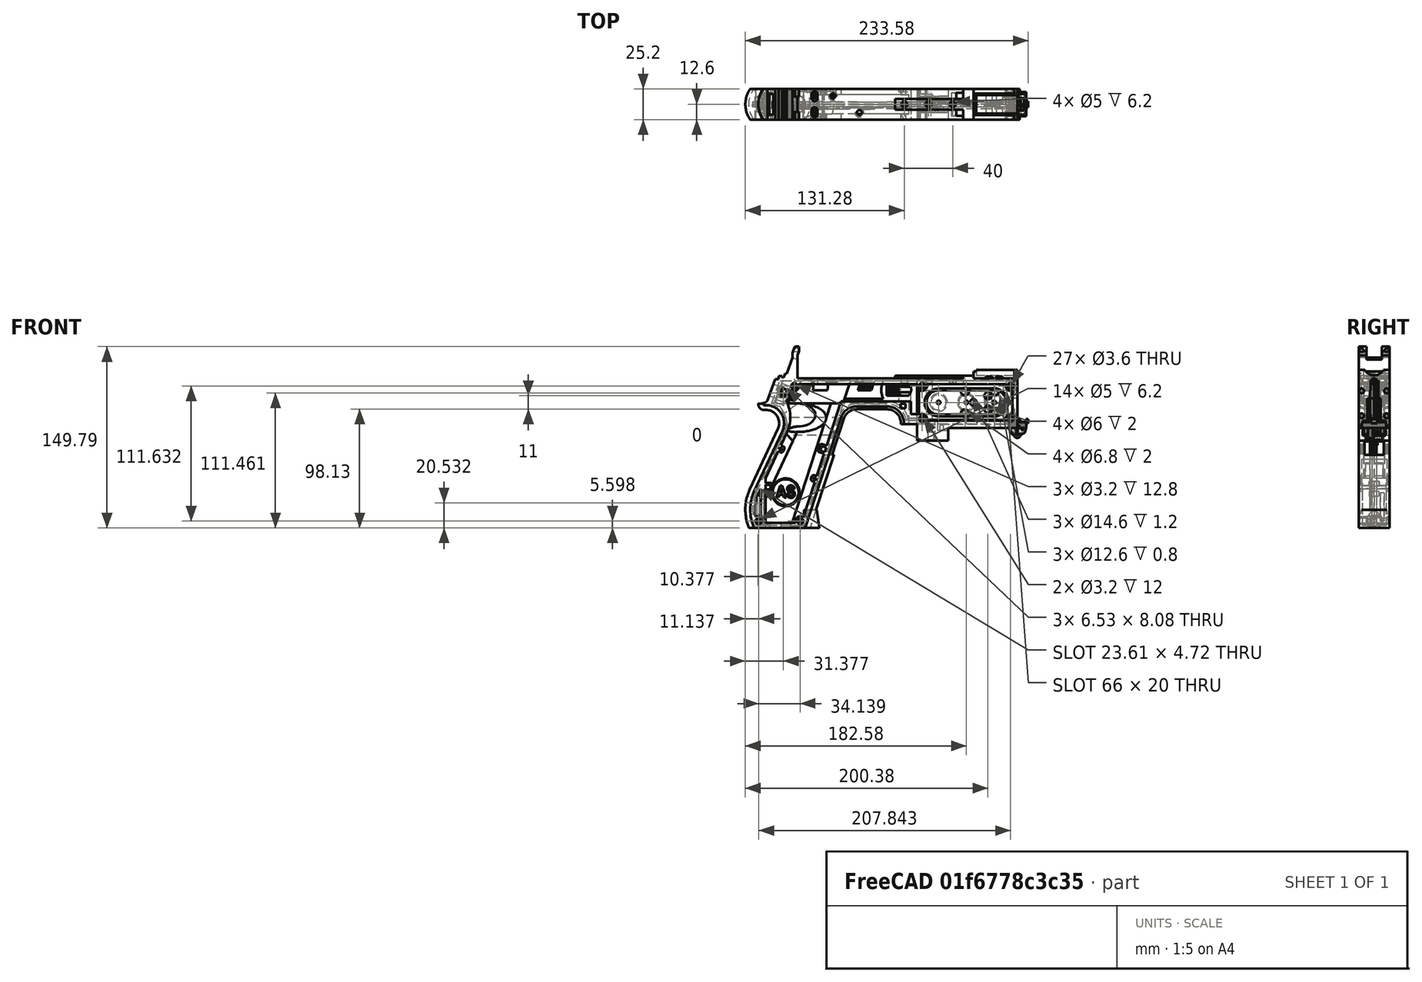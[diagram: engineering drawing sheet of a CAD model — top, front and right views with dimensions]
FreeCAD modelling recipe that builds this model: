
FCSTD DOCUMENT  (FreeCAD 1.0R39319 (Git))
Label: PICON-OF_ver_33
License: All rights reserved
LicenseURL: https://en.wikipedia.org/wiki/All_rights_reserved
objects: Sketcher::SketchObject×120, Part::Extrusion×75, Part::Cut×47, PartDesign::Pad×19, PartDesign::Chamfer×14, PartDesign::Pocket×13, PartDesign::Fillet×9, PartDesign::Body×8, Part::MultiFuse×6, PartDesign::SubtractivePipe×4, PartDesign::SubtractiveLoft×4, Part::Part2DObjectPython×3, PartDesign::Plane×2, PartDesign::SubShapeBinder×2, Part::Sweep×1, PartDesign::ShapeBinder×1, PartDesign::FeatureBase×1, Part::Cone×1, Part::Chamfer×1, Part::Mirroring×1, +1 more types
note: 579 computed .brp shape members not serialized (recipe doc carries the construction recipe); baked Part::Feature solids carry a one-line shape summary decoded from their .brp

FEATURE [Sketcher::SketchObject] Sketch  label="corpo principale"
  ArcFitTolerance = 1e-06
  AttacherType = Attacher::AttachEngine3D
  AttachmentSupport = -> [XZ_Plane]
  FullyConstrained = true
  MakeInternals = false
  MapMode = 5
  Placement = pos=(0,0,0) rot=(1,0,0;1.5708rad)
  sketch-geometry (65):
    g0: LineSegment StartX=0 StartY=0 StartZ=0 EndX=-57.2 EndY=0 EndZ=0
    g1: LineSegment StartX=-57.2 StartY=0 StartZ=0 EndX=-57.2 EndY=-10.4 EndZ=0
    g2: LineSegment StartX=-57.2 StartY=-10.4 StartZ=0 EndX=-82.8 EndY=-10.4 EndZ=0
    g3: LineSegment StartX=-82.8 StartY=-10.4 StartZ=0 EndX=-82.8 EndY=3.2 EndZ=0
    g4: LineSegment StartX=-82.8 StartY=3.2 StartZ=0 EndX=-93.6 EndY=3.2 EndZ=0
    g5: LineSegment StartX=-93.6 StartY=3.2 StartZ=0 EndX=-93.6 EndY=4 EndZ=0
    g6: LineSegment StartX=-107.6 StartY=18 StartZ=0 EndX=-132.428 EndY=18 EndZ=0
    g7: LineSegment StartX=-145.743 StartY=8.32624 StartZ=0 EndX=-175.232 EndY=-82.4316 EndZ=0
    g8: LineSegment StartX=-175.232 StartY=-82.4316 StartZ=0 EndX=-217.232 EndY=-82.4316 EndZ=0
    g9: LineSegment StartX=-217.232 StartY=-52.1862 StartZ=0 EndX=-193.988 EndY=-2.33927 EndZ=0
    g10: LineSegment StartX=-206.196 StartY=23.0857 StartZ=0 EndX=-199.861 EndY=40.4914 EndZ=0
    g11: LineSegment StartX=-199.861 StartY=40.4914 StartZ=0 EndX=-197.061 EndY=40.4914 EndZ=0
    g12: LineSegment StartX=-197.061 StartY=40.4914 StartZ=0 EndX=-197.061 EndY=42.8914 EndZ=0
    g13: LineSegment StartX=-197.061 StartY=42.8914 StartZ=0 EndX=-194.261 EndY=42.8914 EndZ=0
    g14: LineSegment StartX=-194.261 StartY=42.8914 StartZ=0 EndX=-194.535 EndY=42.1397 EndZ=0
    g15: LineSegment StartX=-194.535 StartY=42.1397 StartZ=0 EndX=-193.031 EndY=41.5924 EndZ=0
    g16: LineSegment StartX=-193.031 StartY=41.5924 StartZ=0 EndX=-191.663 EndY=45.3512 EndZ=0
    g17: LineSegment StartX=-191.663 StartY=45.3512 StartZ=0 EndX=-190.536 EndY=44.9408 EndZ=0
    g18: LineSegment StartX=-190.536 StartY=44.9408 StartZ=0 EndX=-185.747 EndY=58.0965 EndZ=0
    g19: LineSegment StartX=-185.747 StartY=58.0965 StartZ=0 EndX=-185.747 EndY=62.0965 EndZ=0
    g20: LineSegment StartX=-185.747 StartY=62.0965 StartZ=0 EndX=-183.832 EndY=67.3588 EndZ=0
    g21: LineSegment StartX=-183.832 StartY=67.3588 StartZ=0 EndX=-180.232 EndY=67.3588 EndZ=0
    g22: LineSegment StartX=-180.232 StartY=67.3588 StartZ=0 EndX=-180.232 EndY=63.7588 EndZ=0
    g23: LineSegment StartX=-180.232 StartY=63.7588 StartZ=0 EndX=-181.6 EndY=60 EndZ=0
    g24: LineSegment StartX=-181.6 StartY=60 StartZ=0 EndX=-181.6 EndY=41.2 EndZ=0
    g25: LineSegment StartX=-181.6 StartY=41.2 StartZ=0 EndX=-100.8 EndY=41.2 EndZ=0
    g26: LineSegment StartX=-36 StartY=43.2 StartZ=0 EndX=-36 EndY=41.2 EndZ=0
    g27: LineSegment StartX=0 StartY=48 StartZ=0 EndX=0 EndY=0 EndZ=0
    g28: LineSegment StartX=-209.901 StartY=19.85 StartZ=0 EndX=-209.901 EndY=20.1 EndZ=0
    g29: LineSegment StartX=-208.001 StartY=22 StartZ=0 EndX=-207.747 EndY=22 EndZ=0
    g30: LineSegment StartX=-207.583 StartY=19 StartZ=0 EndX=-209.051 EndY=19 EndZ=0
    g31: ArcOfCircle CenterX=-208.001 CenterY=20.1 CenterZ=0 NormalX=0 NormalY=0 NormalZ=1 AngleXU=0 Radius=1.9 StartAngle=1.5708 EndAngle=3.14159
    g32: GeomPoint [constr] X=-209.901 Y=22 Z=0
    g33: ArcOfCircle CenterX=-209.051 CenterY=19.85 CenterZ=0 NormalX=0 NormalY=0 NormalZ=1 AngleXU=0 Radius=0.85 StartAngle=3.14159 EndAngle=4.71239
    g34: GeomPoint [constr] X=-209.901 Y=19 Z=0
    g35: ArcOfCircle CenterX=-207.747 CenterY=23.65 CenterZ=0 NormalX=0 NormalY=0 NormalZ=1 AngleXU=0 Radius=1.65 StartAngle=4.71239 EndAngle=5.93412
    g36: GeomPoint [constr] X=-206.591 Y=22 Z=0
    g37: LineSegment StartX=-4 StartY=6 StartZ=0 EndX=-4 EndY=36.4 EndZ=0
    g38: LineSegment StartX=-4 StartY=36.4 StartZ=0 EndX=-185.2 EndY=36.4 EndZ=0
    g39: LineSegment StartX=-185.2 StartY=36.4 StartZ=0 EndX=-190.441 EndY=22 EndZ=0
    g40: LineSegment StartX=-214.575 StartY=-78.4316 StartZ=0 EndX=-178.142 EndY=-78.4316 EndZ=0
    g41: LineSegment StartX=-178.142 StartY=-78.4316 StartZ=0 EndX=-145.51 EndY=22 EndZ=0
    g42: LineSegment StartX=-145.51 StartY=22 StartZ=0 EndX=-87.91 EndY=22 EndZ=0
    g43: LineSegment StartX=-87.91 StartY=22 StartZ=0 EndX=-87.91 EndY=11.6 EndZ=0
    g44: LineSegment StartX=-87.91 StartY=11.6 StartZ=0 EndX=-80.11 EndY=11.6 EndZ=0
    g45: LineSegment StartX=-80.11 StartY=11.6 StartZ=0 EndX=-80.11 EndY=6 EndZ=0
    g46: LineSegment StartX=-80.11 StartY=6 StartZ=0 EndX=-4 EndY=6 EndZ=0
    g47: LineSegment StartX=-190.363 StartY=-4.02975 StartZ=0 EndX=-213.607 EndY=-53.8767 EndZ=0
    g48: ArcOfCircle CenterX=-132.428 CenterY=4 CenterZ=0 NormalX=0 NormalY=0 NormalZ=1 AngleXU=0 Radius=14 StartAngle=1.5708 EndAngle=2.82743
    g49: GeomPoint [constr] X=-142.6 Y=18 Z=0
    g50: ArcOfCircle CenterX=-107.6 CenterY=4 CenterZ=0 NormalX=0 NormalY=0 NormalZ=1 AngleXU=0 Radius=14 StartAngle=0 EndAngle=1.5708
    g51: GeomPoint [constr] X=-93.6 Y=18 Z=0
    g52: ArcOfCircle CenterX=-184.801 CenterY=-67.3089 CenterZ=0 NormalX=0 NormalY=0 NormalZ=1 AngleXU=0 Radius=35.7833 StartAngle=2.70526 EndAngle=3.57792
    g53: ArcOfCircle CenterX=-207.583 CenterY=4 CenterZ=0 NormalX=0 NormalY=0 NormalZ=1 AngleXU=0 Radius=15 StartAngle=5.84685 EndAngle=7.85398
    g54: LineSegment [constr] StartX=-213.607 StartY=-53.8767 StartZ=0 EndX=-217.232 EndY=-52.1862 EndZ=0
    g55: ArcOfCircle CenterX=-184.801 CenterY=-67.3089 CenterZ=0 NormalX=0 NormalY=0 NormalZ=1 AngleXU=0 Radius=31.7833 StartAngle=2.70526 EndAngle=3.49911
    g56: ArcOfCircle CenterX=-218.095 CenterY=8.90192 CenterZ=0 NormalX=0 NormalY=0 NormalZ=1 AngleXU=0 Radius=30.5989 StartAngle=5.84685 EndAngle=6.72553
    g57: LineSegment StartX=-44.6 StartY=43.2 StartZ=0 EndX=-36 EndY=43.2 EndZ=0
    g58: LineSegment StartX=-100.8 StartY=41.2 StartZ=0 EndX=-44.6 EndY=41.2 EndZ=0
    g59: LineSegment StartX=-44.6 StartY=41.2 StartZ=0 EndX=-44.6 EndY=43.2 EndZ=0
    g60: LineSegment StartX=-2.4 StartY=48 StartZ=0 EndX=0 EndY=48 EndZ=0
    g61: LineSegment StartX=-36 StartY=41.2 StartZ=0 EndX=-2.4 EndY=41.2 EndZ=0
    g62: LineSegment StartX=-2.4 StartY=41.2 StartZ=0 EndX=-2.4 EndY=48 EndZ=0
    g63: LineSegment [constr] StartX=-181.6 StartY=36.4 StartZ=0 EndX=-152.209 EndY=36.4 EndZ=0
    g64: LineSegment [constr] StartX=-181.6 StartY=36.4 StartZ=0 EndX=-130.41 EndY=36.4 EndZ=0
  constraints (183):
    c: Coincident(g-1,g0)
    c: PointOnObject(g0,g-1)
    c: Coincident(g0,g1)
    c: Vertical(g1)
    c: Coincident(g1,g2)
    c: Horizontal(g2)
    c: Coincident(g2,g3)
    c: Vertical(g3)
    c: Coincident(g3,g4)
    c: Coincident(g4,g5)
    c: Vertical(g5)
    c: Horizontal(g6)
    c: Coincident(g7,g8)
    c: Horizontal(g8)
    c: Coincident(g10,g11)
    c: Horizontal(g11)
    c: Coincident(g11,g12)
    c: Vertical(g12)
    c: Coincident(g12,g13)
    c: Horizontal(g13)
    c: Coincident(g13,g14)
    c: Coincident(g14,g15)
    c: Coincident(g15,g16)
    c: Coincident(g16,g17)
    c: Coincident(g17,g18)
    c: Coincident(g18,g19)
    c: Vertical(g19)
    c: Coincident(g19,g20)
    c: Coincident(g20,g21)
    c: Horizontal(g21)
    c: Coincident(g21,g22)
    c: Vertical(g22)
    c: Coincident(g22,g23)
    c: Coincident(g23,g24)
    c: Vertical(g24)
    c: Coincident(g24,g25)
    c: Horizontal(g25)
    c: Coincident(g57,g26)
    c: Vertical(g26)
    c: Coincident(g26,g61)
    c: PointOnObject(g60,g-2)
    c: Coincident(g60,g27)
    c: Coincident(g27,g0)
    c: DistanceY(g27,g27) = 48
    c: DistanceY(g1,g1) = 10.4
    c: DistanceX(g0,g0) = 57.2
    c: DistanceX(g2,g2) = 25.6
    c: Horizontal(g4)
    c: DistanceY(g3,g3) = 13.6
    c: DistanceX(g4,g4) = 10.8
    c: DistanceY(g5,g51) = 14.8
    c: DistanceX(g49,g51) = 49
    c: Distance(g7,g49) = 105.6
    c: DistanceX(g61,g60) = 36
    c: DistanceX(g25,g25) = 80.8
    c: DistanceY(g24,g24) = 18.8
    c: DistanceY(g22,g22) = 3.6
    c: Distance(g23) = 4
    c: Angle(g-1,g23) = 1.22173
    c: DistanceX(g21,g21) = 3.6
    c: Distance(g20) = 5.6
    c: Angle(g-1,g20) = 1.22173
    c: DistanceY(g19,g19) = 4
    c: Distance(g18) = 14
    c: Angle(g-1,g18) = 1.22173
    c: Distance(g17) = 1.2
    c: Distance(g16) = 4
    c: Angle(g16) = 1.22173
    c: Perpendicular(g18,g17)
    c: Distance(g15) = 1.6
    c: Perpendicular(g16,g15)
    c: Distance(g14) = 0.8
    c: DistanceX(g13,g13) = 2.8
    c: Perpendicular(g15,g14)
    c: DistanceY(g12,g12) = 2.4
    c: DistanceX(g11,g11) = 2.8
    c: Distance(g9) = 55
    c: Angle(g9,g-1) = 2.00713
    c: Horizontal(g29)
    c: Vertical(g28)
    c: Horizontal(g30)
    c: PointOnObject(g32,g29)
    c: PointOnObject(g32,g28)
    c: Tangent(g29,g31) = 1.5708
    c: Tangent(g28,g31) = 1.5708
    c: PointOnObject(g34,g28)
    c: PointOnObject(g34,g30)
    c: Tangent(g28,g33) = 1.5708
    c: Tangent(g30,g33) = 1.5708
    c: PointOnObject(g36,g29)
    c: PointOnObject(g36,g10)
    c: Tangent(g29,g35) = -1.5708
    c: Tangent(g10,g35) = -1.5708
    c: Angle(g-1,g10) = 1.22173
    c: Radius(g35) = 1.65
    c: Vertical(g37)
    c: Coincident(g37,g38)
    c: Horizontal(g38)
    c: Coincident(g38,g39)
    c: Horizontal(g40)
    c: Coincident(g40,g41)
    c: Coincident(g41,g42)
    c: Horizontal(g42)
    c: Coincident(g42,g43)
    c: Vertical(g43)
    c: Coincident(g43,g44)
    c: Horizontal(g44)
    c: Coincident(g44,g45)
    c: Vertical(g45)
    c: Coincident(g45,g46)
    c: Coincident(g46,g37)
    c: Horizontal(g46)
    c: DistanceY(g0,g37) = 6
    c: DistanceX(g37,g0) = 4
    c: DistanceY(g37,g25) = 4.8
    c: DistanceX(g38,g38) = 181.2
    c: DistanceX(g42,g42) = 57.6
    c: DistanceY(g49,g41) = 4
    c: DistanceX(g41,g49) = 2.91
    c: DistanceY(g43,g43) = 10.4
    c: DistanceX(g44,g44) = 7.8
    c: DistanceY(g7,g40) = 4
    c: Distance(g47) = 55
    c: Angle(g-1,g39) = 1.22173
    c: PointOnObject(g49,g7)
    c: PointOnObject(g49,g6)
    c: Tangent(g7,g48) = -1.5708
    c: Tangent(g6,g48) = -1.5708
    c: PointOnObject(g51,g5)
    c: PointOnObject(g51,g6)
    c: Tangent(g5,g50) = -1.5708
    c: Tangent(g6,g50) = -1.5708
    c: Radius(g50) = 14
    c: Radius(g48) = 14
    c: DistanceX(g8,g8) = 42
    c: Angle(g7,g-1) = 1.88496
    c: Parallel(g41,g7)
    c: Parallel(g47,g9)
    c: Coincident(g52,g8)
    c: Tangent(g52,g9) = 1.5708
    c: DistanceX(g9,g8) = 0
    c: Tangent(g53,g9) = -1.5708
    c: Tangent(g53,g30) = -1.5708
    c: Diameter(g53) = 30
    c: DistanceY(g53,g0) = -4
    c: Coincident(g54,g47)
    c: Distance(g54) = 4
    c: Coincident(g54,g9)
    c: Coincident(g55,g40)
    c: Tangent(g55,g47) = -1.5708
    c: Coincident(g52,g55)
    c: Coincident(g56,g39)
    c: Tangent(g56,g47) = 1.5708
    c: Horizontal(g57)
    c: DistanceX(g57,g57) = 8.6
    c: Coincident(g58,g25)
    c: Horizontal(g58)
    c: Coincident(g59,g58)
    c: Vertical(g59)
    c: DistanceY(g58,g57) = 2
    c: DistanceX(g58,g58) = 56.2
    c: Coincident(g59,g57)
    c: DistanceY(g41,g36) = 0
    c: DistanceY(g36,g39) = 0
    c: DistanceY(g28,g28) = 0.25
    c: DistanceX(g30,g36) = 2.46
    c: DistanceX(g28,g29) = 1.9
    c: Coincident(g62,g60)
    c: Horizontal(g60)
    c: DistanceX(g62,g27) = 2.4
    c: Coincident(g61,g62)
    c: DistanceY(g26,g26) = 2
    c: Vertical(g62)
    c: DistanceY(g61,g60) = 6.8
    c: Horizontal(g61)
    c: Distance(g63) = 29.391
    c: PointOnObject(g63,g38)
    c: PointOnObject(g63,g38)
    c: Distance(g64) = 51.19
    c: PointOnObject(g64,g38)
    c: PointOnObject(g64,g38)
    c: DistanceX(g24,g63) = 0
    c: DistanceX(g24,g64) = 0
FEATURE [Part::Extrusion] Extrude  label="Extrude corpo principale"
  Base = -> Sketch
  Dir = (0,-1,2e-16)
  DirMode = 2
  FaceMakerClass = Part::FaceMakerBullseye
  FaceMakerMode = 3
  LengthFwd = 25.2
  LengthRev = 12.6
  Solid = true
  Symmetric = true
FEATURE [Sketcher::SketchObject] Sketch002  label="scavo grilletto"
  ArcFitTolerance = 1e-06
  AttachmentSupport = -> [XZ_Plane]
  ExternalGeometry = -> [Sketch]
  FullyConstrained = true
  MakeInternals = false
  MapMode = 5
  Placement = pos=(0,0,0) rot=(1,0,0;1.5708rad)
  sketch-geometry (4):
    g0: LineSegment StartX=-89.51 StartY=22 StartZ=0 EndX=-152.71 EndY=22 EndZ=0
    g1: LineSegment StartX=-152.71 StartY=22 StartZ=0 EndX=-167.006 EndY=-22 EndZ=0
    g2: LineSegment StartX=-167.006 StartY=-22 StartZ=0 EndX=-89.51 EndY=-22 EndZ=0
    g3: LineSegment StartX=-89.51 StartY=-22 StartZ=0 EndX=-89.51 EndY=22 EndZ=0
  constraints (12):
    c: Horizontal(g0)
    c: Coincident(g0,g1)
    c: Coincident(g1,g2)
    c: Horizontal(g2)
    c: Coincident(g2,g3)
    c: Coincident(g3,g0)
    c: Vertical(g3)
    c: Angle(g1,g0) = 1.88496
    c: DistanceY(g3,g3) = 44
    c: DistanceX(g0,g0) = 63.2
    c: DistanceX(g0,g-3) = 1.6
    c: DistanceY(g-3,g0) = 0
FEATURE [Sketcher::SketchObject] Sketch004  label="traiettoria arrotondamento impugnatura anteriore"
  ArcFitTolerance = 1e-06
  AttachmentSupport = -> [XZ_Plane]
  ExternalGeometry = -> [Sketch]
  FullyConstrained = true
  MakeInternals = false
  MapMode = 5
  Placement = pos=(0,0,0) rot=(1,0,0;1.5708rad)
  sketch-geometry (13):
    g0: LineSegment StartX=-175.232 StartY=-82.4316 StartZ=0 EndX=-145.743 EndY=8.32624 EndZ=0
    g1: LineSegment StartX=-93.6 StartY=3.2 StartZ=0 EndX=-93.6 EndY=4 EndZ=0
    g2: LineSegment StartX=-132.428 StartY=18 StartZ=0 EndX=-107.6 EndY=18 EndZ=0
    g3: ArcOfCircle CenterX=-132.428 CenterY=4 CenterZ=0 NormalX=0 NormalY=0 NormalZ=1 AngleXU=0 Radius=14 StartAngle=1.5708 EndAngle=2.82743
    g4: ArcOfCircle CenterX=-107.6 CenterY=4 CenterZ=0 NormalX=0 NormalY=0 NormalZ=1 AngleXU=0 Radius=14 StartAngle=0 EndAngle=1.5708
    g5: LineSegment StartX=-175.232 StartY=-82.4316 StartZ=0 EndX=-217.232 EndY=-82.4316 EndZ=0
    g6: LineSegment StartX=-217.232 StartY=-52.1862 StartZ=0 EndX=-193.988 EndY=-2.33927 EndZ=0
    g7: LineSegment StartX=-209.051 StartY=19 StartZ=0 EndX=-207.583 EndY=19 EndZ=0
    g8: LineSegment StartX=-209.901 StartY=20.1 StartZ=0 EndX=-209.901 EndY=19.85 EndZ=0
    g9: ArcOfCircle CenterX=-184.801 CenterY=-67.3089 CenterZ=0 NormalX=0 NormalY=0 NormalZ=1 AngleXU=0 Radius=35.7833 StartAngle=2.70526 EndAngle=3.57792
    g10: ArcOfCircle CenterX=-207.583 CenterY=4 CenterZ=0 NormalX=0 NormalY=0 NormalZ=1 AngleXU=0 Radius=15 StartAngle=5.84685 EndAngle=7.85398
    g11: ArcOfCircle CenterX=-209.051 CenterY=19.85 CenterZ=0 NormalX=0 NormalY=0 NormalZ=1 AngleXU=0 Radius=0.85 StartAngle=3.14159 EndAngle=4.71239
    g12: ArcOfCircle CenterX=-208.001 CenterY=20.1 CenterZ=0 NormalX=0 NormalY=0 NormalZ=1 AngleXU=0 Radius=1.9 StartAngle=1.5708 EndAngle=3.14159
  constraints (26):
    c: Coincident(g0,g-3)
    c: Coincident(g0,g-6)
    c: Coincident(g1,g-8)
    c: Coincident(g1,g-7)
    c: Coincident(g2,g-5)
    c: Coincident(g2,g-4)
    c: Coincident(g3,g2)
    c: Tangent(g3,g0) = 1.5708
    c: Coincident(g4,g1)
    c: Tangent(g4,g2) = 1.5708
    c: Coincident(g5,g0)
    c: Coincident(g5,g-9)
    c: Coincident(g6,g-12)
    c: Coincident(g6,g-11)
    c: Coincident(g7,g-15)
    c: Coincident(g7,g-14)
    c: Coincident(g8,g-16)
    c: Coincident(g8,g-17)
    c: Tangent(g9,g6) = 1.5708
    c: Coincident(g9,g5)
    c: Coincident(g10,g7)
    c: Tangent(g10,g6) = -1.5708
    c: Tangent(g11,g7) = -1.5708
    c: Coincident(g11,g8)
    c: Tangent(g12,g8) = -1.5708
    c: Coincident(g12,g-17)
FEATURE [PartDesign::Plane] DatumPlane  label="Piano per disegno arrotondamento impugnatura"
  AttachmentSupport = -> [Sketch]
  Length = 68.5841
  MapMode = 7
  Placement = pos=(-145.743,1.8e-15,8.32624) rot=(0.154555,0.154555,0.97582;1.59527rad)
  ResizeMode = 0
  Width = 191.269
FEATURE [Sketcher::SketchObject] Sketch005  label="forma arrotondamento impugnatura anteriore"
  ArcFitTolerance = 1e-06
  AttachmentSupport = -> [DatumPlane]
  FullyConstrained = true
  MakeInternals = false
  MapMode = 5
  Placement = pos=(-145.743,1.8e-15,8.32624) rot=(0.154555,0.154555,0.97582;1.59527rad)
  sketch-geometry (5):
    g0: GeomPoint [constr] X=0 Y=-4 Z=0
    g1: GeomPoint [constr] X=-12.6 Y=7.1e-15 Z=0
    g2: GeomPoint [constr] X=12.6 Y=4.97e-14 Z=0
    g3: LineSegment StartX=-12.6 StartY=7.1e-15 StartZ=0 EndX=12.6 EndY=4.97e-14 EndZ=0
    g4: ArcOfCircle CenterX=-3.88e-14 CenterY=17.845 CenterZ=0 NormalX=0 NormalY=0 NormalZ=1 AngleXU=0 Radius=21.845 StartAngle=4.09759 EndAngle=5.32718
  constraints (11):
    c: DistanceY(g0,g-1) = 4
    c: DistanceX(g-1,g0) = 0
    c: DistanceX(g1,g-1) = 12.6
    c: DistanceX(g-1,g2) = 12.6
    c: DistanceY(g-1,g2) = 0
    c: DistanceY(g-1,g1) = 0
    c: Coincident(g3,g1)
    c: Coincident(g3,g2)
    c: Coincident(g4,g1)
    c: Coincident(g4,g2)
    c: PointOnObject(g0,g4)
FEATURE [Part::Sweep] Sweep  label="Sweep impugnatura"
  Frenet = true
  Sections = -> [Sketch005]
  Solid = true
  Spine = -> Sketch [Edge32,Edge33,Edge34,Edge35,Edge36,Edge37,Edge38,Edge39,Edge40,Edge41,Edge42,Edge43,Edge44]
  Transition = 1
FEATURE [Sketcher::SketchObject] Sketch008  label="buchi e pulizie varie"
  ArcFitTolerance = 1e-06
  AttachmentSupport = -> [XZ_Plane]
  ExternalGeometry = -> [Sketch]
  FullyConstrained = true
  MakeInternals = false
  MapMode = 5
  Placement = pos=(0,0,0) rot=(1,0,0;1.5708rad)
  sketch-geometry (26):
    g0: LineSegment StartX=-96.278 StartY=20.155 StartZ=0 EndX=-92.278 EndY=20.155 EndZ=0
    g1: LineSegment StartX=-92.278 StartY=20.155 StartZ=0 EndX=-92.278 EndY=16.155 EndZ=0
    g2: LineSegment StartX=-92.278 StartY=16.155 StartZ=0 EndX=-96.278 EndY=16.155 EndZ=0
    g3: LineSegment StartX=-96.278 StartY=16.155 StartZ=0 EndX=-96.278 EndY=20.155 EndZ=0
    g4: LineSegment StartX=-222.232 StartY=-82.4316 StartZ=0 EndX=-170.232 EndY=-82.4316 EndZ=0
    g5: LineSegment StartX=-170.232 StartY=-82.4316 StartZ=0 EndX=-170.232 EndY=-86.4316 EndZ=0
    g6: LineSegment StartX=-170.232 StartY=-86.4316 StartZ=0 EndX=-222.232 EndY=-86.4316 EndZ=0
    g7: LineSegment StartX=-222.232 StartY=-86.4316 StartZ=0 EndX=-222.232 EndY=-82.4316 EndZ=0
    g8: LineSegment StartX=-213.901 StartY=20.1 StartZ=0 EndX=-213.901 EndY=26 EndZ=0
    g9: LineSegment StartX=-213.901 StartY=26 StartZ=0 EndX=-206.196 EndY=26 EndZ=0
    g10: LineSegment StartX=-17.4 StartY=42.8 StartZ=0 EndX=-12.4 EndY=42.8 EndZ=0
    g11: LineSegment StartX=-12.4 StartY=42.8 StartZ=0 EndX=-12.4 EndY=41.2 EndZ=0
    g12: LineSegment StartX=-12.4 StartY=41.2 StartZ=0 EndX=-17.4 EndY=41.2 EndZ=0
    g13: LineSegment StartX=-17.4 StartY=41.2 StartZ=0 EndX=-17.4 EndY=42.8 EndZ=0
    g14: LineSegment StartX=-25.9 StartY=42.8 StartZ=0 EndX=-20.9 EndY=42.8 EndZ=0
    g15: LineSegment StartX=-20.9 StartY=42.8 StartZ=0 EndX=-20.9 EndY=41.2 EndZ=0
    g16: LineSegment StartX=-20.9 StartY=41.2 StartZ=0 EndX=-25.9 EndY=41.2 EndZ=0
    g17: LineSegment StartX=-25.9 StartY=41.2 StartZ=0 EndX=-25.9 EndY=42.8 EndZ=0
    g18: GeomPoint [constr] X=-206.196 Y=23.0857 Z=0
    g19: GeomPoint [constr] X=-213.901 Y=20.1 Z=0
    g20: BSplineCurve PolesCount=4 KnotsCount=2 Degree=3 IsPeriodic=0
    g21-g24: Circle [constr] x4 (B-spline internal-alignment scaffolding for g20; pole/knot coordinates omitted)
    g25: LineSegment StartX=-206.196 StartY=26 StartZ=0 EndX=-206.196 EndY=23.0857 EndZ=0
  constraints (73):
    c: Horizontal(g0)
    c: Coincident(g1,g0)
    c: Vertical(g1)
    c: Coincident(g2,g1)
    c: Horizontal(g2)
    c: Coincident(g3,g2)
    c: Coincident(g3,g0)
    c: Vertical(g3)
    c: DistanceX(g0,g-4) = 4.368
    c: DistanceY(g0,g-4) = 1.845
    c: DistanceY(g1,g1) = 4
    c: DistanceX(g2,g2) = 4
    c: Horizontal(g4)
    c: Coincident(g5,g4)
    c: Vertical(g5)
    c: Coincident(g6,g5)
    c: Horizontal(g6)
    c: Coincident(g7,g6)
    c: Coincident(g7,g4)
    c: Vertical(g7)
    c: DistanceY(g7,g7) = 4
    c: DistanceX(g4,g-5) = 5
    c: DistanceX(g-5,g4) = 5
    c: DistanceY(g4,g-5) = 0
    c: Coincident(g9,g8)
    c: Parallel(g9,g-6)
    c: DistanceX(g8,g-8) = 4
    c: Horizontal(g10)
    c: Coincident(g11,g10)
    c: Vertical(g11)
    c: Coincident(g12,g11)
    c: Horizontal(g12)
    c: Coincident(g13,g12)
    c: Coincident(g13,g10)
    c: Vertical(g13)
    c: Horizontal(g14)
    c: Coincident(g15,g14)
    c: Vertical(g15)
    c: Coincident(g16,g15)
    c: Horizontal(g16)
    c: Coincident(g17,g16)
    c: Coincident(g17,g14)
    c: Vertical(g17)
    c: DistanceY(g11,g10) = 1.6
    c: DistanceX(g10,g10) = 5
    c: DistanceY(g15,g14) = 1.6
    c: DistanceX(g14,g14) = 5
    c: DistanceX(g15,g12) = 3.5
    c: DistanceX(g11,g-9) = 10
    c: DistanceY(g-9,g11) = 0
    c: DistanceY(g-9,g15) = 0
    c: Perpendicular(g8,g9)
    c: DistanceY(g-7,g9) = 4
    c: DistanceY(g8,g-8) = 0
    c: InternalAlignment(g18,g20)
    c: InternalAlignment(g19,g20)
    c: InternalAlignment(g21,g20)
    c: Weight(g21) = 1
    c: InternalAlignment(g22,g20)
    c: Equal(g22,g21)
    c: InternalAlignment(g23,g20)
    c: Equal(g23,g21)
    c: InternalAlignment(g24,g20)
    c: Equal(g24,g21)
    c: Coincident(g18,g-12)
    c: Coincident(g19,g8)
    c: Coincident(g25,g9)
    c: Coincident(g25,g20)
    c: Vertical(g25)
    c: DistanceY(g20,g23) = 0
    c: DistanceY(g22,g18) = 2.26
    c: DistanceX(g22,g18) = 0.93
    c: DistanceX(g20,g23) = 2.9
FEATURE [Part::Extrusion] Extrude004  label="Extrude Buchi e pulizie varie"
  Base = -> Sketch008
  Dir = (0,-1,2e-16)
  DirMode = 2
  FaceMakerClass = Part::FaceMakerBullseye
  FaceMakerMode = 3
  LengthFwd = 25.2
  LengthRev = 0
  Solid = true
  Symmetric = true
FEATURE [Sketcher::SketchObject] Sketch009  label="rinforzi"
  ArcFitTolerance = 1e-06
  AttachmentSupport = -> [XZ_Plane]
  ExternalGeometry = -> [Sketch]
  FullyConstrained = true
  MakeInternals = false
  MapMode = 5
  Placement = pos=(0,0,0) rot=(1,0,0;1.5708rad)
  sketch-geometry (9):
    g0: LineSegment StartX=-87.91 StartY=22 StartZ=0 EndX=-87.91 EndY=36.4 EndZ=0
    g1: LineSegment StartX=-87.91 StartY=36.4 StartZ=0 EndX=-97.91 EndY=36.4 EndZ=0
    g2: LineSegment StartX=-97.91 StartY=36.4 StartZ=0 EndX=-97.91 EndY=22 EndZ=0
    g3: LineSegment StartX=-97.91 StartY=22 StartZ=0 EndX=-87.91 EndY=22 EndZ=0
    g4: LineSegment StartX=-149.713 StartY=9.06563 StartZ=0 EndX=-154.586 EndY=-5.93437 EndZ=0
    g5: LineSegment StartX=-154.586 StartY=-5.93437 StartZ=0 EndX=-191.863 EndY=-5.93437 EndZ=0
    g6: LineSegment StartX=-191.863 StartY=-5.93437 StartZ=0 EndX=-191.863 EndY=9.06563 EndZ=0
    g7: LineSegment StartX=-191.863 StartY=9.06563 StartZ=0 EndX=-149.713 EndY=9.06563 EndZ=0
    g8: LineSegment [constr] StartX=-145.51 StartY=22 StartZ=0 EndX=-149.713 EndY=9.06563 EndZ=0
  constraints (25):
    c: Vertical(g0)
    c: Coincident(g1,g0)
    c: Horizontal(g1)
    c: Coincident(g2,g1)
    c: Vertical(g2)
    c: Coincident(g3,g2)
    c: Coincident(g3,g0)
    c: Horizontal(g3)
    c: Coincident(g0,g-4)
    c: DistanceX(g3,g3) = 10
    c: DistanceY(g0,g-3) = 0
    c: Coincident(g5,g4)
    c: Horizontal(g5)
    c: Coincident(g6,g5)
    c: Vertical(g6)
    c: Coincident(g7,g6)
    c: Coincident(g7,g4)
    c: Horizontal(g7)
    c: Distance(g8) = 13.6
    c: Parallel(g-6,g8)
    c: Coincident(g-6,g8)
    c: Parallel(g4,g-6)
    c: DistanceY(g4,g4) = 15
    c: Coincident(g4,g8)
    c: DistanceX(g-5,g5) = -1.5
FEATURE [Part::Extrusion] Extrude001  label="Extrude scavo grilletto"
  Base = -> Sketch002
  Dir = (0,-1,2e-16)
  DirMode = 2
  FaceMakerClass = Part::FaceMakerBullseye
  FaceMakerMode = 3
  LengthFwd = 16
  LengthRev = 0
  Solid = true
  Symmetric = true
FEATURE [Part::Extrusion] Extrude005  label="Extrude Rinforzi"
  Base = -> Sketch009
  Dir = (0,-1,2e-16)
  DirMode = 2
  FaceMakerClass = Part::FaceMakerBullseye
  FaceMakerMode = 3
  LengthFwd = 2
  LengthRev = 0
  Placement = pos=(0,12.6,0) rot=(0,0,1;0rad)
  Solid = true
  Symmetric = false
FEATURE [PartDesign::ShapeBinder] CopyCut
  TraceSupport = false
FEATURE [PartDesign::Plane] DatumPlane001
  AttachmentSupport = -> [CopyCut]
  Length = 60
  MapMode = 5
  Placement = pos=(0,12.6,0) rot=(0,0.707107,0.707107;3.14159rad)
  ResizeMode = 0
  Width = 60
FEATURE [Sketcher::SketchObject] Sketch010  label="buco neopixel"
  ArcFitTolerance = 1e-06
  AttachmentSupport = -> [XZ_Plane]
  ExternalGeometry = -> [Sketch]
  FullyConstrained = true
  MakeInternals = false
  MapMode = 5
  Placement = pos=(0,0,0) rot=(1,0,0;1.5708rad)
  sketch-geometry (5):
    g0: LineSegment [constr] StartX=-199.861 StartY=40.4914 StartZ=0 EndX=-201.368 EndY=36.3521 EndZ=0
    g1: LineSegment StartX=-201.368 StartY=36.3521 StartZ=0 EndX=-204.932 EndY=26.5605 EndZ=0
    g2: LineSegment StartX=-201.368 StartY=36.3521 StartZ=0 EndX=-180.2 EndY=28.6477 EndZ=0
    g3: LineSegment StartX=-180.2 StartY=28.6477 StartZ=0 EndX=-183.764 EndY=18.8561 EndZ=0
    g4: LineSegment StartX=-183.764 StartY=18.8561 StartZ=0 EndX=-204.932 EndY=26.5605 EndZ=0
  constraints (14):
    c: Parallel(g0,g-3)
    c: Distance(g0) = 4.405
    c: Coincident(g0,g-3)
    c: Coincident(g2,g1)
    c: Coincident(g3,g2)
    c: Coincident(g4,g3)
    c: Coincident(g4,g1)
    c: Parallel(g1,g-3)
    c: Distance(g1) = 10.42
    c: Coincident(g1,g0)
    c: Parallel(g2,g4)
    c: Perpendicular(g1,g2)
    c: DistanceX(g-4,g2) = 5
    c: Parallel(g3,g1)
FEATURE [Part::Extrusion] Extrude006  label="Extrude buco neopixel"
  Base = -> Sketch010
  Dir = (0,-1,2e-16)
  DirMode = 2
  FaceMakerClass = Part::FaceMakerBullseye
  FaceMakerMode = 3
  LengthFwd = 17.2
  LengthRev = 0
  Solid = true
  Symmetric = true
FEATURE [Sketcher::SketchObject] Sketch011  label="fermo grilletto"
  ArcFitTolerance = 1e-06
  AttachmentSupport = -> [XZ_Plane]
  ExternalGeometry = -> [Sketch]
  FullyConstrained = true
  MakeInternals = false
  MapMode = 5
  Placement = pos=(0,0,0) rot=(1,0,0;1.5708rad)
  sketch-geometry (18):
    g0: LineSegment [constr] StartX=-145.51 StartY=22 StartZ=0 EndX=-157.347 EndY=-14.4293 EndZ=0
    g1: LineSegment [constr] StartX=-157.347 StartY=-14.4293 StartZ=0 EndX=-157.841 EndY=-15.951 EndZ=0
    g2: LineSegment StartX=-161.151 StartY=-13.1932 StartZ=0 EndX=-155.825 EndY=-14.9237 EndZ=0
    g3: LineSegment StartX=-163.167 StartY=-14.2205 StartZ=0 EndX=-164.403 EndY=-18.0247 EndZ=0
    g4: LineSegment StartX=-163.376 StartY=-20.0408 StartZ=0 EndX=-158.05 EndY=-21.7713 EndZ=0
    g5: LineSegment StartX=-158.05 StartY=-21.7713 StartZ=0 EndX=-155.825 EndY=-14.9237 EndZ=0
    g6: LineSegment StartX=-161.645 StartY=-14.7149 StartZ=0 EndX=-157.841 EndY=-15.951 EndZ=0
    g7: LineSegment StartX=-157.841 StartY=-15.951 StartZ=0 EndX=-159.077 EndY=-19.7552 EndZ=0
    g8: LineSegment StartX=-159.077 StartY=-19.7552 StartZ=0 EndX=-162.881 EndY=-18.5191 EndZ=0
    g9: LineSegment StartX=-162.881 StartY=-18.5191 StartZ=0 EndX=-161.645 EndY=-14.7149 EndZ=0
    g10: LineSegment [constr] StartX=-161.645 StartY=-14.7149 StartZ=0 EndX=-161.151 EndY=-13.1932 EndZ=0
    g11: LineSegment [constr] StartX=-159.077 StartY=-19.7552 StartZ=0 EndX=-157.555 EndY=-20.2496 EndZ=0
    g12: LineSegment [constr] StartX=-159.077 StartY=-19.7552 StartZ=0 EndX=-159.572 EndY=-21.2769 EndZ=0
    g13: LineSegment [constr] StartX=-161.645 StartY=-14.7149 StartZ=0 EndX=-163.167 EndY=-14.2205 EndZ=0
    g14: ArcOfCircle CenterX=-161.645 CenterY=-14.7149 CenterZ=0 NormalX=0 NormalY=0 NormalZ=1 AngleXU=0 Radius=1.6 StartAngle=1.25664 EndAngle=2.82743
    g15: GeomPoint [constr] X=-162.673 Y=-12.6988 Z=0
    g16: ArcOfCircle CenterX=-162.881 CenterY=-18.5191 CenterZ=0 NormalX=0 NormalY=0 NormalZ=1 AngleXU=0 Radius=1.6 StartAngle=2.82743 EndAngle=4.39823
    g17: GeomPoint [constr] X=-164.897 Y=-19.5464 Z=0
  constraints (48):
    c: Parallel(g0,g-3)
    c: Distance(g0) = 38.304
    c: Coincident(g0,g-3)
    c: Parallel(g1,g-3)
    c: Distance(g1) = 1.6
    c: Coincident(g1,g0)
    c: Coincident(g5,g4)
    c: Coincident(g5,g2)
    c: Coincident(g7,g6)
    c: Coincident(g8,g7)
    c: Coincident(g9,g8)
    c: Coincident(g9,g6)
    c: Parallel(g7,g-3)
    c: Parallel(g9,g7)
    c: Perpendicular(g6,g7)
    c: Parallel(g6,g8)
    c: Distance(g6) = 4
    c: Distance(g9) = 4
    c: Parallel(g5,g7)
    c: Parallel(g9,g3)
    c: Parallel(g2,g6)
    c: Parallel(g4,g8)
    c: Parallel(g13,g6)
    c: Parallel(g10,g9)
    c: Parallel(g11,g8)
    c: Parallel(g12,g7)
    c: Distance(g10) = 1.6
    c: Distance(g13) = 1.6
    c: Distance(g12) = 1.6
    c: Distance(g11) = 1.6
    c: Coincident(g10,g6)
    c: Coincident(g13,g6)
    c: Coincident(g12,g7)
    c: Coincident(g11,g7)
    c: Distance(g10,g15) = 1.6
    c: Distance(g15,g13) = 1.6
    c: Distance(g4,g12) = 1.6
    c: Distance(g4,g11) = 1.6
    c: PointOnObject(g15,g2)
    c: Tangent(g3,g14) = -1.5708
    c: Tangent(g2,g14) = 1.5708
    c: PointOnObject(g17,g4)
    c: PointOnObject(g17,g3)
    c: Tangent(g4,g16) = -1.5708
    c: Tangent(g3,g16) = -1.5708
    c: Equal(g16,g14)
    c: Coincident(g16,g8)
    c: Coincident(g6,g1)
FEATURE [Part::Extrusion] Extrude007  label="Extrude fermo grilletto"
  Base = -> Sketch011
  Dir = (0,-1,2e-16)
  DirMode = 2
  FaceMakerClass = Part::FaceMakerBullseye
  FaceMakerMode = 3
  LengthFwd = 25.2
  LengthRev = 0
  Solid = true
  Symmetric = true
FEATURE [Sketcher::SketchObject] Sketch012  label="buco oled"
  ArcFitTolerance = 1e-06
  AttachmentSupport = -> [XZ_Plane]
  ExternalGeometry = -> [Sketch]
  FullyConstrained = true
  MakeInternals = false
  MapMode = 5
  Placement = pos=(0,0,0) rot=(1,0,0;1.5708rad)
  sketch-geometry (4):
    g0: LineSegment StartX=-185.747 StartY=58.0965 StartZ=0 EndX=-180.232 EndY=56.0891 EndZ=0
    g1: LineSegment StartX=-185.747 StartY=58.0965 StartZ=0 EndX=-185.747 EndY=67.3588 EndZ=0
    g2: LineSegment StartX=-185.747 StartY=67.3588 StartZ=0 EndX=-180.232 EndY=67.3588 EndZ=0
    g3: LineSegment StartX=-180.232 StartY=67.3588 StartZ=0 EndX=-180.232 EndY=56.0891 EndZ=0
  constraints (10):
    c: Coincident(g1,g0)
    c: Coincident(g2,g1)
    c: Coincident(g3,g2)
    c: Coincident(g3,g0)
    c: Parallel(g1,g-5)
    c: Perpendicular(g-3,g0)
    c: Parallel(g2,g-6)
    c: Parallel(g3,g-4)
    c: Coincident(g0,g-5)
    c: Coincident(g2,g-6)
FEATURE [Part::Extrusion] Extrude008  label="Extrude buco oled"
  Base = -> Sketch012
  Dir = (0,-1,2e-16)
  DirMode = 2
  FaceMakerClass = Part::FaceMakerBullseye
  FaceMakerMode = 3
  LengthFwd = 12.8
  LengthRev = 0
  Solid = true
  Symmetric = true
FEATURE [Sketcher::SketchObject] Sketch013  label="buco pompa"
  ArcFitTolerance = 1e-06
  AttachmentSupport = -> [XZ_Plane]
  ExternalGeometry = -> [Sketch]
  FullyConstrained = true
  MakeInternals = false
  MapMode = 5
  Placement = pos=(0,0,0) rot=(1,0,0;1.5708rad)
  sketch-geometry (8):
    g0: LineSegment StartX=-82.8 StartY=-10.4 StartZ=0 EndX=-82.8 EndY=-9.6 EndZ=0
    g1: LineSegment StartX=-82.8 StartY=-9.6 StartZ=0 EndX=-67.9 EndY=-9.6 EndZ=0
    g2: LineSegment StartX=-67.9 StartY=-9.6 StartZ=0 EndX=-67.9 EndY=6 EndZ=0
    g3: LineSegment StartX=-67.9 StartY=6 StartZ=0 EndX=-65.9 EndY=6 EndZ=0
    g4: LineSegment StartX=-65.9 StartY=6 StartZ=0 EndX=-65.9 EndY=-1.7 EndZ=0
    g5: LineSegment StartX=-65.9 StartY=-1.7 StartZ=0 EndX=-57.2 EndY=-1.7 EndZ=0
    g6: LineSegment StartX=-57.2 StartY=-1.7 StartZ=0 EndX=-57.2 EndY=-10.4 EndZ=0
    g7: LineSegment StartX=-57.2 StartY=-10.4 StartZ=0 EndX=-82.8 EndY=-10.4 EndZ=0
  constraints (22):
    c: Vertical(g0)
    c: Coincident(g1,g0)
    c: Horizontal(g1)
    c: Coincident(g2,g1)
    c: Vertical(g2)
    c: Coincident(g3,g2)
    c: Horizontal(g3)
    c: Coincident(g4,g3)
    c: Vertical(g4)
    c: Coincident(g5,g4)
    c: Horizontal(g5)
    c: Coincident(g6,g5)
    c: Vertical(g6)
    c: Coincident(g7,g6)
    c: Coincident(g7,g0)
    c: DistanceY(g0,g0) = 0.8
    c: DistanceY(g6,g6) = 8.7
    c: DistanceX(g1,g1) = 14.9
    c: DistanceX(g3,g3) = 2
    c: Coincident(g0,g-4)
    c: DistanceY(g2,g-6) = 0
    c: Coincident(g6,g-5)
FEATURE [Part::Extrusion] Extrude009  label="Extrude buco pompa"
  Base = -> Sketch013
  Dir = (0,-1,2e-16)
  DirMode = 2
  FaceMakerClass = Part::FaceMakerBullseye
  FaceMakerMode = 3
  LengthFwd = 13.2
  LengthRev = 0
  Solid = true
  Symmetric = true
FEATURE [Sketcher::SketchObject] Sketch014  label="buco frontale"
  ArcFitTolerance = 1e-06
  AttachmentSupport = -> [XZ_Plane]
  ExternalGeometry = -> [Sketch]
  FullyConstrained = true
  MakeInternals = false
  MapMode = 5
  Placement = pos=(0,0,0) rot=(1,0,0;1.5708rad)
  sketch-geometry (10):
    g0: LineSegment StartX=0 StartY=0 StartZ=0 EndX=0 EndY=24.671 EndZ=0
    g1: LineSegment StartX=0 StartY=24.671 StartZ=0 EndX=-4 EndY=24.671 EndZ=0
    g2: LineSegment StartX=-4 StartY=24.671 StartZ=0 EndX=-4 EndY=16 EndZ=0
    g3: LineSegment StartX=-4 StartY=16 StartZ=0 EndX=-2.4 EndY=16 EndZ=0
    g4: LineSegment StartX=-2.4 StartY=16 StartZ=0 EndX=-2.4 EndY=10 EndZ=0
    g5: LineSegment StartX=-2.4 StartY=10 StartZ=0 EndX=-12 EndY=10 EndZ=0
    g6: LineSegment StartX=-12 StartY=10 StartZ=0 EndX=-12 EndY=6 EndZ=0
    g7: LineSegment StartX=-12 StartY=6 StartZ=0 EndX=-2.4 EndY=6 EndZ=0
    g8: LineSegment StartX=-2.4 StartY=6 StartZ=0 EndX=-2.4 EndY=0 EndZ=0
    g9: LineSegment StartX=-2.4 StartY=0 StartZ=0 EndX=0 EndY=0 EndZ=0
  constraints (29):
    c: Vertical(g0)
    c: Coincident(g1,g0)
    c: Horizontal(g1)
    c: Coincident(g2,g1)
    c: Vertical(g2)
    c: Coincident(g3,g2)
    c: Horizontal(g3)
    c: Coincident(g4,g3)
    c: Vertical(g4)
    c: Coincident(g5,g4)
    c: Horizontal(g5)
    c: Coincident(g6,g5)
    c: Vertical(g6)
    c: Coincident(g7,g6)
    c: Coincident(g8,g7)
    c: Vertical(g8)
    c: Coincident(g9,g8)
    c: Coincident(g9,g0)
    c: Horizontal(g9)
    c: DistanceY(g0,g0) = 24.671
    c: Horizontal(g7)
    c: DistanceY(g6,g6) = 4
    c: DistanceY(g4,g4) = 6
    c: DistanceX(g9,g9) = 2.4
    c: Coincident(g0,g-1)
    c: DistanceY(g-3,g7) = 0
    c: DistanceX(g8,g4) = 0
    c: DistanceX(g-3,g1) = 0
    c: DistanceX(g6,g-3) = 8
FEATURE [Part::Extrusion] Extrude010  label="Extrude buco frontale"
  Base = -> Sketch014
  Dir = (0,-1,2e-16)
  DirMode = 2
  FaceMakerClass = Part::FaceMakerBullseye
  FaceMakerMode = 3
  LengthFwd = 11.2
  LengthRev = 0
  Solid = true
  Symmetric = true
FEATURE [Sketcher::SketchObject] Sketch015  label="guida rail"
  ArcFitTolerance = 1e-06
  AttachmentSupport = -> [XZ_Plane]
  ExternalGeometry = -> [Sketch]
  FullyConstrained = true
  MakeInternals = false
  MapMode = 5
  Placement = pos=(0,0,0) rot=(1,0,0;1.5708rad)
  sketch-geometry (4):
    g0: LineSegment StartX=-100.8 StartY=43.2 StartZ=0 EndX=-44.6 EndY=43.2 EndZ=0
    g1: LineSegment StartX=-44.6 StartY=43.2 StartZ=0 EndX=-44.6 EndY=41.2 EndZ=0
    g2: LineSegment StartX=-44.6 StartY=41.2 StartZ=0 EndX=-100.8 EndY=41.2 EndZ=0
    g3: LineSegment StartX=-100.8 StartY=41.2 StartZ=0 EndX=-100.8 EndY=43.2 EndZ=0
  constraints (9):
    c: Horizontal(g0)
    c: Coincident(g1,g0)
    c: Coincident(g2,g1)
    c: Coincident(g3,g2)
    c: Coincident(g3,g0)
    c: Vertical(g3)
    c: Coincident(g2,g-3)
    c: Coincident(g1,g-3)
    c: Coincident(g0,g-4)
FEATURE [Part::Extrusion] Extrude011  label="Extrude guida rail"
  Base = -> Sketch015
  Dir = (0,-1,2e-16)
  DirMode = 2
  FaceMakerClass = Part::FaceMakerBullseye
  FaceMakerMode = 3
  LengthFwd = 9
  LengthRev = 0
  Solid = true
  Symmetric = true
FEATURE [Sketcher::SketchObject] Sketch016  label="guide per coperture laterali"
  ArcFitTolerance = 1e-06
  AttachmentSupport = -> [XZ_Plane]
  ExternalGeometry = -> [Sketch]
  FullyConstrained = true
  MakeInternals = false
  MapMode = 5
  Placement = pos=(0,0,0) rot=(1,0,0;1.5708rad)
  sketch-geometry (14):
    g0: Circle CenterX=-5.6 CenterY=7.6 CenterZ=0 NormalX=0 NormalY=0 NormalZ=1 AngleXU=0 Radius=1.6
    g1: Circle CenterX=-5.6 CenterY=7.6 CenterZ=0 NormalX=0 NormalY=0 NormalZ=1 AngleXU=0 Radius=4
    g2: Circle CenterX=-5.6 CenterY=34.8 CenterZ=0 NormalX=0 NormalY=0 NormalZ=1 AngleXU=0 Radius=1.6
    g3: Circle CenterX=-5.6 CenterY=34.8 CenterZ=0 NormalX=0 NormalY=0 NormalZ=1 AngleXU=0 Radius=4
    g4: Circle CenterX=-184.08 CenterY=34.8 CenterZ=0 NormalX=0 NormalY=0 NormalZ=1 AngleXU=0 Radius=1.6
    g5: Circle CenterX=-184.08 CenterY=34.8 CenterZ=0 NormalX=0 NormalY=0 NormalZ=1 AngleXU=0 Radius=4
    g6: Circle CenterX=-179.305 CenterY=-76.8316 CenterZ=0 NormalX=0 NormalY=0 NormalZ=1 AngleXU=0 Radius=1.6
    g7: Circle CenterX=-179.305 CenterY=-76.8316 CenterZ=0 NormalX=0 NormalY=0 NormalZ=1 AngleXU=0 Radius=4
    g8: Circle CenterX=-213.443 CenterY=-76.8316 CenterZ=0 NormalX=0 NormalY=0 NormalZ=1 AngleXU=0 Radius=1.6
    g9: Circle CenterX=-213.443 CenterY=-76.8316 CenterZ=0 NormalX=0 NormalY=0 NormalZ=1 AngleXU=0 Radius=4
    g10: Circle CenterX=-78.51 CenterY=7.6 CenterZ=0 NormalX=0 NormalY=0 NormalZ=1 AngleXU=0 Radius=1.6
    g11: Circle CenterX=-78.51 CenterY=7.6 CenterZ=0 NormalX=0 NormalY=0 NormalZ=1 AngleXU=0 Radius=4
    g12: Circle CenterX=-78.51 CenterY=34.8 CenterZ=0 NormalX=0 NormalY=0 NormalZ=1 AngleXU=0 Radius=1.6
    g13: Circle CenterX=-78.51 CenterY=34.8 CenterZ=0 NormalX=0 NormalY=0 NormalZ=1 AngleXU=0 Radius=4
  constraints (35):
    c: Diameter(g0) = 3.2
    c: Diameter(g1) = 8
    c: Coincident(g0,g1)
    c: Diameter(g2) = 3.2
    c: Diameter(g3) = 8
    c: Coincident(g3,g2)
    c: Tangent(g2,g-7)
    c: Diameter(g4) = 3.2
    c: Diameter(g5) = 8
    c: Coincident(g5,g4)
    c: Tangent(g4,g-7)
    c: Tangent(g4,g-8)
    c: Diameter(g6) = 3.2
    c: Diameter(g7) = 8
    c: Coincident(g7,g6)
    c: Tangent(g6,g-9)
    c: Tangent(g6,g-10)
    c: Diameter(g8) = 3.2
    c: Diameter(g9) = 8
    c: Coincident(g9,g8)
    c: Tangent(g8,g-10)
    c: Tangent(g8,g-11)
    c: Diameter(g10) = 3.2
    c: Diameter(g11) = 8
    c: Diameter(g12) = 3.2
    c: Diameter(g13) = 8
    c: Coincident(g12,g13)
    c: Coincident(g10,g11)
    c: Tangent(g12,g-7)
    c: DistanceX(g12,g10) = 0
    c: Tangent(g2,g-6)
    c: Tangent(g0,g-6)
    c: Tangent(g0,g-3)
    c: Tangent(g10,g-3)
    c: Tangent(g10,g-4)
FEATURE [Part::Extrusion] Extrude012  label="extrude guide per coperture laterali"
  Base = -> Sketch016
  Dir = (0,-1,2e-16)
  DirMode = 2
  FaceMakerClass = Part::FaceMakerBullseye
  FaceMakerMode = 3
  LengthFwd = 25.2
  LengthRev = 0
  Solid = true
  Symmetric = true
FEATURE [Sketcher::SketchObject] Sketch017  label="supporto CAM"
  ArcFitTolerance = 1e-06
  AttachmentSupport = -> [XZ_Plane]
  ExternalGeometry = -> [Sketch]
  FullyConstrained = true
  MakeInternals = false
  MapMode = 5
  Placement = pos=(0,0,0) rot=(1,0,0;1.5708rad)
  sketch-geometry (6):
    g0: LineSegment StartX=-2.4 StartY=48 StartZ=0 EndX=-2.4 EndY=41.2 EndZ=0
    g1: LineSegment StartX=-2.4 StartY=48 StartZ=0 EndX=-34 EndY=48 EndZ=0
    g2: LineSegment StartX=-34 StartY=48 StartZ=0 EndX=-34 EndY=46.72 EndZ=0
    g3: LineSegment StartX=-34 StartY=46.72 StartZ=0 EndX=-36 EndY=46.72 EndZ=0
    g4: LineSegment StartX=-36 StartY=46.72 StartZ=0 EndX=-36 EndY=41.2 EndZ=0
    g5: LineSegment StartX=-36 StartY=41.2 StartZ=0 EndX=-2.4 EndY=41.2 EndZ=0
  constraints (15):
    c: Coincident(g1,g0)
    c: Horizontal(g1)
    c: Coincident(g2,g1)
    c: Vertical(g2)
    c: Coincident(g3,g2)
    c: Horizontal(g3)
    c: Coincident(g4,g3)
    c: Coincident(g5,g4)
    c: DistanceX(g1,g0) = 31.6
    c: Coincident(g5,g0)
    c: Vertical(g4)
    c: DistanceY(g2,g1) = 1.28
    c: Coincident(g0,g-3)
    c: Coincident(g0,g-3)
    c: Coincident(g4,g-4)
FEATURE [Part::Extrusion] Extrude013  label="Extrude supporto CAM"
  Base = -> Sketch017
  Dir = (0,-1,2e-16)
  DirMode = 2
  FaceMakerClass = Part::FaceMakerBullseye
  FaceMakerMode = 3
  LengthFwd = 17.8
  LengthRev = 0
  Solid = true
  Symmetric = true
FEATURE [Sketcher::SketchObject] Sketch018  label="Scavo CAM"
  ArcFitTolerance = 1e-06
  AttachmentSupport = -> [YZ_Plane]
  ExternalGeometry = -> [Sketch]
  FullyConstrained = true
  MakeInternals = false
  MapMode = 5
  Placement = pos=(0,0,0) rot=(0.57735,0.57735,0.57735;2.0944rad)
  sketch-geometry (4):
    g0: LineSegment StartX=-7.73 StartY=48 StartZ=0 EndX=7.73 EndY=48 EndZ=0
    g1: LineSegment [constr] StartX=1.07e-14 StartY=48 StartZ=0 EndX=0 EndY=43.5155 EndZ=0
    g2: ArcOfCircle CenterX=9e-15 CenterY=52.42 CenterZ=0 NormalX=0 NormalY=0 NormalZ=1 AngleXU=0 Radius=8.90445 StartAngle=3.66102 EndAngle=5.76376
    g3: Circle [constr] CenterX=9e-15 CenterY=52.42 CenterZ=0 NormalX=0 NormalY=0 NormalZ=1 AngleXU=0 Radius=8.9
  constraints (13):
    c: Horizontal(g0)
    c: DistanceY(g-3,g0) = 0
    c: DistanceX(g0,g0) = 15.46
    c: DistanceX(g0,g-3) = 7.73
    c: DistanceX(g-3) = 0
    c: Coincident(g1,g-3)
    c: PointOnObject(g1,g-2)
    c: Coincident(g2,g0)
    c: Coincident(g2,g0)
    c: PointOnObject(g1,g2)
    c: Diameter(g3) = 17.8
    c: DistanceY(g1,g3) = 4.42
    c: Coincident(g2,g3)
FEATURE [Part::Extrusion] Extrude014  label="Extrude Scavo CAM"
  Base = -> Sketch018
  Dir = (1,0,0)
  DirMode = 2
  FaceMakerClass = Part::FaceMakerBullseye
  FaceMakerMode = 3
  LengthFwd = -34
  LengthRev = 0
  Solid = true
  Symmetric = false
FEATURE [Sketcher::SketchObject] Sketch019  label="scavo rumble"
  ArcFitTolerance = 1e-06
  AttachmentSupport = -> [XZ_Plane]
  ExternalGeometry = -> [Sketch]
  FullyConstrained = true
  MakeInternals = false
  MapMode = 5
  Placement = pos=(0,0,0) rot=(1,0,0;1.5708rad)
  sketch-geometry (6):
    g0: LineSegment StartX=-164.575 StartY=-24.3786 StartZ=0 EndX=-159.439 EndY=-26.0473 EndZ=0
    g1: LineSegment StartX=-159.439 StartY=-26.0473 StartZ=0 EndX=-166.547 EndY=-47.9216 EndZ=0
    g2: LineSegment StartX=-166.547 StartY=-47.9216 StartZ=0 EndX=-171.682 EndY=-46.2529 EndZ=0
    g3: LineSegment StartX=-171.682 StartY=-46.2529 StartZ=0 EndX=-164.575 EndY=-24.3786 EndZ=0
    g4: LineSegment [constr] StartX=-145.51 StartY=22 StartZ=0 EndX=-160.961 EndY=-25.5528 EndZ=0
    g5: LineSegment [constr] StartX=-159.439 StartY=-26.0473 StartZ=0 EndX=-160.961 EndY=-25.5528 EndZ=0
  constraints (17):
    c: Coincident(g1,g0)
    c: Coincident(g2,g1)
    c: Coincident(g3,g2)
    c: Coincident(g3,g0)
    c: Parallel(g3,g-3)
    c: Parallel(g3,g1)
    c: Perpendicular(g3,g0)
    c: Perpendicular(g2,g3)
    c: Distance(g2,g0) = 23
    c: Parallel(g4,g-3)
    c: Distance(g4) = 50
    c: Coincident(g4,g-3)
    c: Parallel(g5,g0)
    c: Distance(g5) = 1.6
    c: Coincident(g5,g0)
    c: Distance(g5,g0) = 3.8
    c: Coincident(g5,g4)
FEATURE [Part::Extrusion] Extrude015  label="scavo rumble001"
  Base = -> Sketch019
  Dir = (0,-1,2e-16)
  DirMode = 2
  FaceMakerClass = Part::FaceMakerBullseye
  FaceMakerMode = 3
  LengthFwd = 21
  LengthRev = 0
  Solid = true
  Symmetric = true
FEATURE [Sketcher::SketchObject] Sketch020  label="fermo rumble"
  ArcFitTolerance = 1e-06
  AttachmentSupport = -> [XZ_Plane]
  ExternalGeometry = -> [Sketch019,Sketch]
  FullyConstrained = true
  MakeInternals = false
  MapMode = 5
  Placement = pos=(0,0,0) rot=(1,0,0;1.5708rad)
  sketch-geometry (16):
    g0: LineSegment [constr] StartX=-166.709 StartY=-43.2425 StartZ=0 EndX=-168.068 EndY=-47.4271 EndZ=0
    g1: LineSegment [constr] StartX=-168.068 StartY=-47.4271 StartZ=0 EndX=-166.547 EndY=-47.9216 EndZ=0
    g2: LineSegment StartX=-168.121 StartY=-40.4703 StartZ=0 EndX=-166.029 EndY=-41.1502 EndZ=0
    g3: LineSegment StartX=-166.029 StartY=-41.1502 StartZ=0 EndX=-166.709 EndY=-43.2425 EndZ=0
    g4: LineSegment StartX=-166.709 StartY=-43.2425 StartZ=0 EndX=-168.801 EndY=-42.5626 EndZ=0
    g5: LineSegment StartX=-168.801 StartY=-42.5626 StartZ=0 EndX=-168.121 EndY=-40.4703 EndZ=0
    g6: LineSegment StartX=-167.627 StartY=-38.9486 StartZ=0 EndX=-164.203 EndY=-40.0611 EndZ=0
    g7: LineSegment StartX=-164.203 StartY=-40.0611 StartZ=0 EndX=-165.81 EndY=-45.0066 EndZ=0
    g8: LineSegment StartX=-165.81 StartY=-45.0066 StartZ=0 EndX=-169.234 EndY=-43.8941 EndZ=0
    g9: LineSegment StartX=-170.261 StartY=-41.878 StartZ=0 EndX=-169.643 EndY=-39.9759 EndZ=0
    g10: LineSegment [constr] StartX=-169.643 StartY=-39.9759 StartZ=0 EndX=-169.148 EndY=-38.4542 EndZ=0
    g11: LineSegment [constr] StartX=-169.148 StartY=-38.4542 StartZ=0 EndX=-167.627 EndY=-38.9486 EndZ=0
    g12: ArcOfCircle CenterX=-168.739 CenterY=-42.3724 CenterZ=0 NormalX=0 NormalY=0 NormalZ=1 AngleXU=0 Radius=1.6 StartAngle=2.82743 EndAngle=4.39823
    g13: GeomPoint [constr] X=-170.755 Y=-43.3997 Z=0
    g14: ArcOfCircle CenterX=-168.121 CenterY=-40.4703 CenterZ=0 NormalX=0 NormalY=0 NormalZ=1 AngleXU=0 Radius=1.6 StartAngle=1.25664 EndAngle=2.82743
    g15: GeomPoint [constr] X=-169.148 Y=-38.4542 Z=0
  constraints (42):
    c: Parallel(g0,g-4)
    c: Distance(g0) = 4.4
    c: Coincident(g1,g0)
    c: Perpendicular(g0,g1)
    c: Distance(g1) = 1.6
    c: Coincident(g1,g-5)
    c: Coincident(g3,g2)
    c: Coincident(g4,g3)
    c: Coincident(g5,g4)
    c: Coincident(g5,g2)
    c: Parallel(g3,g-4)
    c: Parallel(g3,g5)
    c: Perpendicular(g2,g3)
    c: Parallel(g4,g2)
    c: Distance(g2) = 2.2
    c: Distance(g3) = 2.2
    c: Coincident(g7,g6)
    c: Coincident(g8,g7)
    c: Parallel(g7,g-4)
    c: Parallel(g7,g9)
    c: Perpendicular(g6,g7)
    c: Parallel(g6,g8)
    c: Distance(g6,g15) = 5.2
    c: Distance(g7) = 5.2
    c: Coincident(g11,g10)
    c: Parallel(g10,g9)
    c: Parallel(g11,g6)
    c: Distance(g10) = 1.6
    c: Distance(g11) = 1.6
    c: Coincident(g10,g15)
    c: Distance(g11,g2) = 1.6
    c: Distance(g2,g10) = 1.6
    c: PointOnObject(g13,g8)
    c: PointOnObject(g13,g9)
    c: Tangent(g8,g12) = 1.5708
    c: Tangent(g9,g12) = 1.5708
    c: PointOnObject(g15,g9)
    c: Tangent(g6,g14) = 1.5708
    c: Tangent(g9,g14) = 1.5708
    c: Equal(g12,g14)
    c: Coincident(g6,g11)
    c: Coincident(g3,g0)
FEATURE [Part::Extrusion] Extrude016  label="Extrude fermo rumble"
  Base = -> Sketch020
  Dir = (0,-1,2e-16)
  DirMode = 2
  FaceMakerClass = Part::FaceMakerBullseye
  FaceMakerMode = 3
  LengthFwd = 25.2
  LengthRev = 0
  Solid = true
  Symmetric = true
FEATURE [Sketcher::SketchObject] Sketch021  label="perno fermo rumble001"
  ArcFitTolerance = 1e-06
  AttachmentSupport = -> [XZ_Plane001]
  FullyConstrained = true
  MakeInternals = false
  MapMode = 5
  Placement = pos=(0,0,0) rot=(1,0,0;1.5708rad)
  sketch-geometry (16):
    g0: LineSegment StartX=0 StartY=0.45 StartZ=0 EndX=0 EndY=1.55 EndZ=0
    g1: LineSegment StartX=0.45 StartY=2 StartZ=0 EndX=1.55 EndY=2 EndZ=0
    g2: LineSegment StartX=2 StartY=1.55 StartZ=0 EndX=2 EndY=0.45 EndZ=0
    g3: LineSegment StartX=1.55 StartY=0 StartZ=0 EndX=0.45 EndY=0 EndZ=0
    g4: ArcOfCircle [constr] CenterX=0.45 CenterY=1.55 CenterZ=0 NormalX=0 NormalY=0 NormalZ=1 AngleXU=0 Radius=0.45 StartAngle=1.5708 EndAngle=3.14159
    g5: GeomPoint [constr] X=0 Y=2 Z=0
    g6: LineSegment StartX=0.45 StartY=2 StartZ=0 EndX=0 EndY=1.55 EndZ=0
    g7: ArcOfCircle [constr] CenterX=1.55 CenterY=1.55 CenterZ=0 NormalX=0 NormalY=0 NormalZ=1 AngleXU=0 Radius=0.45 StartAngle=0 EndAngle=1.5708
    g8: GeomPoint [constr] X=2 Y=2 Z=0
    g9: LineSegment StartX=2 StartY=1.55 StartZ=0 EndX=1.55 EndY=2 EndZ=0
    g10: ArcOfCircle [constr] CenterX=1.55 CenterY=0.45 CenterZ=0 NormalX=0 NormalY=0 NormalZ=1 AngleXU=0 Radius=0.45 StartAngle=4.71239 EndAngle=6.28319
    g11: GeomPoint [constr] X=2 Y=0 Z=0
    g12: LineSegment StartX=1.55 StartY=0 StartZ=0 EndX=2 EndY=0.45 EndZ=0
    g13: ArcOfCircle [constr] CenterX=0.45 CenterY=0.45 CenterZ=0 NormalX=0 NormalY=0 NormalZ=1 AngleXU=0 Radius=0.45 StartAngle=3.14159 EndAngle=4.71239
    g14: GeomPoint [constr] X=0 Y=0 Z=0
    g15: LineSegment StartX=0 StartY=0.45 StartZ=0 EndX=0.45 EndY=0 EndZ=0
  constraints (35):
    c: Coincident(g14,g-1)
    c: PointOnObject(g5,g-2)
    c: Horizontal(g1)
    c: Vertical(g2)
    c: Horizontal(g3)
    c: DistanceX(g5,g8) = 2
    c: DistanceY(g11,g8) = 2
    c: PointOnObject(g5,g0)
    c: PointOnObject(g5,g1)
    c: Tangent(g0,g4) = 1.5708
    c: Tangent(g1,g4) = 1.5708
    c: Coincident(g6,g0)
    c: Coincident(g6,g1)
    c: PointOnObject(g8,g2)
    c: PointOnObject(g8,g1)
    c: Tangent(g2,g7) = 1.5708
    c: Tangent(g1,g7) = 1.5708
    c: Coincident(g9,g2)
    c: Coincident(g9,g1)
    c: PointOnObject(g11,g2)
    c: PointOnObject(g11,g3)
    c: Tangent(g2,g10) = 1.5708
    c: Tangent(g3,g10) = 1.5708
    c: Coincident(g12,g2)
    c: Coincident(g12,g3)
    c: PointOnObject(g14,g0)
    c: PointOnObject(g14,g3)
    c: Tangent(g0,g13) = 1.5708
    c: Tangent(g3,g13) = 1.5708
    c: Coincident(g15,g0)
    c: Coincident(g15,g3)
    c: Equal(g6,g9)
    c: Equal(g9,g12)
    c: Equal(g12,g15)
    c: DistanceX(g14,g3) = 0.45
FEATURE [Part::Extrusion] Extrude017  label="Extrude perno fermo rumble"
  Base = -> Sketch021
  Dir = (0,-1,2e-16)
  DirMode = 2
  FaceMakerClass = Part::FaceMakerBullseye
  FaceMakerMode = 3
  LengthFwd = 25.2
  LengthRev = 0
  Solid = true
  Symmetric = true
FEATURE [Sketcher::SketchObject] Sketch022  label="fori per M3x5(OD)x6(L)"
  ArcFitTolerance = 1e-06
  AttachmentSupport = -> [XZ_Plane]
  ExternalGeometry = -> [Sketch016]
  FullyConstrained = true
  MakeInternals = false
  MapMode = 5
  Placement = pos=(0,0,0) rot=(1,0,0;1.5708rad)
  sketch-geometry (7):
    g0: Circle CenterX=-5.6 CenterY=34.8 CenterZ=0 NormalX=0 NormalY=0 NormalZ=1 AngleXU=0 Radius=2.5
    g1: Circle CenterX=-5.6 CenterY=7.6 CenterZ=0 NormalX=0 NormalY=0 NormalZ=1 AngleXU=0 Radius=2.5
    g2: Circle CenterX=-78.51 CenterY=34.8 CenterZ=0 NormalX=0 NormalY=0 NormalZ=1 AngleXU=0 Radius=2.5
    g3: Circle CenterX=-78.51 CenterY=7.6 CenterZ=0 NormalX=0 NormalY=0 NormalZ=1 AngleXU=0 Radius=2.5
    g4: Circle CenterX=-184.08 CenterY=34.8 CenterZ=0 NormalX=0 NormalY=0 NormalZ=1 AngleXU=0 Radius=2.5
    g5: Circle CenterX=-179.305 CenterY=-76.8316 CenterZ=0 NormalX=0 NormalY=0 NormalZ=1 AngleXU=0 Radius=2.5
    g6: Circle CenterX=-213.443 CenterY=-76.8316 CenterZ=0 NormalX=0 NormalY=0 NormalZ=1 AngleXU=0 Radius=2.5
  constraints (14):
    c: Diameter(g0) = 5
    c: Diameter(g1) = 5
    c: Diameter(g2) = 5
    c: Diameter(g3) = 5
    c: Diameter(g4) = 5
    c: Diameter(g5) = 5
    c: Diameter(g6) = 5
    c: Coincident(g0,g-8)
    c: Coincident(g1,g-9)
    c: Coincident(g2,g-6)
    c: Coincident(g3,g-7)
    c: Coincident(g4,g-5)
    c: Coincident(g5,g-4)
    c: Coincident(g6,g-3)
FEATURE [Part::Extrusion] Extrude018  label="Extrude fori M3x5x6 - dx"
  Base = -> Sketch022
  Dir = (0,-1,2e-16)
  DirMode = 2
  FaceMakerClass = Part::FaceMakerBullseye
  FaceMakerMode = 3
  LengthFwd = 6.2
  LengthRev = 0
  Placement = pos=(0,-9.5,0) rot=(0,0,1;0rad)
  Solid = true
  Symmetric = true
FEATURE [Part::Extrusion] Extrude019  label="Extrude fori M3x5x6 - sx"
  Base = -> Sketch022
  Dir = (0,-1,2e-16)
  DirMode = 2
  FaceMakerClass = Part::FaceMakerBullseye
  FaceMakerMode = 3
  LengthFwd = 6.2
  LengthRev = 0
  Placement = pos=(0,9.5,0) rot=(0,0,1;0rad)
  Solid = true
  Symmetric = true
FEATURE [Sketcher::SketchObject] Sketch023  label="foro anteriore M3x5x6"
  ArcFitTolerance = 1e-06
  AttachmentSupport = -> [YZ_Plane]
  FullyConstrained = true
  MakeInternals = false
  MapMode = 5
  Placement = pos=(0,0,0) rot=(0.57735,0.57735,0.57735;2.0944rad)
  sketch-geometry (2):
    g0: LineSegment [constr] StartX=0 StartY=0 StartZ=0 EndX=0 EndY=38.6 EndZ=0
    g1: Circle CenterX=0 CenterY=38.6 CenterZ=0 NormalX=0 NormalY=0 NormalZ=1 AngleXU=0 Radius=2.5
  constraints (5):
    c: Coincident(g0,g-1)
    c: PointOnObject(g0,g-2)
    c: DistanceY(g0,g0) = 38.6
    c: Diameter(g1) = 5
    c: Coincident(g1,g0)
FEATURE [Part::Extrusion] Extrude020  label="Extrude foro anteriore M3x5x6"
  Base = -> Sketch023
  Dir = (1,0,0)
  DirMode = 2
  FaceMakerClass = Part::FaceMakerBullseye
  FaceMakerMode = 3
  LengthFwd = -6.2
  LengthRev = 0
  Solid = true
  Symmetric = false
FEATURE [Sketcher::SketchObject] Sketch024  label="fori per viti frontale"
  ArcFitTolerance = 1e-06
  AttachmentSupport = -> [YZ_Plane]
  FullyConstrained = true
  MakeInternals = false
  MapMode = 5
  Placement = pos=(0,0,0) rot=(0.57735,0.57735,0.57735;2.0944rad)
  sketch-geometry (9):
    g0: LineSegment [constr] StartX=-10.3 StartY=30.721 StartZ=0 EndX=10.3 EndY=30.721 EndZ=0
    g1: LineSegment [constr] StartX=10.3 StartY=30.721 StartZ=0 EndX=10.3 EndY=10.121 EndZ=0
    g2: LineSegment [constr] StartX=10.3 StartY=10.121 StartZ=0 EndX=-10.3 EndY=10.121 EndZ=0
    g3: LineSegment [constr] StartX=-10.3 StartY=10.121 StartZ=0 EndX=-10.3 EndY=30.721 EndZ=0
    g4: LineSegment [constr] StartX=0 StartY=0 StartZ=0 EndX=0 EndY=10.121 EndZ=0
    g5: Circle CenterX=-10.3 CenterY=30.721 CenterZ=0 NormalX=0 NormalY=0 NormalZ=1 AngleXU=0 Radius=2
    g6: Circle CenterX=10.3 CenterY=30.721 CenterZ=0 NormalX=0 NormalY=0 NormalZ=1 AngleXU=0 Radius=2
    g7: Circle CenterX=-10.3 CenterY=10.121 CenterZ=0 NormalX=0 NormalY=0 NormalZ=1 AngleXU=0 Radius=2
    g8: Circle CenterX=10.3 CenterY=10.121 CenterZ=0 NormalX=0 NormalY=0 NormalZ=1 AngleXU=0 Radius=2
  constraints (22):
    c: Horizontal(g0)
    c: Coincident(g1,g0)
    c: Vertical(g1)
    c: Coincident(g2,g1)
    c: Horizontal(g2)
    c: Coincident(g3,g2)
    c: Coincident(g3,g0)
    c: Vertical(g3)
    c: DistanceX(g0,g0) = 20.6
    c: DistanceY(g3,g3) = 20.6
    c: Coincident(g4,g-1)
    c: PointOnObject(g4,g-2)
    c: DistanceY(g4,g4) = 10.121
    c: Symmetric(g2,g2,g4)
    c: Diameter(g5) = 4
    c: Diameter(g6) = 4
    c: Diameter(g7) = 4
    c: Diameter(g8) = 4
    c: Coincident(g5,g0)
    c: Coincident(g6,g0)
    c: Coincident(g7,g2)
    c: Coincident(g8,g1)
FEATURE [Part::Extrusion] Extrude021  label="Extrude fori per viti frontale"
  Base = -> Sketch024
  Dir = (1,0,0)
  DirMode = 2
  FaceMakerClass = Part::FaceMakerBullseye
  FaceMakerMode = 3
  LengthFwd = -2.4
  LengthRev = 0
  Solid = true
  Symmetric = false
FEATURE [Sketcher::SketchObject] Sketch025  label="foro per filo CAM"
  ArcFitTolerance = 1e-06
  AttachmentSupport = -> [XZ_Plane]
  ExternalGeometry = -> [Sketch]
  FullyConstrained = true
  MakeInternals = false
  MapMode = 5
  Placement = pos=(0,0,0) rot=(1,0,0;1.5708rad)
  sketch-geometry (4):
    g0: LineSegment StartX=-44.6 StartY=41.2 StartZ=0 EndX=-44.6 EndY=36.4 EndZ=0
    g1: LineSegment StartX=-44.6 StartY=36.4 StartZ=0 EndX=-54.6 EndY=36.4 EndZ=0
    g2: LineSegment StartX=-54.6 StartY=36.4 StartZ=0 EndX=-50.4 EndY=41.2 EndZ=0
    g3: LineSegment StartX=-50.4 StartY=41.2 StartZ=0 EndX=-44.6 EndY=41.2 EndZ=0
  constraints (11):
    c: Vertical(g0)
    c: Coincident(g1,g0)
    c: Horizontal(g1)
    c: Coincident(g2,g1)
    c: Coincident(g3,g2)
    c: Coincident(g3,g0)
    c: Horizontal(g3)
    c: Coincident(g0,g-3)
    c: DistanceY(g0,g-4) = 0
    c: DistanceX(g3,g3) = 5.8
    c: DistanceX(g1,g1) = 10
FEATURE [Part::Extrusion] Extrude022  label="Extrude foro per filo CAM dx"
  Base = -> Sketch025
  Dir = (0,-1,2e-16)
  DirMode = 2
  FaceMakerClass = Part::FaceMakerBullseye
  FaceMakerMode = 3
  LengthFwd = 4.9
  LengthRev = 0
  Placement = pos=(0,6.95,0) rot=(0,0,1;0rad)
  Solid = true
  Symmetric = true
FEATURE [Part::Extrusion] Extrude023  label="Extrude foro per filo CAM sx"
  Base = -> Sketch025
  Dir = (0,-1,2e-16)
  DirMode = 2
  FaceMakerClass = Part::FaceMakerBullseye
  FaceMakerMode = 3
  LengthFwd = 4.9
  LengthRev = 0
  Placement = pos=(0,-6.95,0) rot=(0,0,1;0rad)
  Solid = true
  Symmetric = true
FEATURE [Sketcher::SketchObject] Sketch026  label="foro sotto anteriore M3x5x6"
  ArcFitTolerance = 1e-06
  AttachmentSupport = -> [XY_Plane]
  FullyConstrained = true
  MakeInternals = false
  MapMode = 5
  sketch-geometry (2):
    g0: LineSegment [constr] StartX=0 StartY=0 StartZ=0 EndX=-16.5 EndY=0 EndZ=0
    g1: Circle CenterX=-16.5 CenterY=0 CenterZ=0 NormalX=0 NormalY=0 NormalZ=1 AngleXU=0 Radius=2.5
  constraints (5):
    c: Distance(g0) = 16.5
    c: Coincident(g0,g-1)
    c: PointOnObject(g0,g-1)
    c: Diameter(g1) = 5
    c: Coincident(g0,g1)
FEATURE [Sketcher::SketchObject] Sketch027  label="foro sotto posteriore M3x5x6"
  ArcFitTolerance = 1e-06
  AttachmentSupport = -> [XY_Plane]
  ExternalGeometry = -> [Sketch]
  FullyConstrained = true
  MakeInternals = false
  MapMode = 5
  sketch-geometry (2):
    g0: LineSegment [constr] StartX=-82.8 StartY=2e-16 StartZ=0 EndX=-71.3 EndY=2e-16 EndZ=0
    g1: Circle CenterX=-71.3 CenterY=2e-16 CenterZ=0 NormalX=0 NormalY=0 NormalZ=1 AngleXU=0 Radius=2.5
  constraints (5):
    c: Distance(g0) = 11.5
    c: Coincident(g0,g-3)
    c: PointOnObject(g0,g-3)
    c: Diameter(g1) = 5
    c: Coincident(g1,g0)
FEATURE [Sketcher::SketchObject] Sketch029  label="fori sotto impugnatura"
  ArcFitTolerance = 1e-06
  AttachmentSupport = -> [XY_Plane]
  ExternalGeometry = -> [Sketch]
  FullyConstrained = true
  MakeInternals = false
  MapMode = 5
  sketch-geometry (15):
    g0: LineSegment [constr] StartX=-175.232 StartY=-1.83e-14 StartZ=0 EndX=-191.232 EndY=0 EndZ=0
    g1: Circle CenterX=-191.232 CenterY=0 CenterZ=0 NormalX=0 NormalY=0 NormalZ=1 AngleXU=0 Radius=3.95
    g2: LineSegment [constr] StartX=-175.232 StartY=-1.83e-14 StartZ=0 EndX=-204.275 EndY=0 EndZ=0
    g3: LineSegment StartX=-204.275 StartY=3.525 StartZ=0 EndX=-204.275 EndY=-3.525 EndZ=0
    g4: LineSegment StartX=-205.4 StartY=-4.65 StartZ=0 EndX=-206.65 EndY=-4.65 EndZ=0
    g5: LineSegment StartX=-207.775 StartY=-3.525 StartZ=0 EndX=-207.775 EndY=3.525 EndZ=0
    g6: LineSegment StartX=-206.65 StartY=4.65 StartZ=0 EndX=-205.4 EndY=4.65 EndZ=0
    g7: ArcOfCircle CenterX=-206.65 CenterY=3.525 CenterZ=0 NormalX=0 NormalY=0 NormalZ=1 AngleXU=0 Radius=1.125 StartAngle=1.5708 EndAngle=3.14159
    g8: GeomPoint [constr] X=-207.775 Y=4.65 Z=0
    g9: ArcOfCircle CenterX=-205.4 CenterY=3.525 CenterZ=0 NormalX=0 NormalY=0 NormalZ=1 AngleXU=0 Radius=1.125 StartAngle=0 EndAngle=1.5708
    g10: GeomPoint [constr] X=-204.275 Y=4.65 Z=0
    g11: ArcOfCircle CenterX=-205.4 CenterY=-3.525 CenterZ=0 NormalX=0 NormalY=0 NormalZ=1 AngleXU=0 Radius=1.125 StartAngle=4.71239 EndAngle=6.28319
    g12: GeomPoint [constr] X=-204.275 Y=-4.65 Z=0
    g13: ArcOfCircle CenterX=-206.65 CenterY=-3.525 CenterZ=0 NormalX=0 NormalY=0 NormalZ=1 AngleXU=0 Radius=1.125 StartAngle=3.14159 EndAngle=4.71239
    g14: GeomPoint [constr] X=-207.775 Y=-4.65 Z=0
  constraints (35):
    c: Distance(g0) = 16
    c: Coincident(g0,g-3)
    c: PointOnObject(g0,g-1)
    c: Diameter(g1) = 7.9
    c: Coincident(g1,g0)
    c: Coincident(g2,g0)
    c: PointOnObject(g2,g-1)
    c: Vertical(g3)
    c: Horizontal(g4)
    c: Vertical(g5)
    c: Horizontal(g6)
    c: DistanceY(g12,g10) = 9.3
    c: DistanceX(g8,g10) = 3.5
    c: Symmetric(g10,g12,g2)
    c: PointOnObject(g8,g5)
    c: PointOnObject(g8,g6)
    c: Tangent(g5,g7) = 1.5708
    c: Tangent(g6,g7) = 1.5708
    c: PointOnObject(g10,g3)
    c: PointOnObject(g10,g6)
    c: Tangent(g3,g9) = 1.5708
    c: Tangent(g6,g9) = 1.5708
    c: PointOnObject(g12,g3)
    c: PointOnObject(g12,g4)
    c: Tangent(g3,g11) = 1.5708
    c: Tangent(g4,g11) = 1.5708
    c: PointOnObject(g14,g4)
    c: PointOnObject(g14,g5)
    c: Tangent(g4,g13) = 1.5708
    c: Tangent(g5,g13) = 1.5708
    c: Equal(g7,g9)
    c: Equal(g9,g11)
    c: Equal(g11,g13)
    c: DistanceX(g6,g6) = 1.25
    c: DistanceX(g-5,g5) = 6.8
FEATURE [Sketcher::SketchObject] Sketch030  label="fori superiori per solenoide e oled"
  ArcFitTolerance = 1e-06
  AttachmentSupport = -> [XY_Plane]
  ExternalGeometry = -> [Sketch]
  FullyConstrained = true
  MakeInternals = false
  MapMode = 5
  sketch-geometry (33):
    g0: LineSegment [constr] StartX=-181.6 StartY=1.12e-14 StartZ=0 EndX=-169.91 EndY=0 EndZ=0
    g1: LineSegment [constr] StartX=-169.91 StartY=0 StartZ=0 EndX=-169.91 EndY=-2.6 EndZ=0
    g2: LineSegment [constr] StartX=-169.91 StartY=0 StartZ=0 EndX=-169.91 EndY=2.6 EndZ=0
    g3: LineSegment StartX=-169.91 StartY=4.975 StartZ=0 EndX=-169.91 EndY=8.225 EndZ=0
    g4: LineSegment StartX=-167.535 StartY=10.6 StartZ=0 EndX=-167.285 EndY=10.6 EndZ=0
    g5: LineSegment StartX=-164.91 StartY=8.225 StartZ=0 EndX=-164.91 EndY=4.975 EndZ=0
    g6: LineSegment StartX=-167.285 StartY=2.6 StartZ=0 EndX=-167.535 EndY=2.6 EndZ=0
    g7: LineSegment StartX=-169.91 StartY=-4.975 StartZ=0 EndX=-169.91 EndY=-8.225 EndZ=0
    g8: LineSegment StartX=-167.535 StartY=-10.6 StartZ=0 EndX=-167.285 EndY=-10.6 EndZ=0
    g9: LineSegment StartX=-164.91 StartY=-8.225 StartZ=0 EndX=-164.91 EndY=-4.975 EndZ=0
    g10: LineSegment StartX=-167.285 StartY=-2.6 StartZ=0 EndX=-167.535 EndY=-2.6 EndZ=0
    g11: ArcOfCircle CenterX=-167.535 CenterY=8.225 CenterZ=0 NormalX=0 NormalY=0 NormalZ=1 AngleXU=0 Radius=2.375 StartAngle=1.5708 EndAngle=3.14159
    g12: GeomPoint [constr] X=-169.91 Y=10.6 Z=0
    g13: ArcOfCircle CenterX=-167.285 CenterY=8.225 CenterZ=0 NormalX=0 NormalY=0 NormalZ=1 AngleXU=0 Radius=2.375 StartAngle=0 EndAngle=1.5708
    g14: GeomPoint [constr] X=-164.91 Y=10.6 Z=0
    g15: ArcOfCircle CenterX=-167.285 CenterY=4.975 CenterZ=0 NormalX=0 NormalY=0 NormalZ=1 AngleXU=0 Radius=2.375 StartAngle=4.71239 EndAngle=6.28319
    g16: GeomPoint [constr] X=-164.91 Y=2.6 Z=0
    g17: ArcOfCircle CenterX=-167.535 CenterY=4.975 CenterZ=0 NormalX=0 NormalY=0 NormalZ=1 AngleXU=0 Radius=2.375 StartAngle=3.14159 EndAngle=4.71239
    g18: GeomPoint [constr] X=-169.91 Y=2.6 Z=0
    g19: ArcOfCircle CenterX=-167.535 CenterY=-4.975 CenterZ=0 NormalX=0 NormalY=0 NormalZ=1 AngleXU=0 Radius=2.375 StartAngle=1.5708 EndAngle=3.14159
    g20: GeomPoint [constr] X=-169.91 Y=-2.6 Z=0
    g21: ArcOfCircle CenterX=-167.285 CenterY=-4.975 CenterZ=0 NormalX=0 NormalY=0 NormalZ=1 AngleXU=0 Radius=2.375 StartAngle=0 EndAngle=1.5708
    g22: GeomPoint [constr] X=-164.91 Y=-2.6 Z=0
    g23: ArcOfCircle CenterX=-167.285 CenterY=-8.225 CenterZ=0 NormalX=0 NormalY=0 NormalZ=1 AngleXU=0 Radius=2.375 StartAngle=4.71239 EndAngle=6.28319
    g24: GeomPoint [constr] X=-164.91 Y=-10.6 Z=0
    g25: ArcOfCircle CenterX=-167.535 CenterY=-8.225 CenterZ=0 NormalX=0 NormalY=0 NormalZ=1 AngleXU=0 Radius=2.375 StartAngle=3.14159 EndAngle=4.71239
    g26: GeomPoint [constr] X=-169.91 Y=-10.6 Z=0
    g27: LineSegment [constr] StartX=-181.6 StartY=1.12e-14 StartZ=0 EndX=-152.209 EndY=0 EndZ=0
    g28: LineSegment [constr] StartX=-181.6 StartY=1.12e-14 StartZ=0 EndX=-130.41 EndY=0 EndZ=0
    g29: LineSegment [constr] StartX=-152.209 StartY=0 StartZ=0 EndX=-152.209 EndY=6.95 EndZ=0
    g30: LineSegment [constr] StartX=-130.41 StartY=0 StartZ=0 EndX=-130.41 EndY=-6.95 EndZ=0
    g31: Circle CenterX=-152.209 CenterY=6.95 CenterZ=0 NormalX=0 NormalY=0 NormalZ=1 AngleXU=0 Radius=2.1
    g32: Circle CenterX=-130.41 CenterY=-6.95 CenterZ=0 NormalX=0 NormalY=0 NormalZ=1 AngleXU=0 Radius=2.1
  constraints (79):
    c: Distance(g0) = 11.69
    c: PointOnObject(g0,g-1)
    c: Coincident(g-4,g0)
    c: Distance(g1) = 2.6
    c: Coincident(g1,g0)
    c: Vertical(g1)
    c: Distance(g2) = 2.6
    c: Coincident(g2,g0)
    c: Vertical(g2)
    c: Distance(g18,g12) = 8
    c: Coincident(g18,g2)
    c: Vertical(g3)
    c: Distance(g14,g12) = 5
    c: Horizontal(g4)
    c: Distance(g16,g14) = 8
    c: Vertical(g5)
    c: Distance(g26,g20) = 8
    c: Coincident(g20,g1)
    c: Vertical(g7)
    c: Distance(g26,g24) = 5
    c: Horizontal(g8)
    c: Distance(g24,g22) = 8
    c: Vertical(g9)
    c: PointOnObject(g12,g3)
    c: PointOnObject(g12,g4)
    c: Tangent(g3,g11) = 1.5708
    c: Tangent(g4,g11) = 1.5708
    c: PointOnObject(g14,g5)
    c: PointOnObject(g14,g4)
    c: Tangent(g5,g13) = 1.5708
    c: Tangent(g4,g13) = 1.5708
    c: PointOnObject(g16,g5)
    c: PointOnObject(g16,g6)
    c: Tangent(g5,g15) = 1.5708
    c: Tangent(g6,g15) = 1.5708
    c: PointOnObject(g18,g3)
    c: PointOnObject(g18,g6)
    c: Tangent(g3,g17) = 1.5708
    c: Tangent(g6,g17) = 1.5708
    c: Equal(g11,g13)
    c: Equal(g13,g15)
    c: Equal(g15,g17)
    c: DistanceX(g4,g4) = 0.25
    c: PointOnObject(g20,g7)
    c: PointOnObject(g20,g10)
    c: Tangent(g7,g19) = -1.5708
    c: Tangent(g10,g19) = -1.5708
    c: PointOnObject(g22,g9)
    c: PointOnObject(g22,g10)
    c: Tangent(g9,g21) = -1.5708
    c: Tangent(g10,g21) = -1.5708
    c: PointOnObject(g24,g9)
    c: PointOnObject(g24,g8)
    c: Tangent(g9,g23) = -1.5708
    c: Tangent(g8,g23) = -1.5708
    c: PointOnObject(g26,g8)
    c: PointOnObject(g26,g7)
    c: Tangent(g8,g25) = -1.5708
    c: Tangent(g7,g25) = -1.5708
    c: Equal(g19,g21)
    c: Equal(g21,g23)
    c: Equal(g23,g25)
    c: DistanceX(g10,g10) = 0.25
    c: Distance(g27) = 29.391
    c: Coincident(g27,g0)
    c: PointOnObject(g27,g-1)
    c: Distance(g28) = 51.19
    c: Coincident(g28,g0)
    c: PointOnObject(g28,g-1)
    c: Distance(g29) = 6.95
    c: Coincident(g29,g27)
    c: Vertical(g29)
    c: Distance(g30) = 6.95
    c: Coincident(g30,g28)
    c: Vertical(g30)
    c: Diameter(g31) = 4.2
    c: Diameter(g32) = 4.2
    c: Coincident(g32,g30)
    c: Coincident(g31,g29)
FEATURE [Sketcher::SketchObject] Sketch031  label="fori inferiori switch pompa"
  ArcFitTolerance = 1e-06
  AttachmentSupport = -> [XY_Plane]
  ExternalGeometry = -> [Sketch]
  FullyConstrained = true
  MakeInternals = false
  MapMode = 5
  sketch-geometry (4):
    g0: LineSegment [constr] StartX=-57.2 StartY=1.9e-15 StartZ=0 EndX=-62.45 EndY=1.9e-15 EndZ=0
    g1: LineSegment [constr] StartX=-62.45 StartY=3.25 StartZ=0 EndX=-62.45 EndY=-3.25 EndZ=0
    g2: Circle CenterX=-62.45 CenterY=3.25 CenterZ=0 NormalX=0 NormalY=0 NormalZ=1 AngleXU=0 Radius=1.6
    g3: Circle CenterX=-62.45 CenterY=-3.25 CenterZ=0 NormalX=0 NormalY=0 NormalZ=1 AngleXU=0 Radius=1.6
  constraints (10):
    c: Distance(g0) = 5.25
    c: Coincident(g0,g-3)
    c: PointOnObject(g0,g-3)
    c: Vertical(g1)
    c: DistanceY(g1,g1) = 6.5
    c: Symmetric(g1,g1,g0)
    c: Diameter(g2) = 3.2
    c: Diameter(g3) = 3.2
    c: Coincident(g2,g1)
    c: Coincident(g3,g1)
FEATURE [Sketcher::SketchObject] Sketch032  label="spazio per PILA 18650"
  ArcFitTolerance = 1e-06
  AttachmentSupport = -> [XY_Plane]
  ExternalGeometry = -> [Sketch]
  FullyConstrained = true
  MakeInternals = false
  MapMode = 5
  sketch-geometry (2):
    g0: LineSegment [constr] StartX=-178.142 StartY=-1.74e-14 StartZ=0 EndX=-190.142 EndY=-1.83e-14 EndZ=0
    g1: Circle CenterX=-190.142 CenterY=-1.83e-14 CenterZ=0 NormalX=0 NormalY=0 NormalZ=1 AngleXU=0 Radius=9.25
  constraints (5):
    c: Distance(g0) = 12
    c: Coincident(g0,g-3)
    c: PointOnObject(g0,g-4)
    c: Diameter(g1) = 18.5
    c: Coincident(g1,g0)
FEATURE [Part::Extrusion] Extrude030  label="Extrude spazio per PILA 18650"
  Base = -> Sketch032
  Dir = (0,0,1)
  DirLink = -> Sketch [Edge45]
  DirMode = 2
  FaceMakerClass = Part::FaceMakerBullseye
  FaceMakerMode = 3
  LengthFwd = 68
  LengthRev = 0
  Placement = pos=(6,0,-72.7) rot=(0,0,1;0rad)
  Solid = true
  Symmetric = false
FEATURE [Sketcher::SketchObject] Sketch033  label="fermo per scheda micro"
  ArcFitTolerance = 1e-06
  AttachmentSupport = -> [XZ_Plane]
  ExternalGeometry = -> [Sketch]
  FullyConstrained = true
  MakeInternals = false
  MapMode = 5
  Placement = pos=(0,0,0) rot=(1,0,0;1.5708rad)
  sketch-geometry (12):
    g0: LineSegment StartX=-11.6 StartY=6 StartZ=0 EndX=-4 EndY=6 EndZ=0
    g1: LineSegment StartX=-4 StartY=6 StartZ=0 EndX=-4 EndY=36.4 EndZ=0
    g2: LineSegment StartX=-4 StartY=36.4 StartZ=0 EndX=-11.6 EndY=36.4 EndZ=0
    g3: LineSegment StartX=-11.6 StartY=36.4 StartZ=0 EndX=-11.6 EndY=6 EndZ=0
    g4: LineSegment StartX=-80.11 StartY=11.6 StartZ=0 EndX=-70.51 EndY=11.6 EndZ=0
    g5: LineSegment StartX=-70.51 StartY=11.6 StartZ=0 EndX=-70.51 EndY=6 EndZ=0
    g6: LineSegment StartX=-70.51 StartY=6 StartZ=0 EndX=-80.11 EndY=6 EndZ=0
    g7: LineSegment StartX=-80.11 StartY=6 StartZ=0 EndX=-80.11 EndY=11.6 EndZ=0
    g8: LineSegment StartX=-78.51 StartY=36.4 StartZ=0 EndX=-70.51 EndY=36.4 EndZ=0
    g9: LineSegment StartX=-70.51 StartY=36.4 StartZ=0 EndX=-70.51 EndY=30.8 EndZ=0
    g10: LineSegment StartX=-70.51 StartY=30.8 StartZ=0 EndX=-78.51 EndY=30.8 EndZ=0
    g11: LineSegment StartX=-78.51 StartY=30.8 StartZ=0 EndX=-78.51 EndY=36.4 EndZ=0
  constraints (33):
    c: Horizontal(g0)
    c: Coincident(g1,g0)
    c: Coincident(g2,g1)
    c: Horizontal(g2)
    c: Coincident(g3,g2)
    c: Coincident(g3,g0)
    c: Vertical(g3)
    c: DistanceX(g2,g2) = 7.6
    c: Coincident(g1,g-3)
    c: Coincident(g0,g-3)
    c: Horizontal(g4)
    c: Coincident(g5,g4)
    c: Vertical(g5)
    c: Coincident(g6,g5)
    c: Horizontal(g6)
    c: Coincident(g7,g6)
    c: Coincident(g7,g4)
    c: Vertical(g7)
    c: DistanceY(g5,g5) = 5.6
    c: DistanceX(g4,g4) = 9.6
    c: Coincident(g9,g8)
    c: Vertical(g9)
    c: Coincident(g10,g9)
    c: Horizontal(g10)
    c: Coincident(g11,g10)
    c: Coincident(g11,g8)
    c: Vertical(g11)
    c: DistanceY(g9,g9) = 5.6
    c: DistanceX(g10,g10) = 8
    c: Coincident(g4,g-4)
    c: DistanceX(g4,g10) = 1.6
    c: Horizontal(g8)
    c: DistanceY(g8,g1) = 0
FEATURE [Sketcher::SketchObject] Sketch034  label="buchi guida rail"
  ArcFitTolerance = 1e-06
  AttachmentSupport = -> [XY_Plane]
  ExternalGeometry = -> [Sketch]
  FullyConstrained = true
  MakeInternals = false
  MapMode = 5
  sketch-geometry (6):
    g0: LineSegment [constr] StartX=-100.8 StartY=9.1e-15 StartZ=0 EndX=-93.3 EndY=0 EndZ=0
    g1: LineSegment [constr] StartX=-93.3 StartY=0 StartZ=0 EndX=-73.3 EndY=0 EndZ=0
    g2: LineSegment [constr] StartX=-73.3 StartY=0 StartZ=0 EndX=-53.3 EndY=0 EndZ=0
    g3: Circle CenterX=-93.3 CenterY=0 CenterZ=0 NormalX=0 NormalY=0 NormalZ=1 AngleXU=0 Radius=2.5
    g4: Circle CenterX=-73.3 CenterY=0 CenterZ=0 NormalX=0 NormalY=0 NormalZ=1 AngleXU=0 Radius=2.5
    g5: Circle CenterX=-53.3 CenterY=0 CenterZ=0 NormalX=0 NormalY=0 NormalZ=1 AngleXU=0 Radius=2.5
  constraints (15):
    c: Distance(g0) = 7.5
    c: Coincident(g0,g-3)
    c: PointOnObject(g0,g-1)
    c: Distance(g1) = 20
    c: Coincident(g1,g0)
    c: PointOnObject(g1,g-1)
    c: Distance(g2) = 20
    c: Coincident(g2,g1)
    c: PointOnObject(g2,g-1)
    c: Diameter(g3) = 5
    c: Diameter(g4) = 5
    c: Diameter(g5) = 5
    c: Coincident(g3,g0)
    c: Coincident(g4,g1)
    c: Coincident(g5,g2)
FEATURE [PartDesign::FeatureBase] BaseFeature
  BaseFeature = -> Extrude017
  Suppressed = false
FEATURE [PartDesign::Body] Body001  label="perno fermo rumble"
  AllowCompound = false
  BaseFeature = -> Extrude017
  Group = -> [BaseFeature,Sketch021]
  Origin = -> Origin001
  Tip = -> BaseFeature
FEATURE [Part::Extrusion] Extrude032  label="Extrude buchi guida rail"
  Base = -> Sketch034
  Dir = (0,0,1)
  DirMode = 2
  FaceMakerClass = Part::FaceMakerBullseye
  FaceMakerMode = 3
  LengthFwd = -6.2
  LengthRev = 0
  Placement = pos=(0,0,43.2) rot=(0,0,1;0rad)
  Solid = true
  Symmetric = false
FEATURE [Part::Extrusion] Extrude033  label="Extrude fori superiori per solenoide e oled001"
  Base = -> Sketch030
  Dir = (0,0,1)
  DirMode = 2
  FaceMakerClass = Part::FaceMakerBullseye
  FaceMakerMode = 3
  LengthFwd = -4.8
  LengthRev = 0
  Placement = pos=(0,0,41.2) rot=(0,0,1;0rad)
  Solid = true
  Symmetric = false
FEATURE [Part::Extrusion] Extrude034  label="Extrude fori sotto impugnatura001"
  Base = -> Sketch029
  Dir = (0,0,1)
  DirMode = 2
  FaceMakerClass = Part::FaceMakerBullseye
  FaceMakerMode = 3
  LengthFwd = 5
  LengthRev = 0
  Placement = pos=(0,0,-83) rot=(0,0,1;0rad)
  Solid = true
  Symmetric = false
FEATURE [Part::Extrusion] Extrude035  label="Extrude fori inferiori switch pompa001"
  Base = -> Sketch031
  Dir = (0,0,1)
  DirMode = 2
  FaceMakerClass = Part::FaceMakerBullseye
  FaceMakerMode = 3
  LengthFwd = 4
  LengthRev = 0
  Placement = pos=(0,0,-1.7) rot=(0,0,1;0rad)
  Solid = true
  Symmetric = false
FEATURE [Part::Extrusion] Extrude036  label="Extrude foro sotto posteriore M3x5x007"
  Base = -> Sketch027
  Dir = (0,0,1)
  DirMode = 2
  FaceMakerClass = Part::FaceMakerBullseye
  FaceMakerMode = 3
  LengthFwd = 6.2
  LengthRev = 0
  Placement = pos=(0,0,-9.6) rot=(0,0,1;0rad)
  Solid = true
  Symmetric = false
FEATURE [Part::Extrusion] Extrude037  label="Extrude foro sotto anteriore M3x5x007"
  Base = -> Sketch026
  Dir = (0,0,1)
  DirMode = 2
  FaceMakerClass = Part::FaceMakerBullseye
  FaceMakerMode = 3
  LengthFwd = 6.2
  LengthRev = 0
  Solid = true
  Symmetric = false
FEATURE [Sketcher::SketchObject] Sketch035  label="foro per fissaggio micro"
  ArcFitTolerance = 1e-06
  AttachmentSupport = -> [XZ_Plane]
  ExternalGeometry = -> [Sketch,Sketch033]
  FullyConstrained = true
  MakeInternals = false
  MapMode = 5
  Placement = pos=(0,0,0) rot=(1,0,0;1.5708rad)
  sketch-geometry (3):
    g0: Circle CenterX=-7.8 CenterY=21.2 CenterZ=0 NormalX=0 NormalY=0 NormalZ=1 AngleXU=0 Radius=1.6
    g1: GeomPoint [constr] X=-4 Y=21.2 Z=0
    g2: LineSegment [constr] StartX=-4 StartY=21.2 StartZ=0 EndX=-11.6 EndY=21.2 EndZ=0
  constraints (6):
    c: Diameter(g0) = 3.2
    c: Symmetric(g-3,g-3,g1)
    c: Coincident(g2,g1)
    c: Horizontal(g2)
    c: DistanceX(g-4,g2) = 0
    c: Symmetric(g2,g1,g0)
FEATURE [Part::Extrusion] Extrude038  label="Extrude foro per fissaggio micro"
  Base = -> Sketch035
  Dir = (0,-1,2e-16)
  DirMode = 2
  FaceMakerClass = Part::FaceMakerBullseye
  FaceMakerMode = 3
  LengthFwd = 3
  LengthRev = 0
  Placement = pos=(0,8.6,0) rot=(0,0,1;0rad)
  Solid = true
  Symmetric = false
FEATURE [Sketcher::SketchObject] Sketch036  label="supporto per alimentatore"
  ArcFitTolerance = 1e-06
  AttachmentSupport = -> [XZ_Plane]
  ExternalGeometry = -> [Sketch,Sketch016,Sketch022]
  FullyConstrained = true
  MakeInternals = false
  MapMode = 5
  Placement = pos=(0,0,0) rot=(1,0,0;1.5708rad)
  sketch-geometry (5):
    g0: LineSegment StartX=-211.843 StartY=-50.0944 StartZ=0 EndX=-211.843 EndY=-80.4316 EndZ=0
    g1: LineSegment StartX=-211.843 StartY=-50.0944 StartZ=0 EndX=-207.775 EndY=-41.3701 EndZ=0
    g2: LineSegment [constr] StartX=-209.443 StartY=-50.0944 StartZ=0 EndX=-209.443 EndY=-80.4316 EndZ=0
    g3: LineSegment StartX=-207.775 StartY=-41.3701 StartZ=0 EndX=-207.775 EndY=-80.4316 EndZ=0
    g4: LineSegment StartX=-211.843 StartY=-80.4316 StartZ=0 EndX=-207.775 EndY=-80.4316 EndZ=0
  constraints (15):
    c: Vertical(g0)
    c: Coincident(g1,g0)
    c: Vertical(g2)
    c: Tangent(g2,g-5)
    c: Coincident(g3,g1)
    c: Vertical(g3)
    c: DistanceY(g-3,g3) = -2
    c: Tangent(g1,g-8)
    c: DistanceY(g-3,g0) = -2
    c: Coincident(g4,g0)
    c: Coincident(g4,g3)
    c: Tangent(g0,g-6)
    c: DistanceY(g-3,g2) = -2
    c: DistanceY(g2,g0) = 0
    c: DistanceX(g-3,g3) = 6.8
FEATURE [Part::Extrusion] Extrude039  label="Extrude039 supporto alimentatore"
  Base = -> Sketch036
  Dir = (0,-1,2e-16)
  DirMode = 2
  FaceMakerClass = Part::FaceMakerBullseye
  FaceMakerMode = 3
  LengthFwd = 25.2
  LengthRev = 0
  Solid = true
  Symmetric = true
FEATURE [Sketcher::SketchObject] Sketch037  label="scavo per alimentatore"
  ArcFitTolerance = 1e-06
  AttachmentSupport = -> [XZ_Plane]
  ExternalGeometry = -> [Sketch036]
  FullyConstrained = true
  MakeInternals = false
  MapMode = 5
  Placement = pos=(0,0,0) rot=(1,0,0;1.5708rad)
  sketch-geometry (4):
    g0: LineSegment StartX=-209.575 StartY=-50.4316 StartZ=0 EndX=-209.575 EndY=-80.4316 EndZ=0
    g1: LineSegment StartX=-209.575 StartY=-50.4316 StartZ=0 EndX=-207.775 EndY=-50.4316 EndZ=0
    g2: LineSegment StartX=-207.775 StartY=-50.4316 StartZ=0 EndX=-207.775 EndY=-80.4316 EndZ=0
    g3: LineSegment StartX=-207.775 StartY=-80.4316 StartZ=0 EndX=-209.575 EndY=-80.4316 EndZ=0
  constraints (11):
    c: Vertical(g0)
    c: Coincident(g1,g0)
    c: Horizontal(g1)
    c: Coincident(g2,g1)
    c: Vertical(g2)
    c: Coincident(g3,g2)
    c: Coincident(g3,g0)
    c: Horizontal(g3)
    c: DistanceX(g1,g1) = 1.8
    c: Coincident(g2,g-3)
    c: DistanceY(g2,g2) = 30
FEATURE [Part::Extrusion] Extrude040  label="Extrude040 scavo alimentatore"
  Base = -> Sketch037
  Dir = (0,-1,2e-16)
  DirMode = 2
  FaceMakerClass = Part::FaceMakerBullseye
  FaceMakerMode = 3
  LengthFwd = 19.5
  LengthRev = 0
  Solid = true
  Symmetric = true
FEATURE [Part::Extrusion] Extrude031  label="Extrude fermo per scheda micro"
  Base = -> Sketch033
  Dir = (0,-1,2e-16)
  DirMode = 2
  FaceMakerClass = Part::FaceMakerBullseye
  FaceMakerMode = 3
  LengthFwd = 3
  LengthRev = 0
  Placement = pos=(0,8.6,0) rot=(0,0,1;0rad)
  Solid = true
  Symmetric = false
FEATURE [Sketcher::SketchObject] Sketch038  label="scavo driver solenoide"
  ArcFitTolerance = 1e-06
  AttachmentSupport = -> [XZ_Plane]
  ExternalGeometry = -> [Sketch,Sketch036]
  FullyConstrained = true
  MakeInternals = false
  MapMode = 5
  Placement = pos=(0,0,0) rot=(1,0,0;1.5708rad)
  sketch-geometry (7):
    g0: LineSegment StartX=-193.66 StartY=-11.0994 StartZ=0 EndX=-195.11 EndY=-10.4232 EndZ=0
    g1: LineSegment StartX=-195.11 StartY=-10.4232 StartZ=0 EndX=-209.225 EndY=-40.6939 EndZ=0
    g2: LineSegment StartX=-193.66 StartY=-11.0994 StartZ=0 EndX=-190.216 EndY=-12.7054 EndZ=0
    g3: LineSegment StartX=-190.216 StartY=-12.7054 StartZ=0 EndX=-204.331 EndY=-42.9761 EndZ=0
    g4: LineSegment StartX=-204.331 StartY=-42.9761 StartZ=0 EndX=-207.775 EndY=-41.3701 EndZ=0
    g5: LineSegment [constr] StartX=-209.225 StartY=-40.6939 StartZ=0 EndX=-207.775 EndY=-41.3701 EndZ=0
    g6: LineSegment StartX=-209.225 StartY=-40.6939 StartZ=0 EndX=-207.775 EndY=-41.3701 EndZ=0
  constraints (19):
    c: Coincident(g1,g0)
    c: Coincident(g3,g2)
    c: Coincident(g4,g3)
    c: Distance(g2) = 3.8
    c: Distance(g1) = 33.4
    c: Coincident(g5,g1)
    c: Distance(g5) = 1.6
    c: Coincident(g-4,g5)
    c: Perpendicular(g5,g-3)
    c: Parallel(g1,g-3)
    c: Perpendicular(g1,g0)
    c: Distance(g0) = 1.6
    c: Coincident(g6,g1)
    c: Coincident(g6,g5)
    c: Parallel(g3,g-3)
    c: Perpendicular(g3,g4)
    c: Perpendicular(g2,g3)
    c: Coincident(g2,g0)
    c: Coincident(g4,g5)
FEATURE [Part::Extrusion] Extrude041  label="Extrude scavo driver solenoide"
  Base = -> Sketch038
  Dir = (0,-1,2e-16)
  DirMode = 2
  FaceMakerClass = Part::FaceMakerBullseye
  FaceMakerMode = 3
  LengthFwd = 17
  LengthRev = 0
  Solid = true
  Symmetric = true
FEATURE [Sketcher::SketchObject] Sketch039  label="scavo per cavo usb per micro"
  ArcFitTolerance = 1e-06
  AttachmentSupport = -> [XZ_Plane]
  ExternalGeometry = -> [Sketch,Sketch016]
  FullyConstrained = true
  MakeInternals = false
  MapMode = 5
  Placement = pos=(0,0,0) rot=(1,0,0;1.5708rad)
  sketch-geometry (4):
    g0: LineSegment StartX=-82.51 StartY=36.4 StartZ=0 EndX=-74.51 EndY=36.4 EndZ=0
    g1: LineSegment StartX=-74.51 StartY=36.4 StartZ=0 EndX=-74.51 EndY=30.8 EndZ=0
    g2: LineSegment StartX=-74.51 StartY=30.8 StartZ=0 EndX=-82.51 EndY=30.8 EndZ=0
    g3: LineSegment StartX=-82.51 StartY=30.8 StartZ=0 EndX=-82.51 EndY=36.4 EndZ=0
  constraints (11):
    c: Coincident(g1,g0)
    c: Vertical(g1)
    c: Coincident(g2,g1)
    c: Horizontal(g2)
    c: Coincident(g3,g2)
    c: Coincident(g3,g0)
    c: Vertical(g3)
    c: Tangent(g0,g-3)
    c: Tangent(g2,g-4)
    c: Tangent(g3,g-4)
    c: Tangent(g1,g-4)
FEATURE [Part::Extrusion] Extrude042  label="Extrude scavo per cavo usb per micro"
  Base = -> Sketch039
  Dir = (0,-1,2e-16)
  DirMode = 2
  FaceMakerClass = Part::FaceMakerBullseye
  FaceMakerMode = 3
  LengthFwd = 11.2
  LengthRev = 0
  Solid = true
  Symmetric = true
FEATURE [Sketcher::SketchObject] Sketch040  label="scavo saldature alimentatore connettore 5v"
  ArcFitTolerance = 1e-06
  AttachmentSupport = -> [XZ_Plane]
  ExternalGeometry = -> [Sketch037]
  FullyConstrained = true
  MakeInternals = false
  MapMode = 5
  Placement = pos=(0,0,0) rot=(1,0,0;1.5708rad)
  sketch-geometry (4):
    g0: LineSegment StartX=-211.175 StartY=-52.4316 StartZ=0 EndX=-211.175 EndY=-56.4316 EndZ=0
    g1: LineSegment StartX=-211.175 StartY=-52.4316 StartZ=0 EndX=-209.575 EndY=-52.4316 EndZ=0
    g2: LineSegment StartX=-209.575 StartY=-52.4316 StartZ=0 EndX=-209.575 EndY=-56.4316 EndZ=0
    g3: LineSegment StartX=-209.575 StartY=-56.4316 StartZ=0 EndX=-211.175 EndY=-56.4316 EndZ=0
  constraints (11):
    c: Vertical(g0)
    c: Coincident(g1,g0)
    c: Horizontal(g1)
    c: Coincident(g2,g1)
    c: Coincident(g3,g2)
    c: Coincident(g3,g0)
    c: Horizontal(g3)
    c: DistanceX(g1,g1) = 1.6
    c: DistanceY(g2,g2) = 4
    c: Tangent(g2,g-3)
    c: DistanceY(g1,g-3) = 2
FEATURE [Part::Extrusion] Extrude043  label="Extrude scavo saldature alimentatore connettore 5v"
  Base = -> Sketch040
  Dir = (0,-1,2e-16)
  DirMode = 2
  FaceMakerClass = Part::FaceMakerBullseye
  FaceMakerMode = 3
  LengthFwd = 8
  LengthRev = 0
  Solid = true
  Symmetric = true
FEATURE [Sketcher::SketchObject] Sketch041  label="scavo saldature alimentatore connettore 5v verticali"
  ArcFitTolerance = 1e-06
  AttachmentSupport = -> [XZ_Plane]
  ExternalGeometry = -> [Sketch037]
  FullyConstrained = true
  MakeInternals = false
  MapMode = 5
  Placement = pos=(0,0,0) rot=(1,0,0;1.5708rad)
  sketch-geometry (4):
    g0: LineSegment StartX=-211.175 StartY=-53.6316 StartZ=0 EndX=-209.575 EndY=-53.6316 EndZ=0
    g1: LineSegment StartX=-209.575 StartY=-53.6316 StartZ=0 EndX=-209.575 EndY=-76.6316 EndZ=0
    g2: LineSegment StartX=-209.575 StartY=-76.6316 StartZ=0 EndX=-211.175 EndY=-76.6316 EndZ=0
    g3: LineSegment StartX=-211.175 StartY=-76.6316 StartZ=0 EndX=-211.175 EndY=-53.6316 EndZ=0
  constraints (11):
    c: Horizontal(g0)
    c: Coincident(g1,g0)
    c: Coincident(g2,g1)
    c: Horizontal(g2)
    c: Coincident(g3,g2)
    c: Coincident(g3,g0)
    c: Vertical(g3)
    c: DistanceY(g3,g3) = 23
    c: DistanceX(g0,g0) = 1.6
    c: Tangent(g1,g-3)
    c: DistanceY(g0,g-3) = 3.2
FEATURE [Part::Extrusion] Extrude044  label="Extrude scavo saldature alimentatore connettore 5v verticali"
  Base = -> Sketch041
  Dir = (0,-1,2e-16)
  DirMode = 2
  FaceMakerClass = Part::FaceMakerBullseye
  FaceMakerMode = 3
  LengthFwd = 3.2
  LengthRev = 0
  Placement = pos=(0,8.3,0) rot=(0,0,1;0rad)
  Solid = true
  Symmetric = false
FEATURE [Sketcher::SketchObject] Sketch042  label="fermi per driver solenoide e alimentatore"
  ArcFitTolerance = 1e-06
  AttachmentSupport = -> [XZ_Plane]
  ExternalGeometry = -> [Sketch036,Sketch037,Sketch,Sketch038]
  FullyConstrained = true
  MakeInternals = false
  MapMode = 5
  Placement = pos=(0,0,0) rot=(1,0,0;1.5708rad)
  sketch-geometry (27):
    g0: LineSegment StartX=-195.773 StartY=-15.631 StartZ=0 EndX=-196.702 EndY=-17.6249 EndZ=0
    g1: LineSegment StartX=-196.702 StartY=-17.6249 StartZ=0 EndX=-194.709 EndY=-18.5546 EndZ=0
    g2: LineSegment StartX=-194.709 StartY=-18.5546 StartZ=0 EndX=-193.779 EndY=-16.5607 EndZ=0
    g3: LineSegment StartX=-193.779 StartY=-16.5607 StartZ=0 EndX=-195.773 EndY=-15.631 EndZ=0
    g4: LineSegment StartX=-196.547 StartY=-13.5047 StartZ=0 EndX=-198.829 EndY=-18.3988 EndZ=0
    g5: LineSegment StartX=-198.829 StartY=-18.3988 StartZ=0 EndX=-195.385 EndY=-20.0047 EndZ=0
    g6: LineSegment StartX=-193.258 StartY=-19.2308 StartZ=0 EndX=-192.329 EndY=-17.2369 EndZ=0
    g7: LineSegment StartX=-193.103 StartY=-15.1106 StartZ=0 EndX=-196.547 EndY=-13.5047 EndZ=0
    g8: LineSegment [constr] StartX=-193.935 StartY=-20.6809 StartZ=0 EndX=-193.258 EndY=-19.2308 EndZ=0
    g9: LineSegment [constr] StartX=-193.935 StartY=-20.6809 StartZ=0 EndX=-195.385 EndY=-20.0047 EndZ=0
    g10: ArcOfCircle CenterX=-193.779 CenterY=-16.5607 CenterZ=0 NormalX=0 NormalY=0 NormalZ=1 AngleXU=0 Radius=1.6 StartAngle=5.84685 EndAngle=7.41765
    g11: GeomPoint [constr] X=-191.653 Y=-15.7868 Z=0
    g12: ArcOfCircle CenterX=-194.709 CenterY=-18.5546 CenterZ=0 NormalX=0 NormalY=0 NormalZ=1 AngleXU=0 Radius=1.6 StartAngle=4.27606 EndAngle=5.84685
    g13: GeomPoint [constr] X=-193.935 Y=-20.6809 Z=0
    g14: LineSegment StartX=-207.775 StartY=-46.8316 StartZ=0 EndX=-207.775 EndY=-50.8316 EndZ=0
    g15: LineSegment StartX=-207.775 StartY=-46.8316 StartZ=0 EndX=-203.775 EndY=-46.8316 EndZ=0
    g16: LineSegment StartX=-203.775 StartY=-46.8316 StartZ=0 EndX=-203.775 EndY=-50.8316 EndZ=0
    g17: LineSegment StartX=-207.775 StartY=-50.8316 StartZ=0 EndX=-203.775 EndY=-50.8316 EndZ=0
    g18: LineSegment StartX=-209.375 StartY=-52.4316 StartZ=0 EndX=-203.775 EndY=-52.4316 EndZ=0
    g19: LineSegment StartX=-202.175 StartY=-50.8316 StartZ=0 EndX=-202.175 EndY=-46.8316 EndZ=0
    g20: LineSegment StartX=-203.775 StartY=-45.2316 StartZ=0 EndX=-209.375 EndY=-45.2316 EndZ=0
    g21: LineSegment StartX=-209.375 StartY=-45.2316 StartZ=0 EndX=-209.375 EndY=-52.4316 EndZ=0
    g22: ArcOfCircle CenterX=-203.775 CenterY=-46.8316 CenterZ=0 NormalX=0 NormalY=0 NormalZ=1 AngleXU=0 Radius=1.6 StartAngle=1.8e-15 EndAngle=1.5708
    g23: GeomPoint [constr] X=-202.175 Y=-45.2316 Z=0
    g24: ArcOfCircle CenterX=-203.775 CenterY=-50.8316 CenterZ=0 NormalX=0 NormalY=0 NormalZ=1 AngleXU=0 Radius=1.6 StartAngle=4.71239 EndAngle=6.28319
    g25: GeomPoint [constr] X=-202.175 Y=-52.4316 Z=0
    g26: LineSegment [constr] StartX=-207.775 StartY=-50.4316 StartZ=0 EndX=-207.775 EndY=-50.8316 EndZ=0
  constraints (69):
    c: Coincident(g1,g0)
    c: Coincident(g2,g1)
    c: Coincident(g3,g2)
    c: Coincident(g3,g0)
    c: Parallel(g0,g2)
    c: Perpendicular(g3,g0)
    c: Perpendicular(g1,g0)
    c: Coincident(g5,g4)
    c: Coincident(g7,g4)
    c: Distance(g3) = 2.2
    c: Distance(g2) = 2.2
    c: Parallel(g6,g2)
    c: Parallel(g6,g4)
    c: Perpendicular(g5,g6)
    c: Perpendicular(g7,g6)
    c: Distance(g13,g11) = 5.4
    c: Distance(g5,g13) = 5.4
    c: Coincident(g9,g8)
    c: Distance(g8) = 1.6
    c: Distance(g9) = 1.6
    c: Perpendicular(g9,g8)
    c: Parallel(g8,g6)
    c: Coincident(g8,g13)
    c: Distance(g8,g1) = 1.6
    c: Distance(g9,g1) = 1.6
    c: Tangent(g0,g-5)
    c: Distance(g0,g-6) = 26.2
    c: PointOnObject(g11,g7)
    c: PointOnObject(g11,g6)
    c: Tangent(g7,g10) = -1.5708
    c: Tangent(g6,g10) = -1.5708
    c: PointOnObject(g13,g5)
    c: Tangent(g5,g12) = -1.5708
    c: Tangent(g6,g12) = -1.5708
    c: Equal(g10,g12)
    c: Coincident(g10,g2)
    c: Vertical(g14)
    c: Coincident(g15,g14)
    c: Horizontal(g15)
    c: Coincident(g16,g15)
    c: Vertical(g16)
    c: Coincident(g17,g14)
    c: Coincident(g17,g16)
    c: Horizontal(g17)
    c: Distance(g16) = 4
    c: Distance(g15) = 4
    c: Horizontal(g18)
    c: Vertical(g19)
    c: Horizontal(g20)
    c: Coincident(g21,g20)
    c: Coincident(g21,g18)
    c: Vertical(g21)
    c: Distance(g20,g23) = 7.2
    c: Distance(g25,g23) = 7.2
    c: DistanceY(g18,g14) = 1.6
    c: DistanceX(g18,g14) = 1.6
    c: PointOnObject(g23,g20)
    c: PointOnObject(g23,g19)
    c: Tangent(g20,g22) = -1.5708
    c: Tangent(g19,g22) = -1.5708
    c: PointOnObject(g25,g19)
    c: Tangent(g18,g24) = -1.5708
    c: Tangent(g19,g24) = -1.5708
    c: Equal(g22,g24)
    c: Coincident(g22,g15)
    c: Vertical(g26)
    c: Distance(g26) = 0.4
    c: Coincident(g26,g-4)
    c: Coincident(g14,g26)
FEATURE [Part::Extrusion] Extrude045  label="Extrude fermi per driver solenoide e alimentatore"
  Base = -> Sketch042
  Dir = (0,-1,2e-16)
  DirMode = 2
  FaceMakerClass = Part::FaceMakerBullseye
  FaceMakerMode = 3
  LengthFwd = 25.2
  LengthRev = 0
  Solid = true
  Symmetric = true
FEATURE [Sketcher::SketchObject] Sketch043  label="scavo pulizia fermo alimentatore"
  ArcFitTolerance = 1e-06
  AttachmentSupport = -> [XZ_Plane]
  ExternalGeometry = -> [Sketch042,Sketch036,Sketch037]
  FullyConstrained = true
  MakeInternals = false
  MapMode = 5
  Placement = pos=(0,0,0) rot=(1,0,0;1.5708rad)
  sketch-geometry (6):
    g0: LineSegment StartX=-209.375 StartY=-52.4316 StartZ=0 EndX=-209.375 EndY=-50.4316 EndZ=0
    g1: LineSegment StartX=-209.375 StartY=-50.4316 StartZ=0 EndX=-207.775 EndY=-50.4316 EndZ=0
    g2: LineSegment StartX=-207.775 StartY=-50.4316 StartZ=0 EndX=-207.775 EndY=-45.2316 EndZ=0
    g3: LineSegment StartX=-207.775 StartY=-45.2316 StartZ=0 EndX=-202.175 EndY=-45.2316 EndZ=0
    g4: LineSegment StartX=-202.175 StartY=-45.2316 StartZ=0 EndX=-202.175 EndY=-52.4316 EndZ=0
    g5: LineSegment StartX=-202.175 StartY=-52.4316 StartZ=0 EndX=-209.375 EndY=-52.4316 EndZ=0
  constraints (13):
    c: Vertical(g0)
    c: Coincident(g1,g0)
    c: Coincident(g2,g1)
    c: Coincident(g3,g2)
    c: Coincident(g4,g3)
    c: Coincident(g5,g4)
    c: Coincident(g5,g0)
    c: Horizontal(g5)
    c: Coincident(g0,g-6)
    c: Tangent(g1,g-8)
    c: Tangent(g2,g-4)
    c: Tangent(g3,g-7)
    c: Tangent(g4,g-3)
FEATURE [Part::Extrusion] Extrude046  label="Extrude scavo pulizia fermo alimentatore"
  Base = -> Sketch043
  Dir = (0,-1,2e-16)
  DirMode = 2
  FaceMakerClass = Part::FaceMakerBullseye
  FaceMakerMode = 3
  LengthFwd = 19.5
  LengthRev = 0
  Solid = true
  Symmetric = true
FEATURE [Sketcher::SketchObject] Sketch044  label="buchini per fissaggio oled"
  ArcFitTolerance = 1e-06
  AttachmentSupport = -> [YZ_Plane]
  ExternalGeometry = -> [Sketch]
  FullyConstrained = true
  MakeInternals = false
  MapMode = 5
  Placement = pos=(0,0,0) rot=(0.57735,0.57735,0.57735;2.0944rad)
  sketch-geometry (5):
    g0: LineSegment [constr] StartX=1.5e-14 StartY=67.3588 StartZ=0 EndX=0 EndY=64.3588 EndZ=0
    g1: LineSegment [constr] StartX=0 StartY=64.3588 StartZ=0 EndX=10.4 EndY=64.3588 EndZ=0
    g2: LineSegment [constr] StartX=0 StartY=64.3588 StartZ=0 EndX=-10.4 EndY=64.3588 EndZ=0
    g3: Circle CenterX=10.4 CenterY=64.3588 CenterZ=0 NormalX=0 NormalY=0 NormalZ=1 AngleXU=0 Radius=1.5
    g4: Circle CenterX=-10.4 CenterY=64.3588 CenterZ=0 NormalX=0 NormalY=0 NormalZ=1 AngleXU=0 Radius=1.5
  constraints (13):
    c: Distance(g0) = 3
    c: PointOnObject(g0,g-2)
    c: Coincident(g1,g0)
    c: Horizontal(g1)
    c: Coincident(g2,g0)
    c: Horizontal(g2)
    c: DistanceX(g1,g1) = 10.4
    c: Coincident(g3,g1)
    c: Diameter(g4) = 3
    c: Coincident(g4,g2)
    c: Coincident(g0,g-7)
    c: Equal(g1,g2)
    c: Equal(g4,g3)
FEATURE [Part::Extrusion] Extrude047  label="Extrude buchini per fissaggio oled"
  Base = -> Sketch044
  Dir = (1,0,0)
  DirMode = 2
  FaceMakerClass = Part::FaceMakerBullseye
  FaceMakerMode = 3
  LengthFwd = 10
  LengthRev = 0
  Placement = pos=(-186,0,0) rot=(0,0,1;0rad)
  Solid = true
  Symmetric = false
FEATURE [Sketcher::SketchObject] Sketch046  label="scavo 5x5 neopixel"
  ArcFitTolerance = 1e-06
  AttachmentSupport = -> [YZ_Plane002]
  FullyConstrained = true
  MakeInternals = false
  MapMode = 5
  Placement = pos=(0,0,0) rot=(0.57735,0.57735,0.57735;2.0944rad)
  sketch-geometry (4):
    g0: LineSegment StartX=-2.7 StartY=2.7 StartZ=0 EndX=2.7 EndY=2.7 EndZ=0
    g1: LineSegment StartX=2.7 StartY=2.7 StartZ=0 EndX=2.7 EndY=-2.7 EndZ=0
    g2: LineSegment StartX=2.7 StartY=-2.7 StartZ=0 EndX=-2.7 EndY=-2.7 EndZ=0
    g3: LineSegment StartX=-2.7 StartY=-2.7 StartZ=0 EndX=-2.7 EndY=2.7 EndZ=0
  constraints (11):
    c: Horizontal(g0)
    c: Coincident(g1,g0)
    c: Vertical(g1)
    c: Coincident(g2,g1)
    c: Horizontal(g2)
    c: Coincident(g3,g2)
    c: Coincident(g3,g0)
    c: Vertical(g3)
    c: DistanceX(g0,g0) = 5.4
    c: DistanceY(g1,g1) = 5.4
    c: Symmetric(g0,g1,g-1)
FEATURE [Part::Extrusion] Extrude049  label="Extrude scavo 5x5 neopixel"
  Base = -> Sketch046
  Dir = (1,0,0)
  DirMode = 2
  FaceMakerClass = Part::FaceMakerBullseye
  FaceMakerMode = 3
  LengthFwd = 1
  LengthRev = 0
  Solid = true
  Symmetric = false
FEATURE [Sketcher::SketchObject] Sketch047  label="scavo 10x10 neopixel corpo"
  ArcFitTolerance = 1e-06
  AttachmentSupport = -> [YZ_Plane002]
  FullyConstrained = true
  MakeInternals = false
  MapMode = 5
  Placement = pos=(0,0,0) rot=(0.57735,0.57735,0.57735;2.0944rad)
  sketch-geometry (4):
    g0: LineSegment StartX=-5 StartY=5.1 StartZ=0 EndX=5 EndY=5.1 EndZ=0
    g1: LineSegment StartX=5 StartY=5.1 StartZ=0 EndX=5 EndY=-5.1 EndZ=0
    g2: LineSegment StartX=5 StartY=-5.1 StartZ=0 EndX=-5 EndY=-5.1 EndZ=0
    g3: LineSegment StartX=-5 StartY=-5.1 StartZ=0 EndX=-5 EndY=5.1 EndZ=0
  constraints (11):
    c: Horizontal(g0)
    c: Coincident(g1,g0)
    c: Vertical(g1)
    c: Coincident(g2,g1)
    c: Horizontal(g2)
    c: Coincident(g3,g2)
    c: Coincident(g3,g0)
    c: Vertical(g3)
    c: DistanceX(g0,g0) = 10
    c: DistanceY(g1,g1) = 10.2
    c: Symmetric(g0,g2,g-1)
FEATURE [Part::Extrusion] Extrude050  label="Extrude scavo 10x10 neopixel corpo"
  Base = -> Sketch047
  Dir = (1,0,0)
  DirMode = 2
  FaceMakerClass = Part::FaceMakerBullseye
  FaceMakerMode = 3
  LengthFwd = 8
  LengthRev = 0
  Placement = pos=(1,0,0) rot=(0,0,1;0rad)
  Solid = true
  Symmetric = false
FEATURE [Sketcher::SketchObject] Sketch048  label="buco per perno blocco neopixel"
  ArcFitTolerance = 1e-06
  AttachmentSupport = -> [XZ_Plane002]
  FullyConstrained = true
  MakeInternals = false
  MapMode = 5
  Placement = pos=(0,0,0) rot=(1,0,0;1.5708rad)
  sketch-geometry (4):
    g0: LineSegment StartX=3 StartY=1.2 StartZ=0 EndX=3 EndY=-1.2 EndZ=0
    g1: LineSegment StartX=3 StartY=-1.2 StartZ=0 EndX=5.4 EndY=-1.2 EndZ=0
    g2: LineSegment StartX=5.4 StartY=-1.2 StartZ=0 EndX=5.4 EndY=1.2 EndZ=0
    g3: LineSegment StartX=5.4 StartY=1.2 StartZ=0 EndX=3 EndY=1.2 EndZ=0
  constraints (11):
    c: Coincident(g1,g0)
    c: Horizontal(g1)
    c: Coincident(g2,g1)
    c: Vertical(g2)
    c: Coincident(g3,g2)
    c: Coincident(g3,g0)
    c: Horizontal(g3)
    c: DistanceX(g1,g1) = 2.4
    c: DistanceY(g2,g2) = 2.4
    c: Symmetric(g0,g0,g-1)
    c: DistanceX(g-1,g0) = 3
FEATURE [Sketcher::SketchObject] Sketch045  label="blocco principale per neopixel"
  ArcFitTolerance = 1e-06
  AttachmentSupport = -> [XZ_Plane002]
  ExternalGeometry = -> [Sketch048]
  FullyConstrained = true
  MakeInternals = false
  MapMode = 5
  Placement = pos=(0,0,0) rot=(1,0,0;1.5708rad)
  sketch-geometry (6):
    g0: LineSegment StartX=0 StartY=5.1 StartZ=0 EndX=0 EndY=-5.1 EndZ=0
    g1: LineSegment StartX=0 StartY=-5.1 StartZ=0 EndX=3 EndY=-5.1 EndZ=0
    g2: LineSegment StartX=7 StartY=-1.1 StartZ=0 EndX=7 EndY=5.1 EndZ=0
    g3: LineSegment StartX=7 StartY=5.1 StartZ=0 EndX=0 EndY=5.1 EndZ=0
    g4: ArcOfCircle CenterX=3 CenterY=-1.1 CenterZ=0 NormalX=0 NormalY=0 NormalZ=1 AngleXU=0 Radius=4 StartAngle=4.71239 EndAngle=6.28319
    g5: GeomPoint [constr] X=7 Y=-5.1 Z=0
  constraints (15):
    c: Vertical(g0)
    c: Coincident(g1,g0)
    c: Horizontal(g1)
    c: Vertical(g2)
    c: Coincident(g3,g2)
    c: Coincident(g3,g0)
    c: Horizontal(g3)
    c: DistanceY(g0,g0) = 10.2
    c: Symmetric(g0,g0,g-1)
    c: DistanceX(g3,g3) = 7
    c: PointOnObject(g5,g2)
    c: PointOnObject(g5,g1)
    c: Tangent(g2,g4) = -1.5708
    c: Tangent(g1,g4) = -1.5708
    c: DistanceX(g-3,g1) = 0
FEATURE [Part::Extrusion] Extrude048  label="Extrude blocco principale per neopixel"
  Base = -> Sketch045
  Dir = (0,-1,2e-16)
  DirMode = 2
  FaceMakerClass = Part::FaceMakerBullseye
  FaceMakerMode = 3
  LengthFwd = 17
  LengthRev = 0
  Solid = true
  Symmetric = true
FEATURE [Part::Extrusion] Extrude051  label="Extrude buco per perno blocco neopixel"
  Base = -> Sketch048
  Dir = (0,-1,2e-16)
  DirMode = 2
  FaceMakerClass = Part::FaceMakerBullseye
  FaceMakerMode = 3
  LengthFwd = 17
  LengthRev = 0
  Solid = true
  Symmetric = true
FEATURE [Sketcher::SketchObject] Sketch049  label="rinforzi esterni per corpo neopoixel"
  ArcFitTolerance = 1e-06
  AttachmentSupport = -> [XZ_Plane002]
  ExternalGeometry = -> [Sketch045]
  FullyConstrained = true
  MakeInternals = false
  MapMode = 5
  Placement = pos=(0,0,0) rot=(1,0,0;1.5708rad)
  sketch-geometry (8):
    g0: LineSegment StartX=1 StartY=-4.1 StartZ=0 EndX=2 EndY=-4.1 EndZ=0
    g1: LineSegment StartX=2 StartY=-4.1 StartZ=0 EndX=2 EndY=-5.1 EndZ=0
    g2: LineSegment StartX=2 StartY=-5.1 StartZ=0 EndX=1 EndY=-5.1 EndZ=0
    g3: LineSegment StartX=1 StartY=-5.1 StartZ=0 EndX=1 EndY=-4.1 EndZ=0
    g4: LineSegment StartX=1 StartY=5.1 StartZ=0 EndX=2 EndY=5.1 EndZ=0
    g5: LineSegment StartX=2 StartY=5.1 StartZ=0 EndX=2 EndY=4.1 EndZ=0
    g6: LineSegment StartX=2 StartY=4.1 StartZ=0 EndX=1 EndY=4.1 EndZ=0
    g7: LineSegment StartX=1 StartY=4.1 StartZ=0 EndX=1 EndY=5.1 EndZ=0
  constraints (24):
    c: Horizontal(g0)
    c: Coincident(g1,g0)
    c: Vertical(g1)
    c: Coincident(g2,g1)
    c: Horizontal(g2)
    c: Coincident(g3,g2)
    c: Coincident(g3,g0)
    c: Vertical(g3)
    c: Horizontal(g4)
    c: Coincident(g5,g4)
    c: Vertical(g5)
    c: Coincident(g6,g5)
    c: Horizontal(g6)
    c: Coincident(g7,g6)
    c: Coincident(g7,g4)
    c: Vertical(g7)
    c: DistanceX(g4,g4) = 1
    c: DistanceY(g5,g5) = 1
    c: DistanceX(g0,g0) = 1
    c: DistanceY(g1,g1) = 1
    c: DistanceX(g-3,g4) = 1
    c: DistanceY(g-3,g4) = 0
    c: DistanceX(g-4,g2) = 1
    c: DistanceY(g2,g-4) = 0
FEATURE [Part::Extrusion] Extrude052  label="Extrude rinforzi esterni per corpo neopoixel"
  Base = -> Sketch049
  Dir = (0,-1,2e-16)
  DirMode = 2
  FaceMakerClass = Part::FaceMakerBullseye
  FaceMakerMode = 3
  LengthFwd = 17
  LengthRev = 0
  Solid = true
  Symmetric = true
FEATURE [Part::Cut] Cut030
  Base = -> Extrude048
  Refine = true
  Tool = -> Extrude050
FEATURE [Part::Cut] Cut031
  Base = -> Cut030
  Refine = true
  Tool = -> Extrude049
FEATURE [Part::Cut] Cut032
  Base = -> Cut031
  Refine = true
  Tool = -> Extrude051
FEATURE [Part::MultiFuse] Fusion001  label="fusion neopixel"
  Refine = true
  Shapes = -> [Cut032,Extrude052]
FEATURE [Sketcher::SketchObject] Sketch052  label="scavo saldature driver solenoide"
  ArcFitTolerance = 1e-06
  AttachmentSupport = -> [XZ_Plane]
  ExternalGeometry = -> [Sketch038]
  FullyConstrained = true
  MakeInternals = false
  MapMode = 5
  Placement = pos=(0,0,0) rot=(1,0,0;1.5708rad)
  sketch-geometry (4):
    g0: LineSegment StartX=-196.56 StartY=-9.74706 StartZ=0 EndX=-198.25 EndY=-13.3723 EndZ=0
    g1: LineSegment StartX=-198.25 StartY=-13.3723 StartZ=0 EndX=-196.8 EndY=-14.0485 EndZ=0
    g2: LineSegment StartX=-196.8 StartY=-14.0485 StartZ=0 EndX=-195.11 EndY=-10.4232 EndZ=0
    g3: LineSegment StartX=-195.11 StartY=-10.4232 StartZ=0 EndX=-196.56 EndY=-9.74706 EndZ=0
  constraints (11):
    c: Coincident(g1,g0)
    c: Coincident(g2,g1)
    c: Coincident(g3,g2)
    c: Coincident(g3,g0)
    c: Parallel(g2,g0)
    c: Perpendicular(g2,g3)
    c: Perpendicular(g1,g2,g1) = 1.5708
    c: Parallel(g2,g-3)
    c: Distance(g2) = 4
    c: Distance(g3) = 1.6
    c: Coincident(g2,g-3)
FEATURE [Part::Extrusion] Extrude055  label="Extrude scavo saldature driver solenoide"
  Base = -> Sketch052
  Dir = (0,-1,2e-16)
  DirMode = 2
  FaceMakerClass = Part::FaceMakerBullseye
  FaceMakerMode = 3
  LengthFwd = 6
  LengthRev = 0
  Solid = true
  Symmetric = true
FEATURE [Sketcher::SketchObject] Sketch053  label="scavo saldature rumble"
  ArcFitTolerance = 1e-06
  AttachmentSupport = -> [XZ_Plane]
  ExternalGeometry = -> [Sketch019]
  FullyConstrained = true
  MakeInternals = false
  MapMode = 5
  Placement = pos=(0,0,0) rot=(1,0,0;1.5708rad)
  sketch-geometry (4):
    g0: LineSegment StartX=-165.31 StartY=-44.1173 StartZ=0 EndX=-166.547 EndY=-47.9216 EndZ=0
    g1: LineSegment StartX=-166.547 StartY=-47.9216 StartZ=0 EndX=-165.405 EndY=-48.2924 EndZ=0
    g2: LineSegment StartX=-165.405 StartY=-48.2924 StartZ=0 EndX=-164.169 EndY=-44.4881 EndZ=0
    g3: LineSegment StartX=-164.169 StartY=-44.4881 StartZ=0 EndX=-165.31 EndY=-44.1173 EndZ=0
  constraints (11):
    c: Coincident(g1,g0)
    c: Coincident(g2,g1)
    c: Coincident(g3,g2)
    c: Coincident(g3,g0)
    c: Parallel(g0,g2)
    c: Perpendicular(g3,g0)
    c: Perpendicular(g1,g0)
    c: Parallel(g0,g-3)
    c: Distance(g0) = 4
    c: Distance(g1) = 1.2
    c: Coincident(g0,g-3)
FEATURE [Part::Extrusion] Extrude056  label="Extrude scavo saldature rumble"
  Base = -> Sketch053
  Dir = (0,-1,2e-16)
  DirMode = 2
  FaceMakerClass = Part::FaceMakerBullseye
  FaceMakerMode = 3
  LengthFwd = 8.4
  LengthRev = 0
  Solid = true
  Symmetric = true
FEATURE [Part::Cone] Cone  label="Cono"
  Angle = 180
  AttacherType = Attacher::AttachEngine3D
  Height = 15
  Placement = pos=(-176,0,-82.43) rot=(0,0,1;-1.5708rad)
  Radius1 = 12.6
  Radius2 = 10.5
FEATURE [Sketcher::SketchObject] Sketch054  label="scavo saldature alimentatore connettore USB"
  ArcFitTolerance = 1e-06
  AttachmentSupport = -> [XZ_Plane]
  ExternalGeometry = -> [Sketch037]
  FullyConstrained = true
  MakeInternals = false
  MapMode = 5
  Placement = pos=(0,0,0) rot=(1,0,0;1.5708rad)
  sketch-geometry (4):
    g0: LineSegment StartX=-209.575 StartY=-80.4316 StartZ=0 EndX=-210.375 EndY=-80.4316 EndZ=0
    g1: LineSegment StartX=-210.375 StartY=-80.4316 StartZ=0 EndX=-210.375 EndY=-72.4316 EndZ=0
    g2: LineSegment StartX=-210.375 StartY=-72.4316 StartZ=0 EndX=-209.575 EndY=-72.4316 EndZ=0
    g3: LineSegment StartX=-209.575 StartY=-72.4316 StartZ=0 EndX=-209.575 EndY=-80.4316 EndZ=0
  constraints (11):
    c: Horizontal(g0)
    c: Coincident(g1,g0)
    c: Vertical(g1)
    c: Coincident(g2,g1)
    c: Horizontal(g2)
    c: Coincident(g3,g2)
    c: Coincident(g3,g0)
    c: Vertical(g3)
    c: DistanceX(g0,g0) = 0.8
    c: DistanceY(g3,g3) = 8
    c: Coincident(g0,g-4)
FEATURE [Part::Extrusion] Extrude057  label="Extrude scavo saldature alimentatore connettore USB"
  Base = -> Sketch054
  Dir = (0,-1,2e-16)
  DirMode = 2
  FaceMakerClass = Part::FaceMakerBullseye
  FaceMakerMode = 3
  LengthFwd = 11
  LengthRev = 0
  Solid = true
  Symmetric = true
FEATURE [Sketcher::SketchObject] Sketch055  label="buco interno per micro switch"
  ArcFitTolerance = 1e-06
  AttachmentSupport = -> [XZ_Plane]
  ExternalGeometry = -> [Sketch]
  FullyConstrained = true
  MakeInternals = false
  MapMode = 5
  Placement = pos=(0,0,0) rot=(1,0,0;1.5708rad)
  sketch-geometry (11):
    g0: LineSegment [constr] StartX=-194.483 StartY=34.2854 StartZ=0 EndX=-196.022 EndY=30.0568 EndZ=0
    g1: LineSegment [constr] StartX=-196.022 StartY=30.0568 StartZ=0 EndX=-197.561 EndY=25.8282 EndZ=0
    g2: LineSegment [constr] StartX=-196.022 StartY=30.0568 StartZ=0 EndX=-194.143 EndY=29.3727 EndZ=0
    g3: LineSegment [constr] StartX=-196.022 StartY=30.0568 StartZ=0 EndX=-197.902 EndY=30.7408 EndZ=0
    g4: LineSegment StartX=-196.362 StartY=34.9694 StartZ=0 EndX=-192.604 EndY=33.6014 EndZ=0
    g5: LineSegment StartX=-199.441 StartY=26.5122 StartZ=0 EndX=-195.682 EndY=25.1441 EndZ=0
    g6: LineSegment StartX=-192.604 StartY=33.6014 StartZ=0 EndX=-195.682 EndY=25.1441 EndZ=0
    g7: LineSegment StartX=-196.362 StartY=34.9694 StartZ=0 EndX=-199.441 EndY=26.5122 EndZ=0
    g8: GeomPoint [constr] X=-187.821 Y=29.2 Z=0
    g9: LineSegment [constr] StartX=-188.505 StartY=27.3206 StartZ=0 EndX=-196.022 EndY=30.0568 EndZ=0
    g10: LineSegment [constr] StartX=-187.821 StartY=29.2 StartZ=0 EndX=-188.505 EndY=27.3206 EndZ=0
  constraints (27):
    c: Coincident(g2,g0)
    c: Parallel(g0,g-3)
    c: Tangent(g1,g0) = -1.5708
    c: Perpendicular(g0,g2)
    c: Tangent(g2,g3)
    c: Distance(g0,g1) = 9
    c: Equal(g0,g1)
    c: Distance(g3,g2) = 4
    c: Equal(g2,g3)
    c: Parallel(g3,g4)
    c: Symmetric(g4,g4,g0)
    c: Parallel(g6,g1)
    c: Parallel(g7,g1)
    c: Symmetric(g6,g6,g2)
    c: Symmetric(g5,g5,g1)
    c: Symmetric(g7,g7,g3)
    c: Coincident(g7,g4)
    c: Coincident(g6,g4)
    c: Coincident(g5,g6)
    c: Symmetric(g-3,g-3,g8)
    c: Perpendicular(g-3,g9)
    c: Distance(g9) = 8
    c: Coincident(g3,g9)
    c: Coincident(g10,g8)
    c: Parallel(g10,g-3)
    c: Distance(g10) = 2
    c: Coincident(g10,g9)
FEATURE [Part::Extrusion] Extrude058  label="Extrude buco interno per micro switch sinistro"
  Base = -> Sketch055
  Dir = (0,-1,2e-16)
  DirMode = 2
  FaceMakerClass = Part::FaceMakerBullseye
  FaceMakerMode = 3
  LengthFwd = 9
  LengthRev = 0
  Placement = pos=(0,10.6,0) rot=(0,0,1;0rad)
  Solid = true
  Symmetric = false
FEATURE [Sketcher::SketchObject] Sketch056  label="buco esterno per micro switch"
  ArcFitTolerance = 1e-06
  AttachmentSupport = -> [XZ_Plane]
  ExternalGeometry = -> [Sketch055]
  FullyConstrained = true
  MakeInternals = false
  MapMode = 5
  Placement = pos=(0,0,0) rot=(1,0,0;1.5708rad)
  sketch-geometry (17):
    g0: GeomPoint [constr] X=-194.143 Y=29.3727 Z=0
    g1: GeomPoint [constr] X=-194.483 Y=34.2854 Z=0
    g2: GeomPoint [constr] X=-197.902 Y=30.7408 Z=0
    g3: GeomPoint [constr] X=-197.561 Y=25.8282 Z=0
    g4: GeomPoint [constr] X=-196.022 Y=30.0568 Z=0
    g5: LineSegment [constr] StartX=-194.483 StartY=34.2854 StartZ=0 EndX=-196.022 EndY=30.0568 EndZ=0
    g6: LineSegment [constr] StartX=-196.022 StartY=30.0568 StartZ=0 EndX=-197.561 EndY=25.8282 EndZ=0
    g7: LineSegment [constr] StartX=-197.902 StartY=30.7408 StartZ=0 EndX=-196.022 EndY=30.0568 EndZ=0
    g8: LineSegment [constr] StartX=-196.022 StartY=30.0568 StartZ=0 EndX=-194.143 EndY=29.3727 EndZ=0
    g9: LineSegment [constr] StartX=-195.338 StartY=31.9362 StartZ=0 EndX=-196.022 EndY=30.0568 EndZ=0
    g10: LineSegment [constr] StartX=-196.022 StartY=30.0568 StartZ=0 EndX=-196.706 EndY=28.1774 EndZ=0
    g11: LineSegment [constr] StartX=-196.022 StartY=30.0568 StartZ=0 EndX=-196.821 EndY=30.3475 EndZ=0
    g12: LineSegment [constr] StartX=-196.022 StartY=30.0568 StartZ=0 EndX=-195.223 EndY=29.7661 EndZ=0
    g13: LineSegment StartX=-194.539 StartY=31.6454 StartZ=0 EndX=-195.907 EndY=27.8867 EndZ=0
    g14: LineSegment StartX=-196.137 StartY=32.2269 StartZ=0 EndX=-197.505 EndY=28.4681 EndZ=0
    g15: LineSegment StartX=-196.137 StartY=32.2269 StartZ=0 EndX=-194.539 EndY=31.6454 EndZ=0
    g16: LineSegment StartX=-197.505 StartY=28.4681 StartZ=0 EndX=-195.907 EndY=27.8867 EndZ=0
  constraints (34):
    c: Symmetric(g-5,g-5,g1)
    c: Symmetric(g-5,g-6,g0)
    c: Symmetric(g-6,g-6,g3)
    c: Symmetric(g-5,g-6,g2)
    c: Coincident(g5,g1)
    c: Coincident(g5,g4)
    c: Coincident(g6,g4)
    c: Coincident(g6,g3)
    c: Equal(g5,g6)
    c: Coincident(g7,g2)
    c: Coincident(g7,g4)
    c: Coincident(g8,g4)
    c: Coincident(g8,g0)
    c: Equal(g7,g8)
    c: Coincident(g11,g9)
    c: Coincident(g12,g9)
    c: Tangent(g10,g9) = -1.5708
    c: Perpendicular(g11,g9)
    c: Parallel(g9,g-4)
    c: Equal(g9,g10)
    c: Parallel(g12,g11)
    c: Equal(g11,g12)
    c: Distance(g11,g12) = 1.7
    c: Distance(g9,g10) = 4
    c: Symmetric(g13,g13,g12)
    c: Parallel(g13,g9)
    c: Symmetric(g14,g14,g11)
    c: Symmetric(g15,g15,g9)
    c: Parallel(g15,g11)
    c: Symmetric(g16,g16,g10)
    c: Coincident(g16,g14)
    c: Coincident(g15,g14)
    c: Coincident(g13,g15)
    c: Coincident(g9,g4)
FEATURE [Part::Extrusion] Extrude059  label="Extrude buco esterno per micro switch sinistro"
  Base = -> Sketch056
  Dir = (0,-1,2e-16)
  DirMode = 2
  FaceMakerClass = Part::FaceMakerBullseye
  FaceMakerMode = 3
  LengthFwd = 2
  LengthRev = 0
  Placement = pos=(0,12.6,0) rot=(0,0,1;0rad)
  Solid = true
  Symmetric = false
FEATURE [Sketcher::SketchObject] Sketch057  label="buco interno per SWITCH"
  ArcFitTolerance = 1e-06
  AttachmentSupport = -> [XZ_Plane]
  ExternalGeometry = -> [Sketch]
  FullyConstrained = true
  MakeInternals = false
  MapMode = 5
  Placement = pos=(0,0,0) rot=(1,0,0;1.5708rad)
  sketch-geometry (10):
    g0: GeomPoint [constr] X=-187.821 Y=29.2 Z=0
    g1: LineSegment [constr] StartX=-188.505 StartY=27.3206 StartZ=0 EndX=-193.203 EndY=29.0307 EndZ=0
    g2: LineSegment [constr] StartX=-190.809 StartY=35.6086 StartZ=0 EndX=-195.597 EndY=22.4529 EndZ=0
    g3: GeomPoint [constr] X=-193.203 Y=29.0307 Z=0
    g4: LineSegment [constr] StartX=-196.492 StartY=30.2278 StartZ=0 EndX=-189.914 EndY=27.8336 EndZ=0
    g5: LineSegment StartX=-194.098 StartY=36.8056 StartZ=0 EndX=-187.52 EndY=34.4115 EndZ=0
    g6: LineSegment StartX=-194.098 StartY=36.8056 StartZ=0 EndX=-198.886 EndY=23.6499 EndZ=0
    g7: LineSegment StartX=-187.52 StartY=34.4115 StartZ=0 EndX=-192.308 EndY=21.2558 EndZ=0
    g8: LineSegment StartX=-198.886 StartY=23.6499 StartZ=0 EndX=-192.308 EndY=21.2558 EndZ=0
    g9: LineSegment [constr] StartX=-187.821 StartY=29.2 StartZ=0 EndX=-188.505 EndY=27.3206 EndZ=0
  constraints (23):
    c: Symmetric(g-3,g-3,g0)
    c: Perpendicular(g1,g-3)
    c: Parallel(g2,g-3)
    c: Symmetric(g2,g2,g3)
    c: Perpendicular(g2,g4)
    c: Symmetric(g4,g4,g3)
    c: Distance(g2) = 14
    c: Distance(g4) = 7
    c: Distance(g1) = 5
    c: Parallel(g5,g4)
    c: Parallel(g7,g2)
    c: Symmetric(g5,g5,g2)
    c: Symmetric(g6,g6,g4)
    c: Symmetric(g7,g7,g4)
    c: Symmetric(g8,g8,g2)
    c: Coincident(g6,g5)
    c: Coincident(g7,g5)
    c: Coincident(g8,g7)
    c: Coincident(g3,g1)
    c: Coincident(g9,g0)
    c: Parallel(g9,g-3)
    c: Distance(g9) = 2
    c: Coincident(g1,g9)
FEATURE [Sketcher::SketchObject] Sketch058  label="buco esterno per SWITCH"
  ArcFitTolerance = 1e-06
  AttachmentSupport = -> [XZ_Plane]
  ExternalGeometry = -> [Sketch057]
  FullyConstrained = true
  MakeInternals = false
  MapMode = 5
  Placement = pos=(0,0,0) rot=(1,0,0;1.5708rad)
  sketch-geometry (12):
    g0: GeomPoint [constr] X=-190.809 Y=35.6086 Z=0
    g1: GeomPoint [constr] X=-196.492 Y=30.2278 Z=0
    g2: GeomPoint [constr] X=-189.914 Y=27.8336 Z=0
    g3: GeomPoint [constr] X=-195.597 Y=22.4529 Z=0
    g4: GeomPoint [constr] X=-193.203 Y=29.0307 Z=0
    g5: LineSegment [constr] StartX=-192.006 StartY=32.3196 StartZ=0 EndX=-194.4 EndY=25.7418 EndZ=0
    g6: GeomPoint [constr] X=-193.203 Y=29.0307 Z=0
    g7: LineSegment [constr] StartX=-195.082 StartY=29.7148 StartZ=0 EndX=-191.324 EndY=28.3467 EndZ=0
    g8: LineSegment StartX=-193.885 StartY=33.0037 StartZ=0 EndX=-190.127 EndY=31.6356 EndZ=0
    g9: LineSegment StartX=-190.127 StartY=31.6356 StartZ=0 EndX=-192.521 EndY=25.0578 EndZ=0
    g10: LineSegment StartX=-196.28 StartY=26.4258 StartZ=0 EndX=-192.521 EndY=25.0578 EndZ=0
    g11: LineSegment StartX=-193.885 StartY=33.0037 StartZ=0 EndX=-196.28 EndY=26.4258 EndZ=0
  constraints (21):
    c: Symmetric(g-6,g-6,g3)
    c: Symmetric(g-4,g-6,g2)
    c: Symmetric(g-5,g-4,g0)
    c: Symmetric(g-5,g-6,g1)
    c: Symmetric(g1,g2,g4)
    c: Parallel(g5,g-4)
    c: Symmetric(g5,g5,g6)
    c: Perpendicular(g7,g5)
    c: Symmetric(g7,g7,g6)
    c: Distance(g5) = 7
    c: Distance(g7) = 4
    c: Parallel(g8,g7)
    c: Parallel(g11,g5)
    c: Symmetric(g8,g8,g5)
    c: Symmetric(g9,g9,g7)
    c: Symmetric(g10,g10,g5)
    c: Symmetric(g11,g11,g7)
    c: Coincident(g11,g8)
    c: Coincident(g9,g8)
    c: Coincident(g9,g10)
    c: Coincident(g6,g4)
FEATURE [Part::Extrusion] Extrude060  label="Extrude buco interno per SWITCH destro"
  Base = -> Sketch057
  Dir = (0,-1,2e-16)
  DirMode = 2
  FaceMakerClass = Part::FaceMakerBullseye
  FaceMakerMode = 3
  LengthFwd = 13.2
  LengthRev = 0
  Placement = pos=(0,2.6,0) rot=(0,0,1;0rad)
  Solid = true
  Symmetric = false
FEATURE [Part::Extrusion] Extrude061  label="Extrude buco esterno per SWITCH destro"
  Base = -> Sketch058
  Dir = (0,-1,2e-16)
  DirMode = 2
  FaceMakerClass = Part::FaceMakerBullseye
  FaceMakerMode = 3
  LengthFwd = 2
  LengthRev = 0
  Placement = pos=(0,-10.6,0) rot=(0,0,1;0rad)
  Solid = true
  Symmetric = false
FEATURE [Sketcher::SketchObject] Sketch059  label="buco per spazio introduzione SWITCH"
  ArcFitTolerance = 1e-06
  AttachmentSupport = -> [XZ_Plane]
  ExternalGeometry = -> [Sketch057,Sketch010]
  FullyConstrained = true
  MakeInternals = false
  MapMode = 5
  Placement = pos=(0,0,0) rot=(1,0,0;1.5708rad)
  sketch-geometry (8):
    g0: LineSegment [constr] StartX=-201.368 StartY=36.3521 StartZ=0 EndX=-195.094 EndY=34.0687 EndZ=0
    g1: LineSegment [constr] StartX=-194.098 StartY=36.8056 StartZ=0 EndX=-195.094 EndY=34.0687 EndZ=0
    g2: LineSegment StartX=-198.658 StartY=24.2771 StartZ=0 EndX=-199.654 EndY=21.5401 EndZ=0
    g3: LineSegment StartX=-199.654 StartY=21.5401 StartZ=0 EndX=-181.196 EndY=14.822 EndZ=0
    g4: LineSegment StartX=-181.196 StartY=14.822 StartZ=0 EndX=-180.2 EndY=17.559 EndZ=0
    g5: LineSegment StartX=-180.2 StartY=17.559 StartZ=0 EndX=-198.658 EndY=24.2771 EndZ=0
    g6: LineSegment [constr] StartX=-204.932 StartY=26.5605 StartZ=0 EndX=-198.658 EndY=24.2771 EndZ=0
    g7: LineSegment [constr] StartX=-198.658 StartY=24.2771 StartZ=0 EndX=-199.654 EndY=21.5401 EndZ=0
  constraints (20):
    c: Parallel(g1,g-3)
    c: Parallel(g0,g-4)
    c: Coincident(g0,g-4)
    c: Coincident(g1,g-3)
    c: Coincident(g0,g1)
    c: Coincident(g3,g2)
    c: Coincident(g4,g3)
    c: Coincident(g5,g4)
    c: Coincident(g5,g2)
    c: Parallel(g5,g-5)
    c: Parallel(g3,g-5)
    c: Parallel(g4,g-6)
    c: DistanceX(g-6,g4) = 0
    c: Coincident(g6,g-5)
    c: Equal(g6,g0)
    c: Coincident(g7,g6)
    c: Equal(g7,g1)
    c: Tangent(g7,g-3)
    c: Coincident(g2,g6)
    c: Coincident(g2,g7)
FEATURE [Part::Extrusion] Extrude062  label="Extrude buco per spazio introduzione SWITCH"
  Base = -> Sketch059
  Dir = (0,-1,2e-16)
  DirMode = 2
  FaceMakerClass = Part::FaceMakerBullseye
  FaceMakerMode = 3
  LengthFwd = 13.2
  LengthRev = 0
  Solid = true
  Symmetric = true
FEATURE [Part::Extrusion] Extrude063  label="Extrude buco interno per SWITCH sinistro"
  Base = -> Sketch057
  Dir = (0,-1,2e-16)
  DirMode = 2
  FaceMakerClass = Part::FaceMakerBullseye
  FaceMakerMode = 3
  LengthFwd = 13.2
  LengthRev = 0
  Placement = pos=(0,10.6,0) rot=(0,0,1;0rad)
  Solid = true
  Symmetric = false
FEATURE [Part::Extrusion] Extrude064  label="Extrude buco esterno per SWITCH sinistro"
  Base = -> Sketch058
  Dir = (0,-1,2e-16)
  DirMode = 2
  FaceMakerClass = Part::FaceMakerBullseye
  FaceMakerMode = 3
  LengthFwd = 2
  LengthRev = 0
  Placement = pos=(0,12.6,0) rot=(0,0,1;0rad)
  Solid = true
  Symmetric = false
FEATURE [Sketcher::SketchObject] Sketch060  label="prova spazio switch"
  ArcFitTolerance = 1e-06
  AttachmentSupport = -> [XY_Plane003]
  FullyConstrained = true
  MakeInternals = false
  MapMode = 5
  sketch-geometry (12):
    g0: LineSegment StartX=-7.5 StartY=10 StartZ=0 EndX=-7.5 EndY=-10 EndZ=0
    g1: LineSegment StartX=-7.5 StartY=-10 StartZ=0 EndX=7.5 EndY=-10 EndZ=0
    g2: LineSegment StartX=7.5 StartY=-10 StartZ=0 EndX=7.5 EndY=10 EndZ=0
    g3: LineSegment StartX=7.5 StartY=10 StartZ=0 EndX=-7.5 EndY=10 EndZ=0
    g4: GeomPoint [constr] X=0 Y=0 Z=0
    g5: LineSegment StartX=-2.95 StartY=-5.55 StartZ=0 EndX=2.95 EndY=-5.55 EndZ=0
    g6: LineSegment StartX=2.95 StartY=-5.55 StartZ=0 EndX=2.95 EndY=5.55 EndZ=0
    g7: LineSegment StartX=2.95 StartY=5.55 StartZ=0 EndX=-2.95 EndY=5.55 EndZ=0
    g8: LineSegment StartX=-2.95 StartY=5.55 StartZ=0 EndX=-2.95 EndY=-5.55 EndZ=0
    g9: GeomPoint [constr] X=0 Y=0 Z=0
    g10: Circle CenterX=0 CenterY=7.75 CenterZ=0 NormalX=0 NormalY=0 NormalZ=1 AngleXU=0 Radius=1.6
    g11: Circle CenterX=0 CenterY=-7.75 CenterZ=0 NormalX=0 NormalY=0 NormalZ=1 AngleXU=0 Radius=1.6
  constraints (29):
    c: Coincident(g0,g1)
    c: Coincident(g1,g2)
    c: Coincident(g2,g3)
    c: Coincident(g3,g0)
    c: Vertical(g0)
    c: Vertical(g2)
    c: Horizontal(g1)
    c: Horizontal(g3)
    c: Symmetric(g2,g0,g4)
    c: Coincident(g4,g-1)
    c: Distance(g3) = 15
    c: Distance(g2) = 20
    c: Coincident(g5,g6)
    c: Coincident(g6,g7)
    c: Coincident(g7,g8)
    c: Coincident(g8,g5)
    c: Horizontal(g5)
    c: Horizontal(g7)
    c: Vertical(g6)
    c: Vertical(g8)
    c: Symmetric(g7,g5,g9)
    c: Coincident(g9,g4)
    c: Distance(g7) = 5.9
    c: Distance(g6) = 11.1
    c: Diameter(g10) = 3.2
    c: Equal(g10,g11)
    c: Symmetric(g10,g11,g-1)
    c: PointOnObject(g10,g-2)
    c: Distance(g10,g11) = 15.5
FEATURE [Part::Extrusion] Extrude065  label="Extrude prova spazio switch"
  Base = -> Sketch060
  Dir = (0,0,1)
  DirMode = 2
  FaceMakerClass = Part::FaceMakerBullseye
  FaceMakerMode = 3
  LengthFwd = 5
  LengthRev = 0
  Solid = true
  Symmetric = false
FEATURE [Sketcher::SketchObject] Sketch061  label="struttura esterna blocco switch"
  ArcFitTolerance = 1e-06
  AttachmentSupport = -> [XZ_Plane003]
  FullyConstrained = true
  MakeInternals = false
  MapMode = 5
  Placement = pos=(0,0,0) rot=(1,0,0;1.5708rad)
  sketch-geometry (5):
    g0: LineSegment StartX=-1 StartY=-5.1 StartZ=0 EndX=1 EndY=-5.1 EndZ=0
    g1: LineSegment StartX=1 StartY=-5.1 StartZ=0 EndX=1 EndY=5.1 EndZ=0
    g2: LineSegment StartX=1 StartY=5.1 StartZ=0 EndX=-1 EndY=5.1 EndZ=0
    g3: LineSegment StartX=-1 StartY=5.1 StartZ=0 EndX=-1 EndY=-5.1 EndZ=0
    g4: GeomPoint [constr] X=0 Y=0 Z=0
  constraints (12):
    c: Coincident(g0,g1)
    c: Coincident(g1,g2)
    c: Coincident(g2,g3)
    c: Coincident(g3,g0)
    c: Horizontal(g0)
    c: Horizontal(g2)
    c: Vertical(g1)
    c: Vertical(g3)
    c: Symmetric(g2,g0,g4)
    c: Distance(g1,g3) = 2
    c: Distance(g0,g2) = 10.2
    c: Coincident(g4,g-1)
FEATURE [Part::Extrusion] Extrude066  label="Extrude struttura esterna blocco switch"
  Base = -> Sketch061
  Dir = (0,-1,2e-16)
  DirMode = 2
  FaceMakerClass = Part::FaceMakerBullseye
  FaceMakerMode = 3
  LengthFwd = 16.8
  LengthRev = 0
  Solid = true
  Symmetric = true
FEATURE [Sketcher::SketchObject] Sketch062  label="struttura interna blocco switch"
  ArcFitTolerance = 1e-06
  AttachmentSupport = -> [XZ_Plane003]
  ExternalGeometry = -> [Sketch061]
  FullyConstrained = true
  MakeInternals = false
  MapMode = 5
  Placement = pos=(0,0,0) rot=(1,0,0;1.5708rad)
  sketch-geometry (5):
    g0: LineSegment StartX=-1 StartY=3.1 StartZ=0 EndX=-1 EndY=-3.1 EndZ=0
    g1: LineSegment StartX=-1 StartY=-3.1 StartZ=0 EndX=1 EndY=-3.1 EndZ=0
    g2: LineSegment StartX=1 StartY=-3.1 StartZ=0 EndX=1 EndY=3.1 EndZ=0
    g3: LineSegment StartX=1 StartY=3.1 StartZ=0 EndX=-1 EndY=3.1 EndZ=0
    g4: GeomPoint [constr] X=0 Y=0 Z=0
  constraints (12):
    c: Coincident(g0,g1)
    c: Coincident(g1,g2)
    c: Coincident(g2,g3)
    c: Coincident(g3,g0)
    c: Vertical(g0)
    c: Vertical(g2)
    c: Horizontal(g1)
    c: Horizontal(g3)
    c: Symmetric(g2,g0,g4)
    c: Coincident(g4,g-1)
    c: Distance(g0) = 6.2
    c: Equal(g3,g-3)
FEATURE [Part::Extrusion] Extrude067  label="Extrude struttura interna blocco switch"
  Base = -> Sketch062
  Dir = (0,-1,2e-16)
  DirMode = 2
  FaceMakerClass = Part::FaceMakerBullseye
  FaceMakerMode = 3
  LengthFwd = 12.8
  LengthRev = 0
  Solid = true
  Symmetric = true
FEATURE [Part::Cut] Cut036  label="struttura blocco switch"
  Base = -> Extrude066
  Refine = true
  Tool = -> Extrude067
FEATURE [Sketcher::SketchObject] Sketch063  label="blocchi tra switch"
  ArcFitTolerance = 1e-06
  AttachmentSupport = -> [XZ_Plane003]
  ExternalGeometry = -> [Sketch061,Sketch062]
  FullyConstrained = true
  MakeInternals = false
  MapMode = 5
  Placement = pos=(0,0,0) rot=(1,0,0;1.5708rad)
  sketch-geometry (8):
    g0: LineSegment StartX=-3 StartY=5.1 StartZ=0 EndX=-1 EndY=5.1 EndZ=0
    g1: LineSegment StartX=-1 StartY=5.1 StartZ=0 EndX=-1 EndY=3.1 EndZ=0
    g2: LineSegment StartX=-1 StartY=3.1 StartZ=0 EndX=-3 EndY=3.1 EndZ=0
    g3: LineSegment StartX=-3 StartY=3.1 StartZ=0 EndX=-3 EndY=5.1 EndZ=0
    g4: LineSegment StartX=-3 StartY=-3.1 StartZ=0 EndX=-1 EndY=-3.1 EndZ=0
    g5: LineSegment StartX=-1 StartY=-3.1 StartZ=0 EndX=-1 EndY=-5.1 EndZ=0
    g6: LineSegment StartX=-1 StartY=-5.1 StartZ=0 EndX=-3 EndY=-5.1 EndZ=0
    g7: LineSegment StartX=-3 StartY=-5.1 StartZ=0 EndX=-3 EndY=-3.1 EndZ=0
  constraints (20):
    c: Horizontal(g0)
    c: Coincident(g1,g0)
    c: Coincident(g2,g1)
    c: Horizontal(g2)
    c: Coincident(g3,g2)
    c: Coincident(g3,g0)
    c: Vertical(g3)
    c: Horizontal(g4)
    c: Coincident(g5,g4)
    c: Coincident(g6,g5)
    c: Horizontal(g6)
    c: Coincident(g7,g6)
    c: Coincident(g7,g4)
    c: Vertical(g7)
    c: Coincident(g0,g-4)
    c: Coincident(g1,g-5)
    c: Coincident(g4,g-6)
    c: Coincident(g5,g-7)
    c: Distance(g0) = 2
    c: Distance(g4) = 2
FEATURE [PartDesign::Body] Body003  label="blocco switch e neopixel"
  AllowCompound = false
  Group = -> [Sketch060,Sketch061,Sketch062,Sketch063]
  Origin = -> Origin003
FEATURE [Part::Extrusion] Extrude068  label="Extrude blocchi tra switch"
  Base = -> Sketch063
  Dir = (0,-1,2e-16)
  DirMode = 2
  FaceMakerClass = Part::FaceMakerBullseye
  FaceMakerMode = 3
  LengthFwd = 7.6
  LengthRev = 0
  Solid = true
  Symmetric = true
FEATURE [Part::MultiFuse] Fusion002  label="Fusion blocco switch"
  Refine = true
  Shapes = -> [Cut036,Extrude068]
FEATURE [Sketcher::SketchObject] Sketch066  label="piano per rampino"
  ArcFitTolerance = 1e-06
  AttachmentSupport = -> [XZ_Plane002]
  ExternalGeometry = -> [Sketch045]
  FullyConstrained = true
  MakeInternals = false
  MapMode = 5
  Placement = pos=(0,0,0) rot=(1,0,0;1.5708rad)
  sketch-geometry (4):
    g0: LineSegment StartX=5.4 StartY=5.1 StartZ=0 EndX=5.4 EndY=3.9 EndZ=0
    g1: LineSegment StartX=5.4 StartY=3.9 StartZ=0 EndX=7 EndY=3.9 EndZ=0
    g2: LineSegment StartX=7 StartY=3.9 StartZ=0 EndX=7 EndY=5.1 EndZ=0
    g3: LineSegment StartX=7 StartY=5.1 StartZ=0 EndX=5.4 EndY=5.1 EndZ=0
  constraints (11):
    c: Coincident(g0,g1)
    c: Coincident(g1,g2)
    c: Coincident(g2,g3)
    c: Coincident(g3,g0)
    c: Vertical(g0)
    c: Vertical(g2)
    c: Horizontal(g1)
    c: Horizontal(g3)
    c: Distance(g0,g2) = 1.6
    c: Distance(g1,g3) = 1.2
    c: Coincident(g2,g-3)
FEATURE [Sketcher::SketchObject] Sketch064  label="rampini_per_serraggio_struttura"
  ArcFitTolerance = 1e-06
  AttachmentSupport = -> [XZ_Plane002]
  ExternalGeometry = -> [Sketch066,Sketch045]
  FullyConstrained = true
  MakeInternals = false
  MapMode = 5
  Placement = pos=(0,0,0) rot=(1,0,0;1.5708rad)
  sketch-geometry (7):
    g0: LineSegment StartX=7 StartY=5.1 StartZ=0 EndX=7 EndY=3.9 EndZ=0
    g1: LineSegment StartX=7 StartY=3.9 StartZ=0 EndX=9 EndY=3.9 EndZ=0
    g2: LineSegment StartX=7 StartY=5.1 StartZ=0 EndX=7 EndY=5.1 EndZ=0
    g3: LineSegment StartX=7 StartY=5.1 StartZ=0 EndX=7 EndY=7.5 EndZ=0
    g4: LineSegment StartX=9 StartY=5.1 StartZ=0 EndX=9 EndY=3.9 EndZ=0
    g5: LineSegment StartX=7 StartY=7.5 StartZ=0 EndX=9 EndY=7.5 EndZ=0
    g6: LineSegment StartX=9 StartY=7.5 StartZ=0 EndX=9 EndY=5.1 EndZ=0
  constraints (20):
    c: Vertical(g0)
    c: Coincident(g1,g0)
    c: Horizontal(g1)
    c: Coincident(g2,g0)
    c: Horizontal(g2)
    c: Coincident(g3,g2)
    c: Vertical(g3)
    c: Coincident(g5,g3)
    c: Coincident(g4,g6)
    c: Coincident(g4,g1)
    c: Vertical(g4)
    c: Coincident(g0,g-3)
    c: DistanceY(g-4,g3) = 2.4
    c: DistanceX(g1,g1) = 2
    c: DistanceY(g2,g6) = 0
    c: DistanceX(g2,g2) = 0
    c: DistanceY(g0,g0) = 1.2
    c: Coincident(g5,g6)
    c: Horizontal(g5)
    c: Vertical(g6)
FEATURE [Part::Extrusion] Extrude070  label="Extrude piano per rampino"
  Base = -> Sketch066
  Dir = (0,-1,2e-16)
  DirMode = 2
  FaceMakerClass = Part::FaceMakerBullseye
  FaceMakerMode = 3
  LengthFwd = 17
  LengthRev = 0
  Solid = true
  Symmetric = true
FEATURE [Part::Extrusion] Extrude071  label="Extrude rampini_per_serraggio_struttura"
  Base = -> Sketch064
  Dir = (0,-1,2e-16)
  DirMode = 2
  FaceMakerClass = Part::FaceMakerBullseye
  FaceMakerMode = 3
  LengthFwd = 5
  LengthRev = 0
  Solid = true
  Symmetric = true
FEATURE [Part::MultiFuse] Fusion003  label="Fusion supporto neopixel completo"
  Refine = true
  Shapes = -> [Fusion001,Extrude070,Extrude071]
FEATURE [Sketcher::SketchObject] Sketch067  label="perno per blocco switch"
  ArcFitTolerance = 1e-06
  AttachmentSupport = -> [XZ_Plane]
  ExternalGeometry = -> [Sketch,Sketch010]
  FullyConstrained = true
  MakeInternals = false
  MapMode = 5
  Placement = pos=(0,0,0) rot=(1,0,0;1.5708rad)
  sketch-geometry (14):
    g0: LineSegment StartX=-191.073 StartY=24.9429 StartZ=0 EndX=-185.81 EndY=23.0276 EndZ=0
    g1: LineSegment StartX=-183.76 StartY=23.9839 StartZ=0 EndX=-182.392 EndY=27.7427 EndZ=0
    g2: LineSegment StartX=-183.348 StartY=29.7934 StartZ=0 EndX=-188.61 EndY=31.7087 EndZ=0
    g3: LineSegment StartX=-188.61 StartY=31.7087 StartZ=0 EndX=-191.073 EndY=24.9429 EndZ=0
    g4: GeomPoint [constr] X=-186.459 Y=27.0946 Z=0
    g5: LineSegment StartX=-189.022 StartY=25.8992 StartZ=0 EndX=-185.263 EndY=24.5311 EndZ=0
    g6: LineSegment StartX=-185.263 StartY=24.5311 StartZ=0 EndX=-183.895 EndY=28.2899 EndZ=0
    g7: LineSegment StartX=-183.895 StartY=28.2899 StartZ=0 EndX=-187.654 EndY=29.658 EndZ=0
    g8: LineSegment StartX=-187.654 StartY=29.658 StartZ=0 EndX=-189.022 EndY=25.8992 EndZ=0
    g9: GeomPoint [constr] X=-186.459 Y=27.0946 Z=0
    g10: ArcOfCircle CenterX=-185.263 CenterY=24.5311 CenterZ=0 NormalX=0 NormalY=0 NormalZ=1 AngleXU=0 Radius=1.6 StartAngle=4.36332 EndAngle=5.93412
    g11: GeomPoint [constr] X=-184.307 Y=22.4804 Z=0
    g12: ArcOfCircle CenterX=-183.895 CenterY=28.2899 CenterZ=0 NormalX=0 NormalY=0 NormalZ=1 AngleXU=0 Radius=1.6 StartAngle=5.93412 EndAngle=7.50492
    g13: GeomPoint [constr] X=-181.844 Y=29.2462 Z=0
  constraints (30):
    c: Coincident(g2,g3)
    c: Coincident(g3,g0)
    c: Symmetric(g13,g0,g4)
    c: Distance(g11,g3) = 7.2
    c: Distance(g0,g2) = 7.2
    c: Parallel(g3,g1)
    c: Parallel(g2,g0)
    c: Perpendicular(g2,g3)
    c: Coincident(g5,g6)
    c: Coincident(g6,g7)
    c: Coincident(g7,g8)
    c: Coincident(g8,g5)
    c: Symmetric(g7,g5,g9)
    c: Distance(g6,g8) = 4
    c: Distance(g5,g7) = 4
    c: Coincident(g9,g4)
    c: Parallel(g8,g6)
    c: Parallel(g7,g5)
    c: Perpendicular(g7,g8)
    c: Tangent(g8,g-3)
    c: Tangent(g2,g-4)
    c: PointOnObject(g11,g1)
    c: PointOnObject(g11,g0)
    c: Tangent(g1,g10) = -1.5708
    c: Tangent(g0,g10) = -1.5708
    c: PointOnObject(g13,g1)
    c: Tangent(g1,g12) = -1.5708
    c: Tangent(g2,g12) = -1.5708
    c: Equal(g10,g12)
    c: Coincident(g10,g5)
FEATURE [Part::Extrusion] Extrude072  label="Extrude perno per blocco switch"
  Base = -> Sketch067
  Dir = (0,-1,2e-16)
  DirMode = 2
  FaceMakerClass = Part::FaceMakerBullseye
  FaceMakerMode = 3
  LengthFwd = 25.2
  LengthRev = 0
  Solid = true
  Symmetric = true
FEATURE [Part::MultiFuse] Fusion
  Refine = true
  Shapes = -> [Extrude,Sweep,Extrude007,Extrude011,Extrude005,Extrude012,Extrude013,Extrude016,Extrude031,Extrude039,Extrude045,Extrude072]
FEATURE [Part::Cut] Cut
  Base = -> Fusion
  Refine = true
  Tool = -> Extrude001
FEATURE [Part::Cut] Cut001
  Base = -> Cut
  Refine = true
  Tool = -> Extrude004
FEATURE [Part::Cut] Cut002
  Base = -> Cut001
  Refine = true
  Tool = -> Extrude006
FEATURE [Part::Cut] Cut003
  Base = -> Cut002
  Refine = true
  Tool = -> Extrude008
FEATURE [Part::Cut] Cut004
  Base = -> Cut003
  Refine = true
  Tool = -> Extrude009
FEATURE [Part::Cut] Cut005
  Base = -> Cut004
  Refine = true
  Tool = -> Extrude010
FEATURE [Part::Cut] Cut006
  Base = -> Cut005
  Refine = true
  Tool = -> Extrude014
FEATURE [Part::Cut] Cut007
  Base = -> Cut006
  Refine = true
  Tool = -> Extrude015
FEATURE [Part::Cut] Cut008
  Base = -> Cut007
  Refine = true
  Tool = -> Extrude018
FEATURE [Part::Cut] Cut009
  Base = -> Cut008
  Refine = true
  Tool = -> Extrude019
FEATURE [Part::Cut] Cut010
  Base = -> Cut009
  Refine = true
  Tool = -> Extrude020
FEATURE [Part::Cut] Cut011
  Base = -> Cut010
  Refine = true
  Tool = -> Extrude021
FEATURE [Part::Cut] Cut012
  Base = -> Cut011
  Refine = true
  Tool = -> Extrude022
FEATURE [Part::Cut] Cut013
  Base = -> Cut012
  Refine = true
  Tool = -> Extrude023
FEATURE [Part::Cut] Cut014
  Base = -> Cut013
  Refine = true
  Tool = -> Extrude032
FEATURE [Part::Cut] Cut015
  Base = -> Cut014
  Refine = true
  Tool = -> Extrude033
FEATURE [Part::Cut] Cut016
  Base = -> Cut015
  Refine = true
  Tool = -> Extrude034
FEATURE [Part::Cut] Cut017
  Base = -> Cut016
  Refine = true
  Tool = -> Extrude035
FEATURE [Part::Cut] Cut018
  Base = -> Cut017
  Refine = true
  Tool = -> Extrude036
FEATURE [Part::Cut] Cut019
  Base = -> Cut018
  Refine = true
  Tool = -> Extrude037
FEATURE [Part::Cut] Cut020
  Base = -> Cut019
  Refine = true
  Tool = -> Extrude030
FEATURE [Part::Cut] Cut022
  Base = -> Cut020
  Refine = true
  Tool = -> Extrude038
FEATURE [Part::Cut] Cut023
  Base = -> Cut022
  Refine = true
  Tool = -> Extrude041
FEATURE [Part::Cut] Cut024
  Base = -> Cut023
  Refine = true
  Tool = -> Extrude040
FEATURE [Part::Cut] Cut025
  Base = -> Cut024
  Refine = true
  Tool = -> Extrude042
FEATURE [Part::Cut] Cut026
  Base = -> Cut025
  Refine = true
  Tool = -> Extrude043
FEATURE [Part::Cut] Cut027
  Base = -> Cut026
  Refine = true
  Tool = -> Extrude044
FEATURE [Part::Cut] Cut028
  Base = -> Cut027
  Refine = true
  Tool = -> Extrude046
FEATURE [Part::Cut] Cut029
  Base = -> Cut028
  Refine = true
  Tool = -> Extrude047
FEATURE [Part::Cut] Cut033
  Base = -> Cut029
  Refine = true
  Tool = -> Extrude055
FEATURE [Part::Cut] Cut034
  Base = -> Cut033
  Refine = true
  Tool = -> Extrude056
FEATURE [Part::Cut] Cut035
  Base = -> Cut034
  Refine = true
  Tool = -> Extrude057
FEATURE [Part::Cut] Cut037
  Base = -> Cut035
  Refine = true
  Tool = -> Extrude060
FEATURE [Part::Cut] Cut038
  Base = -> Cut037
  Refine = true
  Tool = -> Extrude061
FEATURE [Part::Cut] Cut039
  Base = -> Cut038
  Refine = true
  Tool = -> Extrude063
FEATURE [Part::Cut] Cut040
  Base = -> Cut039
  Refine = true
  Tool = -> Extrude064
FEATURE [Part::Cut] Cut041
  Base = -> Cut040
  Refine = true
  Tool = -> Extrude062
FEATURE [Sketcher::SketchObject] Sketch068  label="base con smusso sopra neopixel"
  ArcFitTolerance = 1e-06
  AttachmentSupport = -> [YZ_Plane002]
  FullyConstrained = true
  MakeInternals = false
  MapMode = 5
  Placement = pos=(0,0,0) rot=(0.57735,0.57735,0.57735;2.0944rad)
  sketch-geometry (5):
    g0: LineSegment StartX=-9.5 StartY=-6.1 StartZ=0 EndX=9.5 EndY=-6.1 EndZ=0
    g1: LineSegment StartX=9.5 StartY=-6.1 StartZ=0 EndX=9.5 EndY=6.1 EndZ=0
    g2: LineSegment StartX=9.5 StartY=6.1 StartZ=0 EndX=-9.5 EndY=6.1 EndZ=0
    g3: LineSegment StartX=-9.5 StartY=6.1 StartZ=0 EndX=-9.5 EndY=-6.1 EndZ=0
    g4: GeomPoint [constr] X=0 Y=0 Z=0
  constraints (12):
    c: Coincident(g0,g1)
    c: Coincident(g1,g2)
    c: Coincident(g2,g3)
    c: Coincident(g3,g0)
    c: Horizontal(g0)
    c: Horizontal(g2)
    c: Vertical(g1)
    c: Vertical(g3)
    c: Symmetric(g2,g0,g4)
    c: Distance(g1,g3) = 19
    c: Distance(g0,g2) = 12.2
    c: Coincident(g4,g-1)
FEATURE [PartDesign::Body] Body002  label="supporto per neopixel"
  AllowCompound = false
  Group = -> [Sketch045,Sketch046,Sketch047,Sketch048,Sketch049,Sketch064,Sketch066,Sketch068]
  Origin = -> Origin002
FEATURE [Part::Extrusion] Extrude073  label="Extrude base con smusso sopra neopixel"
  Base = -> Sketch068
  Dir = (1,0,0)
  DirMode = 2
  FaceMakerClass = Part::FaceMakerBullseye
  FaceMakerMode = 3
  LengthFwd = -1
  LengthRev = 0
  Solid = true
  Symmetric = false
FEATURE [Part::Chamfer] Chamfer  label="Chamfer frontale supporto neopixel da fondere al supporto"
  Base = -> Extrude073
  EdgeLinks = -> Extrude073 [Edge4,Edge7,Edge10,Edge12]
  Edges = 4 edges r=0.5: [Edge4,Edge7,Edge10,Edge12]
FEATURE [Sketcher::SketchObject] Sketch069  label="cilindro minore"
  ArcFitTolerance = 1e-06
  AttachmentSupport = -> [XZ_Plane004]
  FullyConstrained = true
  MakeInternals = false
  MapMode = 5
  Placement = pos=(0,0,0) rot=(1,0,0;1.5708rad)
  sketch-geometry (1):
    g0: Circle CenterX=0 CenterY=0 CenterZ=0 NormalX=0 NormalY=0 NormalZ=1 AngleXU=0 Radius=5.8
  constraints (2):
    c: Diameter(g0) = 11.6
    c: Coincident(g0,g-1)
FEATURE [Sketcher::SketchObject] Sketch070  label="cilindro maggiore"
  ArcFitTolerance = 1e-06
  AttachmentSupport = -> [XZ_Plane004]
  ExternalGeometry = -> [Sketch069]
  FullyConstrained = true
  MakeInternals = false
  MapMode = 5
  Placement = pos=(0,0,0) rot=(1,0,0;1.5708rad)
  sketch-geometry (1):
    g0: Circle CenterX=0 CenterY=0 CenterZ=0 NormalX=0 NormalY=0 NormalZ=1 AngleXU=0 Radius=6.5
  constraints (2):
    c: Coincident(g0,g-1)
    c: Diameter(g0) = 13
FEATURE [Sketcher::SketchObject] Sketch071  label="buco interno"
  ArcFitTolerance = 1e-06
  AttachmentSupport = -> [XZ_Plane004]
  ExternalGeometry = -> [Sketch069]
  FullyConstrained = true
  MakeInternals = false
  MapMode = 5
  Placement = pos=(0,0,0) rot=(1,0,0;1.5708rad)
  sketch-geometry (1):
    g0: Circle CenterX=0 CenterY=0 CenterZ=0 NormalX=0 NormalY=0 NormalZ=1 AngleXU=0 Radius=5
  constraints (2):
    c: Coincident(g0,g-1)
    c: Diameter(g0) = 10
FEATURE [PartDesign::Pad] Pad
  Direction = (0,-1,2e-16)
  Length = 1.2
  Length2 = 10
  Placement = pos=(0,0,0) rot=(1,0,0;1.5708rad)
  Profile = -> Sketch070
  ReferenceAxis = -> Sketch070 [N_Axis]
  Refine = true
  Suppressed = false
  Type = 0
FEATURE [PartDesign::Pad] Pad001
  BaseFeature = -> Pad
  Direction = (0,-1,2e-16)
  Length = 5.6
  Length2 = 10
  Placement = pos=(0,0,0) rot=(1,0,0;1.5708rad)
  Profile = -> Sketch069
  ReferenceAxis = -> Sketch069 [N_Axis]
  Refine = true
  Suppressed = false
  Type = 0
FEATURE [PartDesign::Pocket] Pocket
  BaseFeature = -> Pad001
  Direction = (0,1,-2e-16)
  Length = 7
  Length2 = 5
  Midplane = true
  Placement = pos=(0,0,0) rot=(1,0,0;1.5708rad)
  Profile = -> Sketch071
  ReferenceAxis = -> Sketch071 [N_Axis]
  Refine = true
  Suppressed = false
  Type = 0
FEATURE [PartDesign::Fillet] Fillet
  Base = -> Pocket [Face7]
  BaseFeature = -> Pocket
  Placement = pos=(0,0,0) rot=(1,0,0;1.5708rad)
  Radius = 1
  Refine = true
  SupportTransform = false
  Suppressed = false
  UseAllEdges = false
FEATURE [PartDesign::Body] Body004  label="pulsanti lato sinistro"
  AllowCompound = false
  Group = -> [Sketch069,Sketch070,Sketch071,Pad,Pad001,Pocket,Fillet]
  Origin = -> Origin004
  Tip = -> Fillet
FEATURE [Sketcher::SketchObject] Sketch072  label="buco per saldature e diodo driver solenoide"
  ArcFitTolerance = 1e-06
  AttachmentSupport = -> [XZ_Plane]
  ExternalGeometry = -> [Sketch038]
  FullyConstrained = true
  MakeInternals = false
  MapMode = 5
  Placement = pos=(0,0,0) rot=(1,0,0;1.5708rad)
  sketch-geometry (4):
    g0: LineSegment StartX=-209.225 StartY=-40.6939 StartZ=0 EndX=-204.154 EndY=-29.8182 EndZ=0
    g1: LineSegment StartX=-204.154 StartY=-29.8182 StartZ=0 EndX=-206.51 EndY=-28.7194 EndZ=0
    g2: LineSegment StartX=-206.51 StartY=-28.7194 StartZ=0 EndX=-211.582 EndY=-39.5951 EndZ=0
    g3: LineSegment StartX=-211.582 StartY=-39.5951 StartZ=0 EndX=-209.225 EndY=-40.6939 EndZ=0
  constraints (11):
    c: Coincident(g1,g0)
    c: Coincident(g2,g1)
    c: Coincident(g3,g2)
    c: Coincident(g3,g0)
    c: Parallel(g-3,g0)
    c: Parallel(g0,g2)
    c: Perpendicular(g0,g3)
    c: Perpendicular(g1,g0)
    c: Distance(g3) = 2.6
    c: Distance(g2) = 12
    c: Coincident(g0,g-3)
FEATURE [Part::Extrusion] Extrude074  label="Extrude buco per saldature e diodo driver solenoide"
  Base = -> Sketch072
  Dir = (0,-1,2e-16)
  DirMode = 2
  FaceMakerClass = Part::FaceMakerBullseye
  FaceMakerMode = 3
  LengthFwd = 14.6
  LengthRev = 0
  Solid = true
  Symmetric = true
FEATURE [Part::Cut] Cut042
  Base = -> Cut041
  Refine = true
  Tool = -> Extrude074
FEATURE [Sketcher::SketchObject] Sketch073  label="fori slargati blocco solenoide"
  ArcFitTolerance = 1e-06
  AttachmentSupport = -> [XY_Plane]
  ExternalGeometry = -> [Sketch030]
  FullyConstrained = true
  MakeInternals = false
  MapMode = 5
  sketch-geometry (2):
    g0: Circle CenterX=-152.209 CenterY=6.95 CenterZ=0 NormalX=0 NormalY=0 NormalZ=1 AngleXU=0 Radius=3.7
    g1: Circle CenterX=-130.41 CenterY=-6.95 CenterZ=0 NormalX=0 NormalY=0 NormalZ=1 AngleXU=0 Radius=3.7
  constraints (4):
    c: Diameter(g0) = 7.4
    c: Coincident(g0,g-3)
    c: Diameter(g1) = 7.4
    c: Coincident(g1,g-4)
FEATURE [Part::Extrusion] Extrude075  label="Extrude fori slargati blocco solenoide"
  Base = -> Sketch073
  Dir = (0,0,1)
  DirMode = 2
  FaceMakerClass = Part::FaceMakerBullseye
  FaceMakerMode = 3
  LengthFwd = 1.5
  LengthRev = 0
  Placement = pos=(0,0,36.4) rot=(0,0,1;0rad)
  Solid = true
  Symmetric = false
FEATURE [Part::Cut] Cut043
  Base = -> Cut042
  Refine = true
  Tool = -> Extrude075
FEATURE [Sketcher::SketchObject] Sketch074  label="lato sx pistola"
  ArcFitTolerance = 1e-06
  AttachmentSupport = -> [XZ_Plane]
  ExternalGeometry = -> [Sketch016,Sketch,Sketch058]
  FullyConstrained = true
  MakeInternals = false
  MapMode = 5
  Placement = pos=(0,0,0) rot=(1,0,0;1.5708rad)
  sketch-geometry (37):
    g0: LineSegment StartX=-82.8 StartY=3.2 StartZ=0 EndX=0 EndY=3.2 EndZ=0
    g1: LineSegment StartX=-82.8 StartY=3.2 StartZ=0 EndX=-82.8 EndY=6.2 EndZ=0
    g2: LineSegment [constr] StartX=-107.6 StartY=18 StartZ=0 EndX=-107.6 EndY=20 EndZ=0
    g3: LineSegment [constr] StartX=-132.428 StartY=18 StartZ=0 EndX=-132.428 EndY=20 EndZ=0
    g4: LineSegment StartX=-132.428 StartY=20 StartZ=0 EndX=-107.6 EndY=20 EndZ=0
    g5: ArcOfCircle CenterX=-107.6 CenterY=4 CenterZ=0 NormalX=0 NormalY=0 NormalZ=1 AngleXU=0 Radius=16 StartAngle=0.137937 EndAngle=1.5708
    g6: LineSegment StartX=-82.8 StartY=6.2 StartZ=0 EndX=-91.752 EndY=6.2 EndZ=0
    g7: LineSegment [constr] StartX=-145.743 StartY=8.32624 StartZ=0 EndX=-147.645 EndY=8.94427 EndZ=0
    g8: ArcOfCircle CenterX=-132.428 CenterY=4 CenterZ=0 NormalX=0 NormalY=0 NormalZ=1 AngleXU=0 Radius=16 StartAngle=1.5708 EndAngle=2.82743
    g9: LineSegment StartX=-215.932 StartY=-80.4316 StartZ=0 EndX=-176.685 EndY=-80.4316 EndZ=0
    g10: LineSegment StartX=-147.645 StartY=8.94427 StartZ=0 EndX=-176.685 EndY=-80.4316 EndZ=0
    g11: LineSegment [constr] StartX=-193.988 StartY=-2.33927 StartZ=0 EndX=-192.176 EndY=-3.18451 EndZ=0
    g12: LineSegment [constr] StartX=-217.232 StartY=-52.1862 StartZ=0 EndX=-215.42 EndY=-53.0314 EndZ=0
    g13: LineSegment StartX=-192.176 StartY=-3.18451 StartZ=0 EndX=-215.42 EndY=-53.0314 EndZ=0
    g14: ArcOfCircle CenterX=-184.801 CenterY=-67.3089 CenterZ=0 NormalX=0 NormalY=0 NormalZ=1 AngleXU=0 Radius=33.7833 StartAngle=2.70526 EndAngle=3.54053
    g15: ArcOfCircle CenterX=-207.583 CenterY=4 CenterZ=0 NormalX=0 NormalY=0 NormalZ=1 AngleXU=0 Radius=17 StartAngle=5.84685 EndAngle=7.56663
    g16: LineSegment StartX=-202.765 StartY=20.303 StartZ=0 EndX=-195.887 EndY=39.2 EndZ=0
    g17: LineSegment [constr] StartX=-193.885 StartY=33.0037 StartZ=0 EndX=-197.644 EndY=34.3718 EndZ=0
    g18: LineSegment StartX=-195.887 StartY=39.2 StartZ=0 EndX=0 EndY=39.2 EndZ=0
    g19: LineSegment StartX=0 StartY=3.2 StartZ=0 EndX=0 EndY=39.2 EndZ=0
    g20: LineSegment StartX=-189.939 StartY=31.5672 StartZ=0 EndX=-192.333 EndY=24.9893 EndZ=0
    g21: LineSegment StartX=-196.467 StartY=26.4942 StartZ=0 EndX=-194.073 EndY=33.0721 EndZ=0
    g22: Circle CenterX=-213.443 CenterY=-76.8316 CenterZ=0 NormalX=0 NormalY=0 NormalZ=1 AngleXU=0 Radius=1.8
    g23: Circle CenterX=-179.305 CenterY=-76.8316 CenterZ=0 NormalX=0 NormalY=0 NormalZ=1 AngleXU=0 Radius=1.8
    g24: Circle CenterX=-184.08 CenterY=34.8 CenterZ=0 NormalX=0 NormalY=0 NormalZ=1 AngleXU=0 Radius=1.8
    g25: Circle CenterX=-78.51 CenterY=34.8 CenterZ=0 NormalX=0 NormalY=0 NormalZ=1 AngleXU=0 Radius=1.8
    g26: Circle CenterX=-78.51 CenterY=7.6 CenterZ=0 NormalX=0 NormalY=0 NormalZ=1 AngleXU=0 Radius=1.8
    g27: Circle CenterX=-5.6 CenterY=34.8 CenterZ=0 NormalX=0 NormalY=0 NormalZ=1 AngleXU=0 Radius=1.8
    g28: Circle CenterX=-5.6 CenterY=7.6 CenterZ=0 NormalX=0 NormalY=0 NormalZ=1 AngleXU=0 Radius=1.8
    g29: LineSegment StartX=-190.127 StartY=31.6356 StartZ=0 EndX=-189.939 EndY=31.5672 EndZ=0
    g30: LineSegment StartX=-194.073 StartY=33.0721 StartZ=0 EndX=-193.885 EndY=33.0037 EndZ=0
    g31: LineSegment StartX=-193.885 StartY=33.0037 StartZ=0 EndX=-190.127 EndY=31.6356 EndZ=0
    g32: LineSegment StartX=-196.467 StartY=26.4942 StartZ=0 EndX=-192.333 EndY=24.9893 EndZ=0
    g33: Circle CenterX=-19 CenterY=21.2 CenterZ=0 NormalX=0 NormalY=0 NormalZ=1 AngleXU=0 Radius=6.3
    g34: Circle CenterX=-42 CenterY=21.2 CenterZ=0 NormalX=0 NormalY=0 NormalZ=1 AngleXU=0 Radius=6.3
    g35: Circle CenterX=-65 CenterY=21.2 CenterZ=0 NormalX=0 NormalY=0 NormalZ=1 AngleXU=0 Radius=6.3
    g36: LineSegment [constr] StartX=-4 StartY=21.2 StartZ=0 EndX=-65 EndY=21.2 EndZ=0
  constraints (96):
    c: Coincident(g0,g-41)
    c: Horizontal(g0)
    c: PointOnObject(g0,g-39)
    c: Coincident(g1,g0)
    c: Vertical(g1)
    c: DistanceY(g1,g1) = 3
    c: Coincident(g2,g-17)
    c: Vertical(g2)
    c: Coincident(g3,g-16)
    c: Vertical(g3)
    c: DistanceY(g2,g2) = 2
    c: DistanceY(g3,g3) = 2
    c: Coincident(g4,g3)
    c: Coincident(g4,g2)
    c: Coincident(g5,g-17)
    c: Coincident(g5,g2)
    c: Coincident(g6,g1)
    c: Horizontal(g6)
    c: Coincident(g6,g5)
    c: Coincident(g7,g-15)
    c: Coincident(g8,g7)
    c: Coincident(g8,g3)
    c: Coincident(g8,g-15)
    c: Horizontal(g9)
    c: DistanceY(g-13,g9) = 2
    c: Coincident(g10,g7)
    c: Parallel(g10,g-14)
    c: Coincident(g9,g10)
    c: Distance(g11) = 2
    c: Coincident(g11,g-11)
    c: Perpendicular(g-11,g11)
    c: Distance(g12) = 2
    c: Coincident(g12,g-12)
    c: Perpendicular(g-11,g12)
    c: Coincident(g13,g11)
    c: Coincident(g13,g12)
    c: Coincident(g14,g-32)
    c: Coincident(g14,g12)
    c: Coincident(g14,g9)
    c: Coincident(g15,g-10)
    c: Coincident(g15,g11)
    c: Parallel(g16,g-22)
    c: Distance(g17) = 4
    c: PointOnObject(g17,g16)
    c: Coincident(g15,g16)
    c: Horizontal(g18)
    c: Coincident(g18,g16)
    c: Coincident(g19,g0)
    c: PointOnObject(g19,g-39)
    c: DistanceY(g19,g-36) = 2
    c: Coincident(g18,g19)
    c: Diameter(g22) = 3.6
    c: Coincident(g22,g-9)
    c: Diameter(g23) = 3.6
    c: Coincident(g23,g-8)
    c: Diameter(g24) = 3.6
    c: Diameter(g25) = 3.6
    c: Diameter(g26) = 3.6
    c: Diameter(g27) = 3.6
    c: Diameter(g28) = 3.6
    c: Coincident(g27,g-4)
    c: Coincident(g28,g-3)
    c: Coincident(g25,g-6)
    c: Coincident(g26,g-5)
    c: Coincident(g24,g-7)
    c: Parallel(g20,g-21)
    c: Equal(g20,g-21)
    c: Parallel(g21,g-19)
    c: Equal(g21,g-19)
    c: Distance(g29) = 0.2
    c: Distance(g30) = 0.2
    c: Parallel(g29,g-20)
    c: Parallel(g31,g-20)
    c: Equal(g31,g-20)
    c: Coincident(g30,g31)
    c: Coincident(g31,g29)
    c: Coincident(g29,g-21)
    c: Parallel(g30,g31)
    c: Coincident(g17,g30)
    c: Coincident(g20,g29)
    c: Coincident(g21,g30)
    c: Perpendicular(g16,g17)
    c: Coincident(g32,g21)
    c: Coincident(g32,g20)
    c: Perpendicular(g10,g7)
    c: Diameter(g33) = 12.6
    c: Diameter(g34) = 12.6
    c: Diameter(g35) = 12.6
    c: Horizontal(g36)
    c: PointOnObject(g33,g36)
    c: PointOnObject(g34,g36)
    c: DistanceX(g34,g33) = 23
    c: DistanceX(g35,g34) = 23
    c: DistanceX(g33,g36) = 15
    c: Symmetric(g-24,g-24,g36)
    c: Coincident(g36,g35)
FEATURE [Part::Extrusion] Extrude076  label="Extrude lato sx pistola"
  Base = -> Sketch074
  Dir = (0,-1,2e-16)
  DirMode = 2
  FaceMakerClass = Part::FaceMakerBullseye
  FaceMakerMode = 3
  LengthFwd = -2
  LengthRev = 0
  Solid = true
  Symmetric = false
FEATURE [Sketcher::SketchObject] Sketch075  label="lato dx pistola"
  ArcFitTolerance = 1e-06
  AttachmentSupport = -> [XZ_Plane]
  ExternalGeometry = -> [Sketch016,Sketch,Sketch058,Sketch074]
  FullyConstrained = true
  MakeInternals = false
  MapMode = 5
  Placement = pos=(0,0,0) rot=(1,0,0;1.5708rad)
  sketch-geometry (61):
    g0: LineSegment StartX=-82.8 StartY=3.2 StartZ=0 EndX=0 EndY=3.2 EndZ=0
    g1: LineSegment StartX=-82.8 StartY=3.2 StartZ=0 EndX=-82.8 EndY=6.2 EndZ=0
    g2: LineSegment [constr] StartX=-107.6 StartY=18 StartZ=0 EndX=-107.6 EndY=20 EndZ=0
    g3: LineSegment [constr] StartX=-132.428 StartY=18 StartZ=0 EndX=-132.428 EndY=20 EndZ=0
    g4: LineSegment StartX=-132.428 StartY=20 StartZ=0 EndX=-107.6 EndY=20 EndZ=0
    g5: ArcOfCircle CenterX=-107.6 CenterY=4 CenterZ=0 NormalX=0 NormalY=0 NormalZ=1 AngleXU=0 Radius=16 StartAngle=0.137937 EndAngle=1.5708
    g6: LineSegment StartX=-82.8 StartY=6.2 StartZ=0 EndX=-91.752 EndY=6.2 EndZ=0
    g7: LineSegment [constr] StartX=-145.743 StartY=8.32624 StartZ=0 EndX=-147.645 EndY=8.94427 EndZ=0
    g8: ArcOfCircle CenterX=-132.428 CenterY=4 CenterZ=0 NormalX=0 NormalY=0 NormalZ=1 AngleXU=0 Radius=16 StartAngle=1.5708 EndAngle=2.82743
    g9: LineSegment StartX=-215.932 StartY=-80.4316 StartZ=0 EndX=-176.685 EndY=-80.4316 EndZ=0
    g10: LineSegment StartX=-147.645 StartY=8.94427 StartZ=0 EndX=-176.685 EndY=-80.4316 EndZ=0
    g11: LineSegment [constr] StartX=-193.988 StartY=-2.33927 StartZ=0 EndX=-192.176 EndY=-3.18451 EndZ=0
    g12: LineSegment [constr] StartX=-217.232 StartY=-52.1862 StartZ=0 EndX=-215.42 EndY=-53.0314 EndZ=0
    g13: LineSegment StartX=-192.176 StartY=-3.18451 StartZ=0 EndX=-215.42 EndY=-53.0314 EndZ=0
    g14: ArcOfCircle CenterX=-184.801 CenterY=-67.3089 CenterZ=0 NormalX=0 NormalY=0 NormalZ=1 AngleXU=0 Radius=33.7833 StartAngle=2.70526 EndAngle=3.54053
    g15: ArcOfCircle CenterX=-207.583 CenterY=4 CenterZ=0 NormalX=0 NormalY=0 NormalZ=1 AngleXU=0 Radius=17 StartAngle=5.84685 EndAngle=7.56663
    g16: LineSegment StartX=-202.765 StartY=20.303 StartZ=0 EndX=-195.887 EndY=39.2 EndZ=0
    g17: LineSegment [constr] StartX=-193.885 StartY=33.0037 StartZ=0 EndX=-197.644 EndY=34.3718 EndZ=0
    g18: LineSegment StartX=-195.887 StartY=39.2 StartZ=0 EndX=0 EndY=39.2 EndZ=0
    g19: LineSegment StartX=0 StartY=3.2 StartZ=0 EndX=0 EndY=39.2 EndZ=0
    g20: LineSegment StartX=-189.939 StartY=31.5672 StartZ=0 EndX=-192.333 EndY=24.9893 EndZ=0
    g21: LineSegment StartX=-196.467 StartY=26.4942 StartZ=0 EndX=-194.073 EndY=33.0721 EndZ=0
    g22: Circle CenterX=-213.443 CenterY=-76.8316 CenterZ=0 NormalX=0 NormalY=0 NormalZ=1 AngleXU=0 Radius=1.8
    g23: Circle CenterX=-179.305 CenterY=-76.8316 CenterZ=0 NormalX=0 NormalY=0 NormalZ=1 AngleXU=0 Radius=1.8
    g24: Circle CenterX=-184.08 CenterY=34.8 CenterZ=0 NormalX=0 NormalY=0 NormalZ=1 AngleXU=0 Radius=1.8
    g25: Circle CenterX=-78.51 CenterY=34.8 CenterZ=0 NormalX=0 NormalY=0 NormalZ=1 AngleXU=0 Radius=1.8
    g26: Circle CenterX=-78.51 CenterY=7.6 CenterZ=0 NormalX=0 NormalY=0 NormalZ=1 AngleXU=0 Radius=1.8
    g27: Circle CenterX=-5.6 CenterY=34.8 CenterZ=0 NormalX=0 NormalY=0 NormalZ=1 AngleXU=0 Radius=1.8
    g28: Circle CenterX=-5.6 CenterY=7.6 CenterZ=0 NormalX=0 NormalY=0 NormalZ=1 AngleXU=0 Radius=1.8
    g29: LineSegment StartX=-190.127 StartY=31.6356 StartZ=0 EndX=-189.939 EndY=31.5672 EndZ=0
    g30: LineSegment StartX=-194.073 StartY=33.0721 StartZ=0 EndX=-193.885 EndY=33.0037 EndZ=0
    g31: LineSegment StartX=-193.885 StartY=33.0037 StartZ=0 EndX=-190.127 EndY=31.6356 EndZ=0
    g32: LineSegment StartX=-196.467 StartY=26.4942 StartZ=0 EndX=-192.333 EndY=24.9893 EndZ=0
    g33: LineSegment [constr] StartX=-4 StartY=21.2 StartZ=0 EndX=-87.91 EndY=21.2 EndZ=0
    g34: GeomPoint [constr] X=-4 Y=21.2 Z=0
    g35: LineSegment [constr] StartX=-15.2 StartY=33.7 StartZ=0 EndX=-15.2 EndY=8.7 EndZ=0
    g36: LineSegment [constr] StartX=-15.2 StartY=33.7 StartZ=0 EndX=-56.2 EndY=33.7 EndZ=0
    g37: LineSegment [constr] StartX=-15.2 StartY=8.7 StartZ=0 EndX=-56.2 EndY=8.7 EndZ=0
    g38: LineSegment [constr] StartX=-56.2 StartY=33.7 StartZ=0 EndX=-56.2 EndY=8.7 EndZ=0
    g39: Circle CenterX=-18.6 CenterY=30.3 CenterZ=0 NormalX=0 NormalY=0 NormalZ=1 AngleXU=0 Radius=3.4
    g40: Circle CenterX=-18.6 CenterY=12.1 CenterZ=0 NormalX=0 NormalY=0 NormalZ=1 AngleXU=0 Radius=3.4
    g41: Circle CenterX=-43.2 CenterY=30.3 CenterZ=0 NormalX=0 NormalY=0 NormalZ=1 AngleXU=0 Radius=3.4
    g42: Circle CenterX=-43.2 CenterY=12.1 CenterZ=0 NormalX=0 NormalY=0 NormalZ=1 AngleXU=0 Radius=3.4
    g43: LineSegment [constr] StartX=-4 StartY=21.2 StartZ=0 EndX=-15.2 EndY=21.2 EndZ=0
    g44: LineSegment [constr] StartX=-15.2 StartY=21.2 StartZ=0 EndX=-36.2 EndY=21.2 EndZ=0
    g45: LineSegment [constr] StartX=-41.5 StartY=16.2 StartZ=0 EndX=-30.9 EndY=16.2 EndZ=0
    g46: LineSegment [constr] StartX=-30.9 StartY=16.2 StartZ=0 EndX=-30.9 EndY=26.2 EndZ=0
    g47: LineSegment [constr] StartX=-30.9 StartY=26.2 StartZ=0 EndX=-41.5 EndY=26.2 EndZ=0
    g48: LineSegment [constr] StartX=-41.5 StartY=26.2 StartZ=0 EndX=-41.5 EndY=16.2 EndZ=0
    g49: GeomPoint [constr] X=-36.2 Y=21.2 Z=0
    g50: Circle CenterX=-36.2 CenterY=21.2 CenterZ=0 NormalX=0 NormalY=0 NormalZ=1 AngleXU=0 Radius=2.8
    g51: LineSegment [constr] StartX=-24.2 StartY=26.7 StartZ=0 EndX=-24.2 EndY=15.7 EndZ=0
    g52: Circle CenterX=-24.2 CenterY=26.7 CenterZ=0 NormalX=0 NormalY=0 NormalZ=1 AngleXU=0 Radius=3
    g53: Circle CenterX=-24.2 CenterY=15.7 CenterZ=0 NormalX=0 NormalY=0 NormalZ=1 AngleXU=0 Radius=3
    g54: GeomPoint X=-18.6 Y=30.3 Z=0
    g55: GeomPoint X=-18.6 Y=12.1 Z=0
    g56: GeomPoint X=-43.2 Y=12.1 Z=0
    g57: GeomPoint X=-43.2 Y=30.3 Z=0
    g58: Circle CenterX=-65 CenterY=21.2 CenterZ=0 NormalX=0 NormalY=0 NormalZ=1 AngleXU=0 Radius=1.5
    g59: Circle CenterX=-42 CenterY=21.2 CenterZ=0 NormalX=0 NormalY=0 NormalZ=1 AngleXU=0 Radius=1.5
    g60: Circle CenterX=-19 CenterY=21.2 CenterZ=0 NormalX=0 NormalY=0 NormalZ=1 AngleXU=0 Radius=1.5
  constraints (149):
    c: Coincident(g0,g-41)
    c: Horizontal(g0)
    c: PointOnObject(g0,g-39)
    c: Coincident(g1,g0)
    c: Vertical(g1)
    c: DistanceY(g1,g1) = 3
    c: Coincident(g2,g-17)
    c: Vertical(g2)
    c: Coincident(g3,g-16)
    c: Vertical(g3)
    c: DistanceY(g2,g2) = 2
    c: DistanceY(g3,g3) = 2
    c: Coincident(g4,g3)
    c: Coincident(g4,g2)
    c: Coincident(g5,g-17)
    c: Coincident(g5,g2)
    c: Coincident(g6,g1)
    c: Horizontal(g6)
    c: Coincident(g6,g5)
    c: Coincident(g7,g-15)
    c: Coincident(g8,g7)
    c: Coincident(g8,g3)
    c: Coincident(g8,g-15)
    c: Horizontal(g9)
    c: DistanceY(g-13,g9) = 2
    c: Coincident(g10,g7)
    c: Parallel(g10,g-14)
    c: Coincident(g9,g10)
    c: Distance(g11) = 2
    c: Coincident(g11,g-11)
    c: Perpendicular(g-11,g11)
    c: Distance(g12) = 2
    c: Coincident(g12,g-12)
    c: Perpendicular(g-11,g12)
    c: Coincident(g13,g11)
    c: Coincident(g13,g12)
    c: Coincident(g14,g-32)
    c: Coincident(g14,g12)
    c: Coincident(g14,g9)
    c: Coincident(g15,g-10)
    c: Coincident(g15,g11)
    c: Parallel(g16,g-22)
    c: Distance(g17) = 4
    c: PointOnObject(g17,g16)
    c: Coincident(g15,g16)
    c: Horizontal(g18)
    c: Coincident(g18,g16)
    c: Coincident(g19,g0)
    c: PointOnObject(g19,g-39)
    c: DistanceY(g19,g-36) = 2
    c: Coincident(g18,g19)
    c: Diameter(g22) = 3.6
    c: Coincident(g22,g-9)
    c: Diameter(g23) = 3.6
    c: Coincident(g23,g-8)
    c: Diameter(g24) = 3.6
    c: Diameter(g25) = 3.6
    c: Diameter(g26) = 3.6
    c: Diameter(g27) = 3.6
    c: Diameter(g28) = 3.6
    c: Coincident(g27,g-4)
    c: Coincident(g28,g-3)
    c: Coincident(g25,g-6)
    c: Coincident(g26,g-5)
    c: Coincident(g24,g-7)
    c: Parallel(g20,g-21)
    c: Equal(g20,g-21)
    c: Parallel(g21,g-19)
    c: Equal(g21,g-19)
    c: Distance(g29) = 0.2
    c: Distance(g30) = 0.2
    c: Parallel(g29,g-20)
    c: Parallel(g31,g-20)
    c: Equal(g31,g-20)
    c: Coincident(g30,g31)
    c: Coincident(g31,g29)
    c: Coincident(g29,g-21)
    c: Parallel(g30,g31)
    c: Coincident(g17,g30)
    c: Coincident(g20,g29)
    c: Coincident(g21,g30)
    c: Perpendicular(g16,g17)
    c: Coincident(g32,g21)
    c: Coincident(g32,g20)
    c: Perpendicular(g10,g7)
    c: Horizontal(g33)
    c: Symmetric(g-24,g-24,g33)
    c: PointOnObject(g33,g-28)
    c: Symmetric(g-24,g-24,g34)
    c: DistanceY(g35,g35) = 25
    c: Symmetric(g35,g35,g33)
    c: Distance(g36) = 41
    c: Coincident(g36,g35)
    c: Horizontal(g36)
    c: Coincident(g37,g35)
    c: Horizontal(g37)
    c: Coincident(g38,g36)
    c: Vertical(g38)
    c: Coincident(g37,g38)
    c: Diameter(g39) = 6.8
    c: Diameter(g40) = 6.8
    c: Tangent(g39,g36)
    c: Tangent(g40,g37)
    c: Tangent(g39,g35)
    c: Tangent(g40,g35)
    c: Diameter(g41) = 6.8
    c: Diameter(g42) = 6.8
    c: Tangent(g41,g36)
    c: Tangent(g42,g37)
    c: DistanceX(g41,g39) = 24.6
    c: DistanceX(g42,g40) = 24.6
    c: Distance(g43) = 11.2
    c: Coincident(g43,g33)
    c: PointOnObject(g43,g33)
    c: PointOnObject(g43,g35)
    c: Distance(g44) = 21
    c: Coincident(g44,g43)
    c: PointOnObject(g44,g33)
    c: Coincident(g45,g46)
    c: Coincident(g46,g47)
    c: Coincident(g47,g48)
    c: Coincident(g48,g45)
    c: Horizontal(g45)
    c: Horizontal(g47)
    c: Vertical(g46)
    c: Vertical(g48)
    c: Symmetric(g47,g45,g49)
    c: Distance(g46,g48) = 10.6
    c: Distance(g45,g47) = 10
    c: Coincident(g49,g44)
    c: Diameter(g50) = 5.6
    c: Coincident(g50,g44)
    c: Distance(g51) = 11
    c: Symmetric(g51,g51,g33)
    c: DistanceX(g51,g43) = 9
    c: Diameter(g52) = 6
    c: Coincident(g52,g51)
    c: Diameter(g53) = 6
    c: Coincident(g53,g51)
    c: Coincident(g40,g55)
    c: Coincident(g39,g54)
    c: Coincident(g41,g57)
    c: Coincident(g42,g56)
    c: Diameter(g58) = 3
    c: Diameter(g59) = 3
    c: Diameter(g60) = 3
    c: Coincident(g58,g-44)
    c: Coincident(g59,g-46)
    c: Coincident(g60,g-45)
FEATURE [Sketcher::SketchObject] Sketch076  label="lato sx pistola - scavi pulsanti"
  ArcFitTolerance = 1e-06
  AttachmentSupport = -> [XZ_Plane]
  ExternalGeometry = -> [Sketch074]
  FullyConstrained = true
  MakeInternals = false
  MapMode = 5
  Placement = pos=(0,0,0) rot=(1,0,0;1.5708rad)
  sketch-geometry (3):
    g0: Circle CenterX=-65 CenterY=21.2 CenterZ=0 NormalX=0 NormalY=0 NormalZ=1 AngleXU=0 Radius=7.3
    g1: Circle CenterX=-42 CenterY=21.2 CenterZ=0 NormalX=0 NormalY=0 NormalZ=1 AngleXU=0 Radius=7.3
    g2: Circle CenterX=-19 CenterY=21.2 CenterZ=0 NormalX=0 NormalY=0 NormalZ=1 AngleXU=0 Radius=7.3
  constraints (6):
    c: Diameter(g0) = 14.6
    c: Diameter(g1) = 14.6
    c: Diameter(g2) = 14.6
    c: Coincident(g0,g-3)
    c: Coincident(g1,g-4)
    c: Coincident(g2,g-5)
FEATURE [Part::Extrusion] Extrude077  label="Extrude lato sx pistola - scavi pulsanti"
  Base = -> Sketch076
  Dir = (0,-1,2e-16)
  DirMode = 2
  FaceMakerClass = Part::FaceMakerBullseye
  FaceMakerMode = 3
  LengthFwd = -1.2
  LengthRev = 0
  Solid = true
  Symmetric = false
FEATURE [Part::Cut] Cut044
  Base = -> Extrude076
  Refine = true
  Tool = -> Extrude077
FEATURE [Part::Extrusion] Extrude078  label="Extrude lato dx pistola"
  Base = -> Sketch075
  Dir = (0,-1,2e-16)
  DirMode = 2
  FaceMakerClass = Part::FaceMakerBullseye
  FaceMakerMode = 3
  LengthFwd = 2
  LengthRev = 0
  Solid = true
  Symmetric = false
FEATURE [Sketcher::SketchObject] Sketch077  label="lato dx pistola - scavi pulsanti"
  ArcFitTolerance = 1e-06
  AttachmentSupport = -> [XZ_Plane]
  ExternalGeometry = -> [Sketch075]
  FullyConstrained = true
  MakeInternals = false
  MapMode = 5
  Placement = pos=(0,0,0) rot=(1,0,0;1.5708rad)
  sketch-geometry (4):
    g0: LineSegment StartX=-27.2 StartY=26.7 StartZ=0 EndX=-27.2 EndY=15.7 EndZ=0
    g1: LineSegment StartX=-21.2 StartY=26.7 StartZ=0 EndX=-21.2 EndY=15.7 EndZ=0
    g2: ArcOfCircle CenterX=-24.2 CenterY=26.7 CenterZ=0 NormalX=0 NormalY=0 NormalZ=1 AngleXU=0 Radius=3 StartAngle=5.96642e-06 EndAngle=3.14159
    g3: ArcOfCircle CenterX=-24.2 CenterY=15.7 CenterZ=0 NormalX=0 NormalY=0 NormalZ=1 AngleXU=0 Radius=3 StartAngle=3.14159 EndAngle=6.28319
  constraints (10):
    c: Vertical(g0)
    c: Coincident(g2,g-3)
    c: Vertical(g1)
    c: Coincident(g3,g-4)
    c: Tangent(g1,g-3)
    c: Tangent(g0,g-3)
    c: Tangent(g3,g0) = -1.5708
    c: Coincident(g3,g1)
    c: Tangent(g0,g2) = -1.5708
    c: Coincident(g1,g2)
FEATURE [Part::Extrusion] Extrude079  label="Extrude lato dx pistola - scavi pulsanti"
  Base = -> Sketch077
  Dir = (0,-1,2e-16)
  DirMode = 2
  FaceMakerClass = Part::FaceMakerBullseye
  FaceMakerMode = 3
  LengthFwd = 1.2
  LengthRev = 0
  Solid = true
  Symmetric = false
FEATURE [Part::Cut] Cut045
  Base = -> Extrude078
  Refine = true
  Tool = -> Extrude079
FEATURE [Sketcher::SketchObject] Sketch078
  ArcFitTolerance = 1e-06
  AttachmentSupport = -> [XZ_Plane005]
  FullyConstrained = true
  MakeInternals = false
  MapMode = 5
  Placement = pos=(0,0,0) rot=(1,0,0;1.5708rad)
  sketch-geometry (5):
    g0: LineSegment [constr] StartX=0 StartY=5.5 StartZ=0 EndX=0 EndY=-5.5 EndZ=0
    g1: ArcOfCircle CenterX=0 CenterY=5.5 CenterZ=0 NormalX=0 NormalY=0 NormalZ=1 AngleXU=0 Radius=2.7 StartAngle=0 EndAngle=3.14159
    g2: ArcOfCircle CenterX=0 CenterY=-5.5 CenterZ=0 NormalX=0 NormalY=0 NormalZ=1 AngleXU=0 Radius=2.7 StartAngle=3.1416 EndAngle=6.28318
    g3: LineSegment StartX=-2.7 StartY=5.5 StartZ=0 EndX=-2.7 EndY=-5.50001 EndZ=0
    g4: LineSegment StartX=2.7 StartY=5.5 StartZ=0 EndX=2.7 EndY=-5.50001 EndZ=0
  constraints (13):
    c: Distance(g0) = 11
    c: Vertical(g0)
    c: Symmetric(g0,g0,g-1)
    c: Radius(g1) = 2.7
    c: Coincident(g1,g0)
    c: Radius(g2) = 2.7
    c: Coincident(g2,g0)
    c: Vertical(g3)
    c: Vertical(g4)
    c: Coincident(g2,g4)
    c: Coincident(g2,g3)
    c: Tangent(g3,g1) = -1.5708
    c: Tangent(g4,g1) = 1.5708
FEATURE [PartDesign::Pad] Pad002
  Direction = (0,-1,2e-16)
  Length = 0.8
  Length2 = 10
  Placement = pos=(0,0,0) rot=(1,0,0;1.5708rad)
  Profile = -> Sketch078
  ReferenceAxis = -> Sketch078 [N_Axis]
  Refine = true
  Suppressed = false
  Type = 0
FEATURE [Sketcher::SketchObject] Sketch079
  ArcFitTolerance = 1e-06
  AttachmentSupport = -> [XZ_Plane005]
  ExternalGeometry = -> [Sketch078]
  FullyConstrained = true
  MakeInternals = false
  MapMode = 5
  Placement = pos=(0,0,0) rot=(1,0,0;1.5708rad)
  sketch-geometry (2):
    g0: Circle CenterX=-1e-16 CenterY=5.5 CenterZ=0 NormalX=0 NormalY=0 NormalZ=1 AngleXU=0 Radius=2.7
    g1: Circle CenterX=0 CenterY=-5.5 CenterZ=0 NormalX=0 NormalY=0 NormalZ=1 AngleXU=0 Radius=2.7
  constraints (4):
    c: Coincident(g0,g-3)
    c: PointOnObject(g-3,g0)
    c: Coincident(g1,g-4)
    c: Equal(g1,g-4)
FEATURE [PartDesign::Pad] Pad003
  BaseFeature = -> Pad002
  Direction = (0,-1,2e-16)
  Length = 5
  Length2 = 10
  Placement = pos=(0,0,0) rot=(1,0,0;1.5708rad)
  Profile = -> Sketch079
  ReferenceAxis = -> Sketch079 [N_Axis]
  Refine = true
  Suppressed = false
  Type = 0
FEATURE [PartDesign::Fillet] Fillet001
  Base = -> Pad003 [Edge16,Edge14]
  BaseFeature = -> Pad003
  Placement = pos=(0,0,0) rot=(1,0,0;1.5708rad)
  Radius = 0.4
  Refine = true
  SupportTransform = false
  Suppressed = false
  UseAllEdges = false
FEATURE [PartDesign::Body] Body005  label="pulsanti lato destro"
  AllowCompound = false
  Group = -> [Sketch078,Pad002,Sketch079,Pad003,Fillet001]
  Origin = -> Origin005
  Tip = -> Fillet001
FEATURE [Sketcher::SketchObject] Sketch080  label="lato dx pistola - fori per inserto M3 x 3 x 4.5"
  ArcFitTolerance = 1e-06
  AttachmentSupport = -> [XZ_Plane]
  ExternalGeometry = -> [Sketch075]
  FullyConstrained = true
  MakeInternals = false
  MapMode = 5
  Placement = pos=(0,0,0) rot=(1,0,0;1.5708rad)
  sketch-geometry (4):
    g0: Circle CenterX=-18.6 CenterY=12.1 CenterZ=0 NormalX=0 NormalY=0 NormalZ=1 AngleXU=0 Radius=2.25
    g1: Circle CenterX=-18.6 CenterY=30.3 CenterZ=0 NormalX=0 NormalY=0 NormalZ=1 AngleXU=0 Radius=2.25
    g2: Circle CenterX=-43.2 CenterY=30.3 CenterZ=0 NormalX=0 NormalY=0 NormalZ=1 AngleXU=0 Radius=2.25
    g3: Circle CenterX=-43.2 CenterY=12.1 CenterZ=0 NormalX=0 NormalY=0 NormalZ=1 AngleXU=0 Radius=2.25
  constraints (8):
    c: Diameter(g0) = 4.5
    c: Coincident(g0,g-5)
    c: Diameter(g1) = 4.5
    c: Coincident(g1,g-4)
    c: Diameter(g2) = 4.5
    c: Coincident(g2,g-3)
    c: Diameter(g3) = 4.5
    c: Coincident(g3,g-6)
FEATURE [Sketcher::SketchObject] Sketch081  label="lato dx pistola - pieno per inserto M3 x 3 x 4,5"
  ArcFitTolerance = 1e-06
  AttachmentSupport = -> [XZ_Plane]
  ExternalGeometry = -> [Sketch075]
  FullyConstrained = true
  MakeInternals = false
  MapMode = 5
  Placement = pos=(0,0,0) rot=(1,0,0;1.5708rad)
  sketch-geometry (4):
    g0: Circle CenterX=-43.2 CenterY=30.3 CenterZ=0 NormalX=0 NormalY=0 NormalZ=1 AngleXU=0 Radius=3.4
    g1: Circle CenterX=-18.6 CenterY=30.3 CenterZ=0 NormalX=0 NormalY=0 NormalZ=1 AngleXU=0 Radius=3.4
    g2: Circle CenterX=-43.2 CenterY=12.1 CenterZ=0 NormalX=0 NormalY=0 NormalZ=1 AngleXU=0 Radius=3.4
    g3: Circle CenterX=-18.6 CenterY=12.1 CenterZ=0 NormalX=0 NormalY=0 NormalZ=1 AngleXU=0 Radius=3.4
  constraints (8):
    c: Diameter(g0) = 6.8
    c: Coincident(g0,g-6)
    c: Diameter(g1) = 6.8
    c: Coincident(g1,g-3)
    c: Diameter(g2) = 6.8
    c: Coincident(g2,g-5)
    c: Diameter(g3) = 6.8
    c: Coincident(g3,g-4)
FEATURE [Part::Extrusion] Extrude080  label="Extrude lato dx pistola - pieno per inserto M3 x 3 x 4,5"
  Base = -> Sketch081
  Dir = (0,-1,2e-16)
  DirMode = 2
  FaceMakerClass = Part::FaceMakerBullseye
  FaceMakerMode = 3
  LengthFwd = -2.4
  LengthRev = 0
  Solid = true
  Symmetric = false
FEATURE [Part::MultiFuse] Fusion004
  Refine = true
  Shapes = -> [Cut045,Extrude080]
FEATURE [Part::Extrusion] Extrude081  label="Extrude lato dx pistola - fori per inserto M3 x 3 x 4.5"
  Base = -> Sketch080
  Dir = (0,-1,2e-16)
  DirMode = 2
  FaceMakerClass = Part::FaceMakerBullseye
  FaceMakerMode = 3
  LengthFwd = 0.6
  LengthRev = 2.4
  Solid = true
  Symmetric = false
FEATURE [Part::Cut] Cut046
  Base = -> Fusion004
  Refine = true
  Tool = -> Extrude081
FEATURE [Sketcher::SketchObject] Sketch082  label="lato sx pistola - disegno anteriore"
  ArcFitTolerance = 1e-06
  AttachmentSupport = -> [XZ_Plane]
  ExternalGeometry = -> [Sketch074]
  FullyConstrained = true
  MakeInternals = false
  MapMode = 5
  Placement = pos=(0,0,0) rot=(1,0,0;1.5708rad)
  sketch-geometry (12):
    g0: ArcOfCircle CenterX=-65 CenterY=21.2 CenterZ=0 NormalX=0 NormalY=0 NormalZ=1 AngleXU=0 Radius=10 StartAngle=1.5708 EndAngle=4.71239
    g1: ArcOfCircle CenterX=-19 CenterY=21.2 CenterZ=0 NormalX=0 NormalY=0 NormalZ=1 AngleXU=0 Radius=10 StartAngle=4.71239 EndAngle=7.85398
    g2: LineSegment StartX=-65 StartY=31.2 StartZ=0 EndX=-19 EndY=31.2 EndZ=0
    g3: LineSegment StartX=-65 StartY=11.2 StartZ=0 EndX=-19 EndY=11.2 EndZ=0
    g4: LineSegment StartX=-82.8 StartY=3.2 StartZ=0 EndX=0 EndY=3.2 EndZ=0
    g5: LineSegment StartX=0 StartY=3.2 StartZ=0 EndX=0 EndY=39.2 EndZ=0
    g6: LineSegment StartX=0 StartY=39.2 StartZ=0 EndX=-82.8 EndY=39.2 EndZ=0
    g7: LineSegment StartX=-82.8 StartY=39.2 StartZ=0 EndX=-82.8 EndY=3.2 EndZ=0
    g8: Circle CenterX=-78.51 CenterY=34.8 CenterZ=0 NormalX=0 NormalY=0 NormalZ=1 AngleXU=0 Radius=1.8
    g9: Circle CenterX=-5.6 CenterY=34.8 CenterZ=0 NormalX=0 NormalY=0 NormalZ=1 AngleXU=0 Radius=1.8
    g10: Circle CenterX=-5.6 CenterY=7.6 CenterZ=0 NormalX=0 NormalY=0 NormalZ=1 AngleXU=0 Radius=1.8
    g11: Circle CenterX=-78.51 CenterY=7.6 CenterZ=0 NormalX=0 NormalY=0 NormalZ=1 AngleXU=0 Radius=1.8
  constraints (26):
    c: Tangent(g0,g2) = 1.5708
    c: Tangent(g0,g3) = -1.5708
    c: Tangent(g1,g2) = 1.5708
    c: Tangent(g1,g3) = -1.5708
    c: Equal(g0,g1)
    c: Coincident(g4,g5)
    c: Coincident(g5,g6)
    c: Coincident(g6,g7)
    c: Coincident(g7,g4)
    c: Horizontal(g4)
    c: Horizontal(g6)
    c: Vertical(g5)
    c: Vertical(g7)
    c: Coincident(g4,g-7)
    c: Coincident(g5,g-9)
    c: Diameter(g1) = 20
    c: Coincident(g1,g-5)
    c: Coincident(g0,g-4)
    c: Equal(g9,g-11)
    c: Equal(g10,g-12)
    c: Equal(g11,g-13)
    c: Equal(g8,g-10)
    c: Coincident(g8,g-10)
    c: Coincident(g11,g-13)
    c: Coincident(g10,g-12)
    c: Coincident(g9,g-11)
FEATURE [Sketcher::SketchObject] Sketch083  label="lato dx pistola - disegno anteriore"
  ArcFitTolerance = 1e-06
  AttachmentSupport = -> [XZ_Plane]
  ExternalGeometry = -> [Sketch082]
  FullyConstrained = true
  MakeInternals = false
  MapMode = 5
  Placement = pos=(0,0,0) rot=(1,0,0;1.5708rad)
  sketch-geometry (12):
    g0: LineSegment StartX=-82.8 StartY=3.2 StartZ=0 EndX=0 EndY=3.2 EndZ=0
    g1: LineSegment StartX=0 StartY=3.2 StartZ=0 EndX=0 EndY=39.2 EndZ=0
    g2: LineSegment StartX=0 StartY=39.2 StartZ=0 EndX=-82.8 EndY=39.2 EndZ=0
    g3: LineSegment StartX=-82.8 StartY=39.2 StartZ=0 EndX=-82.8 EndY=3.2 EndZ=0
    g4: ArcOfCircle CenterX=-65 CenterY=21.2 CenterZ=0 NormalX=0 NormalY=0 NormalZ=1 AngleXU=0 Radius=10 StartAngle=1.5708 EndAngle=4.71239
    g5: ArcOfCircle CenterX=-19 CenterY=21.2 CenterZ=0 NormalX=0 NormalY=0 NormalZ=1 AngleXU=0 Radius=10 StartAngle=4.71239 EndAngle=7.85398
    g6: LineSegment StartX=-65 StartY=31.2 StartZ=0 EndX=-19 EndY=31.2 EndZ=0
    g7: LineSegment StartX=-65 StartY=11.2 StartZ=0 EndX=-19 EndY=11.2 EndZ=0
    g8: Circle CenterX=-78.51 CenterY=34.8 CenterZ=0 NormalX=0 NormalY=0 NormalZ=1 AngleXU=0 Radius=1.8
    g9: Circle CenterX=-5.6 CenterY=34.8 CenterZ=0 NormalX=0 NormalY=0 NormalZ=1 AngleXU=0 Radius=1.8
    g10: Circle CenterX=-5.6 CenterY=7.6 CenterZ=0 NormalX=0 NormalY=0 NormalZ=1 AngleXU=0 Radius=1.8
    g11: Circle CenterX=-78.51 CenterY=7.6 CenterZ=0 NormalX=0 NormalY=0 NormalZ=1 AngleXU=0 Radius=1.8
  constraints (26):
    c: Coincident(g0,g1)
    c: Coincident(g1,g2)
    c: Coincident(g2,g3)
    c: Coincident(g3,g0)
    c: Horizontal(g0)
    c: Horizontal(g2)
    c: Vertical(g1)
    c: Vertical(g3)
    c: Coincident(g0,g-5)
    c: Coincident(g1,g-6)
    c: Tangent(g4,g6) = 1.5708
    c: Tangent(g4,g7) = -1.5708
    c: Tangent(g5,g6) = 1.5708
    c: Tangent(g5,g7) = -1.5708
    c: Equal(g4,g5)
    c: Equal(g5,g-9)
    c: Coincident(g5,g-9)
    c: Coincident(g4,g-8)
    c: Equal(g8,g-11)
    c: Equal(g11,g-12)
    c: Equal(g10,g-13)
    c: Equal(g9,g-14)
    c: Coincident(g9,g-14)
    c: Coincident(g10,g-13)
    c: Coincident(g11,g-12)
    c: Coincident(g8,g-11)
FEATURE [Sketcher::SketchObject] Sketch084  label="lato sx pistola - spazi anteriori per viti"
  ArcFitTolerance = 1e-06
  AttachmentSupport = -> [XZ_Plane]
  ExternalGeometry = -> [Sketch082]
  FullyConstrained = true
  MakeInternals = false
  MapMode = 5
  Placement = pos=(0,0,0) rot=(1,0,0;1.5708rad)
  sketch-geometry (24):
    g0: ArcOfCircle CenterX=-78.51 CenterY=34.8 CenterZ=0 NormalX=0 NormalY=0 NormalZ=1 AngleXU=0 Radius=3.5 StartAngle=4.71239 EndAngle=6.28319
    g1: ArcOfCircle CenterX=-5.6 CenterY=34.8 CenterZ=0 NormalX=0 NormalY=0 NormalZ=1 AngleXU=0 Radius=3.5 StartAngle=3.14159 EndAngle=4.71239
    g2: ArcOfCircle CenterX=-78.51 CenterY=7.6 CenterZ=0 NormalX=0 NormalY=0 NormalZ=1 AngleXU=0 Radius=3.5 StartAngle=3.99598e-11 EndAngle=1.5708
    g3: ArcOfCircle CenterX=-5.6 CenterY=7.6 CenterZ=0 NormalX=0 NormalY=0 NormalZ=1 AngleXU=0 Radius=3.5 StartAngle=1.5708 EndAngle=3.14159
    g4: LineSegment StartX=0 StartY=11.1 StartZ=0 EndX=-5.6 EndY=11.1 EndZ=0
    g5: LineSegment StartX=-9.1 StartY=7.6 StartZ=0 EndX=-9.1 EndY=3.2 EndZ=0
    g6: LineSegment StartX=-75.01 StartY=39.2 StartZ=0 EndX=-75.01 EndY=34.8 EndZ=0
    g7: LineSegment StartX=-82.8 StartY=31.3 StartZ=0 EndX=-78.51 EndY=31.3 EndZ=0
    g8: LineSegment StartX=-82.8 StartY=11.1 StartZ=0 EndX=-78.51 EndY=11.1 EndZ=0
    g9: LineSegment StartX=-75.01 StartY=7.6 StartZ=0 EndX=-75.01 EndY=3.2 EndZ=0
    g10: LineSegment StartX=-9.1 StartY=39.2 StartZ=0 EndX=-9.1 EndY=34.8 EndZ=0
    g11: LineSegment StartX=-5.6 StartY=31.3 StartZ=0 EndX=0 EndY=31.3 EndZ=0
    g12: LineSegment StartX=-9.1 StartY=39.2 StartZ=0 EndX=0 EndY=39.2 EndZ=0
    g13: LineSegment StartX=0 StartY=39.2 StartZ=0 EndX=0 EndY=31.3 EndZ=0
    g14: LineSegment StartX=0 StartY=11.1 StartZ=0 EndX=0 EndY=3.2 EndZ=0
    g15: LineSegment StartX=0 StartY=3.2 StartZ=0 EndX=-9.1 EndY=3.2 EndZ=0
    g16: LineSegment StartX=-75.01 StartY=3.2 StartZ=0 EndX=-82.8 EndY=3.2 EndZ=0
    g17: LineSegment StartX=-82.8 StartY=3.2 StartZ=0 EndX=-82.8 EndY=11.1 EndZ=0
    g18: LineSegment StartX=-82.8 StartY=31.3 StartZ=0 EndX=-82.8 EndY=39.2 EndZ=0
    g19: LineSegment StartX=-82.8 StartY=39.2 StartZ=0 EndX=-75.01 EndY=39.2 EndZ=0
    g20: Circle CenterX=-78.51 CenterY=34.8 CenterZ=0 NormalX=0 NormalY=0 NormalZ=1 AngleXU=0 Radius=1.8
    g21: Circle CenterX=-5.6 CenterY=34.8 CenterZ=0 NormalX=0 NormalY=0 NormalZ=1 AngleXU=0 Radius=1.8
    g22: Circle CenterX=-5.6 CenterY=7.6 CenterZ=0 NormalX=0 NormalY=0 NormalZ=1 AngleXU=0 Radius=1.8
    g23: Circle CenterX=-78.51 CenterY=7.6 CenterZ=0 NormalX=0 NormalY=0 NormalZ=1 AngleXU=0 Radius=1.8
  constraints (56):
    c: Radius(g0) = 3.5
    c: Coincident(g0,g-5)
    c: Radius(g1) = 3.5
    c: Coincident(g1,g-10)
    c: Radius(g2) = 3.5
    c: Coincident(g2,g-4)
    c: Radius(g3) = 3.5
    c: Coincident(g3,g-9)
    c: Horizontal(g4)
    c: Vertical(g5)
    c: Vertical(g6)
    c: Horizontal(g7)
    c: Horizontal(g8)
    c: Vertical(g9)
    c: Vertical(g10)
    c: Horizontal(g11)
    c: Tangent(g11,g1) = -1.5708
    c: Tangent(g1,g10) = -1.5708
    c: Tangent(g3,g5) = -1.5708
    c: Tangent(g3,g4) = -1.5708
    c: Tangent(g9,g2) = 1.5708
    c: Tangent(g8,g2) = 1.5708
    c: Tangent(g7,g0) = -1.5708
    c: Tangent(g0,g6) = 1.5708
    c: PointOnObject(g10,g-7)
    c: PointOnObject(g11,g-11)
    c: PointOnObject(g4,g-11)
    c: PointOnObject(g5,g-8)
    c: PointOnObject(g9,g-8)
    c: PointOnObject(g8,g-6)
    c: PointOnObject(g7,g-6)
    c: PointOnObject(g6,g-7)
    c: Coincident(g12,g10)
    c: Coincident(g12,g-11)
    c: Coincident(g13,g12)
    c: Coincident(g13,g11)
    c: Coincident(g14,g4)
    c: Coincident(g14,g-11)
    c: Coincident(g15,g14)
    c: Coincident(g15,g5)
    c: Coincident(g16,g9)
    c: Coincident(g16,g-8)
    c: Coincident(g17,g16)
    c: Coincident(g17,g8)
    c: Coincident(g18,g7)
    c: Coincident(g18,g-7)
    c: Coincident(g19,g18)
    c: Coincident(g19,g6)
    c: Equal(g21,g-10)
    c: Equal(g-9,g22)
    c: Equal(g23,g-4)
    c: Equal(g20,g-5)
    c: Coincident(g20,g0)
    c: Coincident(g21,g1)
    c: Coincident(g22,g3)
    c: Coincident(g23,g2)
FEATURE [Sketcher::SketchObject] Sketch085  label="lato dx pistola - spazi anteriori per viti"
  ArcFitTolerance = 1e-06
  AttachmentSupport = -> [XZ_Plane]
  ExternalGeometry = -> [Sketch083]
  FullyConstrained = true
  MakeInternals = false
  MapMode = 5
  Placement = pos=(0,0,0) rot=(1,0,0;1.5708rad)
  sketch-geometry (24):
    g0: ArcOfCircle CenterX=-78.51 CenterY=34.8 CenterZ=0 NormalX=0 NormalY=0 NormalZ=1 AngleXU=0 Radius=3.5 StartAngle=4.71239 EndAngle=6.28319
    g1: ArcOfCircle CenterX=-5.6 CenterY=34.8 CenterZ=0 NormalX=0 NormalY=0 NormalZ=1 AngleXU=0 Radius=3.5 StartAngle=3.14159 EndAngle=4.71239
    g2: ArcOfCircle CenterX=-78.51 CenterY=7.6 CenterZ=0 NormalX=0 NormalY=0 NormalZ=1 AngleXU=0 Radius=3.5 StartAngle=3.99599e-11 EndAngle=1.5708
    g3: ArcOfCircle CenterX=-5.6 CenterY=7.6 CenterZ=0 NormalX=0 NormalY=0 NormalZ=1 AngleXU=0 Radius=3.5 StartAngle=1.5708 EndAngle=3.14159
    g4: LineSegment StartX=-9.1 StartY=39.2 StartZ=0 EndX=-9.1 EndY=34.8 EndZ=0
    g5: LineSegment StartX=-5.6 StartY=31.3 StartZ=0 EndX=0 EndY=31.3 EndZ=0
    g6: LineSegment StartX=-5.6 StartY=11.1 StartZ=0 EndX=0 EndY=11.1 EndZ=0
    g7: LineSegment StartX=-9.1 StartY=7.6 StartZ=0 EndX=-9.1 EndY=3.2 EndZ=0
    g8: LineSegment StartX=-82.8 StartY=11.1 StartZ=0 EndX=-78.51 EndY=11.1 EndZ=0
    g9: LineSegment StartX=-75.01 StartY=7.6 StartZ=0 EndX=-75.01 EndY=3.2 EndZ=0
    g10: LineSegment StartX=-82.8 StartY=31.3 StartZ=0 EndX=-78.51 EndY=31.3 EndZ=0
    g11: LineSegment StartX=-75.01 StartY=34.8 StartZ=0 EndX=-75.01 EndY=39.2 EndZ=0
    g12: LineSegment StartX=-75.01 StartY=3.2 StartZ=0 EndX=-82.8 EndY=3.2 EndZ=0
    g13: LineSegment StartX=-82.8 StartY=3.2 StartZ=0 EndX=-82.8 EndY=11.1 EndZ=0
    g14: LineSegment StartX=-82.8 StartY=31.3 StartZ=0 EndX=-82.8 EndY=39.2 EndZ=0
    g15: LineSegment StartX=-82.8 StartY=39.2 StartZ=0 EndX=-75.01 EndY=39.2 EndZ=0
    g16: LineSegment StartX=-9.1 StartY=39.2 StartZ=0 EndX=0 EndY=39.2 EndZ=0
    g17: LineSegment StartX=0 StartY=39.2 StartZ=0 EndX=0 EndY=31.3 EndZ=0
    g18: LineSegment StartX=-9.1 StartY=3.2 StartZ=0 EndX=0 EndY=3.2 EndZ=0
    g19: LineSegment StartX=0 StartY=3.2 StartZ=0 EndX=0 EndY=11.1 EndZ=0
    g20: Circle CenterX=-78.51 CenterY=34.8 CenterZ=0 NormalX=0 NormalY=0 NormalZ=1 AngleXU=0 Radius=1.8
    g21: Circle CenterX=-5.6 CenterY=34.8 CenterZ=0 NormalX=0 NormalY=0 NormalZ=1 AngleXU=0 Radius=1.8
    g22: Circle CenterX=-5.6 CenterY=7.6 CenterZ=0 NormalX=0 NormalY=0 NormalZ=1 AngleXU=0 Radius=1.8
    g23: Circle CenterX=-78.51 CenterY=7.6 CenterZ=0 NormalX=0 NormalY=0 NormalZ=1 AngleXU=0 Radius=1.8
  constraints (56):
    c: Radius(g0) = 3.5
    c: Coincident(g0,g-3)
    c: Radius(g1) = 3.5
    c: Coincident(g1,g-5)
    c: Radius(g2) = 3.5
    c: Coincident(g2,g-4)
    c: Radius(g3) = 3.5
    c: Coincident(g3,g-6)
    c: Vertical(g4)
    c: Horizontal(g5)
    c: Horizontal(g6)
    c: Vertical(g7)
    c: Horizontal(g8)
    c: Vertical(g9)
    c: Horizontal(g10)
    c: Vertical(g11)
    c: Tangent(g4,g1) = -1.5708
    c: Tangent(g5,g1) = -1.5708
    c: Tangent(g6,g3) = 1.5708
    c: Tangent(g7,g3) = -1.5708
    c: Tangent(g9,g2) = 1.5708
    c: Tangent(g8,g2) = 1.5708
    c: Tangent(g10,g0) = -1.5708
    c: Tangent(g11,g0) = -1.5708
    c: PointOnObject(g11,g-9)
    c: PointOnObject(g4,g-9)
    c: PointOnObject(g5,g-10)
    c: PointOnObject(g6,g-10)
    c: PointOnObject(g7,g-7)
    c: PointOnObject(g9,g-7)
    c: PointOnObject(g8,g-8)
    c: PointOnObject(g10,g-8)
    c: Coincident(g12,g9)
    c: Coincident(g12,g-8)
    c: Coincident(g13,g12)
    c: Coincident(g13,g8)
    c: Coincident(g14,g10)
    c: Coincident(g14,g-9)
    c: Coincident(g15,g14)
    c: Coincident(g15,g11)
    c: Coincident(g16,g4)
    c: Coincident(g16,g-10)
    c: Coincident(g17,g16)
    c: Coincident(g17,g5)
    c: Coincident(g18,g7)
    c: Coincident(g18,g-10)
    c: Coincident(g19,g18)
    c: Coincident(g19,g6)
    c: Equal(g20,g-3)
    c: Equal(g21,g-5)
    c: Equal(g22,g-6)
    c: Equal(g23,g-4)
    c: Coincident(g20,g0)
    c: Coincident(g21,g1)
    c: Coincident(g22,g3)
    c: Coincident(g23,g2)
FEATURE [Part::Extrusion] Extrude082  label="Extrude lato sx pistola - disegno anteriore"
  Base = -> Sketch082
  Dir = (0,-1,2e-16)
  DirMode = 2
  FaceMakerClass = Part::FaceMakerBullseye
  FaceMakerMode = 3
  LengthFwd = -1.6
  LengthRev = 0
  Placement = pos=(0,2,0) rot=(0,0,1;0rad)
  Solid = true
  Symmetric = false
FEATURE [Part::Extrusion] Extrude083  label="Extrude lato dx pistola - disegno anteriore"
  Base = -> Sketch083
  Dir = (0,-1,2e-16)
  DirMode = 2
  FaceMakerClass = Part::FaceMakerBullseye
  FaceMakerMode = 3
  LengthFwd = 1.6
  LengthRev = 0
  Placement = pos=(0,-2,0) rot=(0,0,1;0rad)
  Solid = true
  Symmetric = false
FEATURE [Part::Extrusion] Extrude084  label="Extrude lato sx pistola - spazi anteriori per viti"
  Base = -> Sketch084
  Dir = (0,-1,2e-16)
  DirMode = 2
  FaceMakerClass = Part::FaceMakerBullseye
  FaceMakerMode = 3
  LengthFwd = -1.6
  LengthRev = 0
  Placement = pos=(0,2,0) rot=(0,0,1;0rad)
  Solid = true
  Symmetric = false
FEATURE [Part::Extrusion] Extrude085  label="Extrude lato dx pistola - spazi anteriori per viti"
  Base = -> Sketch085
  Dir = (0,-1,2e-16)
  DirMode = 2
  FaceMakerClass = Part::FaceMakerBullseye
  FaceMakerMode = 3
  LengthFwd = 0.8
  LengthRev = 0
  Placement = pos=(0,-2.8,0) rot=(0,0,1;0rad)
  Solid = true
  Symmetric = false
FEATURE [Part::Cut] Cut048  label="Extrude lato dx pistola - disegno anterioro con fori viti"
  Base = -> Extrude083
  Refine = true
  Tool = -> Extrude085
FEATURE [Part::MultiFuse] Fusion006
  Refine = true
  Shapes = -> [Cut046,Cut048]
FEATURE [Sketcher::SketchObject] Sketch087  label="lato sx pistola - rialzo posteriore"
  ArcFitTolerance = 1e-06
  AttachmentSupport = -> [XZ_Plane]
  ExternalGeometry = -> [Sketch074]
  FullyConstrained = true
  MakeInternals = false
  MapMode = 5
  Placement = pos=(0,0,0) rot=(1,0,0;1.5708rad)
  sketch-geometry (10):
    g0: LineSegment StartX=-181.33 StartY=20.0744 StartZ=0 EndX=-144.029 EndY=20.0744 EndZ=0
    g1: LineSegment StartX=-137.815 StartY=39.2 StartZ=0 EndX=-144.029 EndY=20.0744 EndZ=0
    g2: LineSegment StartX=-178.754 StartY=39.2 StartZ=0 EndX=-137.815 EndY=39.2 EndZ=0
    g3: ArcOfCircle CenterX=-184.08 CenterY=34.8 CenterZ=0 NormalX=0 NormalY=0 NormalZ=1 AngleXU=0 Radius=3.5 StartAngle=4.71239 EndAngle=5.93412
    g4: LineSegment StartX=-178.754 StartY=39.2 StartZ=0 EndX=-180.791 EndY=33.6029 EndZ=0
    g5: GeomPoint [constr] X=-181.33 Y=20.0744 Z=0
    g6: LineSegment [constr] StartX=-181.33 StartY=20.0744 StartZ=0 EndX=-192.176 EndY=-3.18451 EndZ=0
    g7: LineSegment StartX=-184.08 StartY=31.3 StartZ=0 EndX=-186.139 EndY=31.3 EndZ=0
    g8: LineSegment StartX=-186.139 StartY=31.3 StartZ=0 EndX=-190.224 EndY=20.0744 EndZ=0
    g9: LineSegment StartX=-181.33 StartY=20.0744 StartZ=0 EndX=-190.224 EndY=20.0744 EndZ=0
  constraints (23):
    c: Horizontal(g0)
    c: Tangent(g1,g-5)
    c: PointOnObject(g2,g-4)
    c: Coincident(g2,g1)
    c: Radius(g3) = 3.5
    c: Coincident(g3,g-10)
    c: Horizontal(g2)
    c: Equal(g1,g-3)
    c: Coincident(g0,g1)
    c: Tangent(g4,g3) = 1.5708
    c: Coincident(g4,g2)
    c: Coincident(g6,g5)
    c: Tangent(g6,g-11) = -1.5708
    c: Coincident(g0,g5)
    c: Parallel(g4,g-3)
    c: Horizontal(g7)
    c: Parallel(g8,g-3)
    c: Tangent(g3,g7) = 1.5708
    c: Coincident(g8,g7)
    c: Coincident(g9,g0)
    c: Horizontal(g9)
    c: Coincident(g9,g8)
    c: DistanceX(g-8,g7) = 3.8
FEATURE [Sketcher::SketchObject] Sketch086  label="lato sx pistola - rialzo centrale"
  ArcFitTolerance = 1e-06
  AttachmentOffset = pos=(0,2,0) rot=(0,0,1;0rad)
  AttachmentSupport = -> [XZ_Plane]
  ExternalGeometry = -> [Sketch074,Sketch087]
  FullyConstrained = true
  MakeInternals = false
  MapMode = 5
  Placement = pos=(0,4e-16,2) rot=(1,0,0;1.5708rad)
  sketch-geometry (6):
    g0: LineSegment StartX=-137.815 StartY=37.2 StartZ=0 EndX=-142.793 EndY=21.8787 EndZ=0
    g1: LineSegment StartX=-137.815 StartY=37.2 StartZ=0 EndX=-110.815 EndY=37.2 EndZ=0
    g2: LineSegment StartX=-110.815 StartY=37.2 StartZ=0 EndX=-112.201 EndY=32.9344 EndZ=0
    g3: LineSegment StartX=-127.418 StartY=21.8787 StartZ=0 EndX=-142.793 EndY=21.8787 EndZ=0
    g4: ArcOfCircle CenterX=-127.418 CenterY=37.8787 CenterZ=0 NormalX=0 NormalY=0 NormalZ=1 AngleXU=0 Radius=16 StartAngle=4.71239 EndAngle=5.96903
    g5: GeomPoint [constr] X=-115.793 Y=21.8787 Z=0
  constraints (15):
    c: Distance(g1) = 27
    c: Coincident(g1,g0)
    c: PointOnObject(g1,g-4)
    c: Parallel(g2,g-3)
    c: Coincident(g2,g1)
    c: Horizontal(g3)
    c: PointOnObject(g5,g2)
    c: PointOnObject(g5,g3)
    c: Tangent(g2,g4) = 1.5708
    c: Tangent(g3,g4) = 1.5708
    c: Radius(g4) = 16
    c: Parallel(g0,g-7)
    c: Coincident(g0,g-7)
    c: Coincident(g0,g3)
    c: Distance(g0,g-7) = 4
FEATURE [Sketcher::SketchObject] Sketch088  label="lato sx pistola - rialzo impugnatura"
  ArcFitTolerance = 1e-06
  AttachmentSupport = -> [XZ_Plane]
  ExternalGeometry = -> [Sketch074,Sketch087]
  FullyConstrained = true
  MakeInternals = false
  MapMode = 5
  Placement = pos=(0,0,0) rot=(1,0,0;1.5708rad)
  sketch-geometry (11):
    g0: LineSegment StartX=-144.029 StartY=20.0744 StartZ=0 EndX=-176.685 EndY=-80.4316 EndZ=0
    g1: Circle CenterX=-213.443 CenterY=-76.8316 CenterZ=0 NormalX=0 NormalY=0 NormalZ=1 AngleXU=0 Radius=3
    g2: Circle CenterX=-179.305 CenterY=-76.8316 CenterZ=0 NormalX=0 NormalY=0 NormalZ=1 AngleXU=0 Radius=3
    g3: LineSegment StartX=-176.685 StartY=-80.4316 StartZ=0 EndX=-215.932 EndY=-80.4316 EndZ=0
    g4: LineSegment StartX=-192.176 StartY=-3.18451 StartZ=0 EndX=-215.42 EndY=-53.0314 EndZ=0
    g5: ArcOfCircle CenterX=-184.801 CenterY=-67.3089 CenterZ=0 NormalX=0 NormalY=0 NormalZ=1 AngleXU=0 Radius=33.7833 StartAngle=2.70526 EndAngle=3.54053
    g6: LineSegment [constr] StartX=-192.176 StartY=-3.18451 StartZ=0 EndX=-181.33 EndY=20.0744 EndZ=0
    g7: LineSegment StartX=-144.029 StartY=20.0744 StartZ=0 EndX=-190.224 EndY=20.0744 EndZ=0
    g8: LineSegment StartX=-190.224 StartY=20.0744 StartZ=0 EndX=-191.316 EndY=17.0744 EndZ=0
    g9: LineSegment StartX=-191.316 StartY=17.0744 StartZ=0 EndX=-182.729 EndY=17.0744 EndZ=0
    g10: LineSegment StartX=-192.176 StartY=-3.18451 StartZ=0 EndX=-182.729 EndY=17.0744 EndZ=0
  constraints (26):
    c: Coincident(g0,g-5)
    c: Coincident(g2,g-10)
    c: Coincident(g1,g-9)
    c: Diameter(g2) = 6
    c: Diameter(g1) = 6
    c: Coincident(g3,g0)
    c: Coincident(g3,g-4)
    c: Equal(g4,g-15)
    c: Parallel(g4,g-15)
    c: Coincident(g4,g-15)
    c: Coincident(g5,g4)
    c: Coincident(g5,g3)
    c: Tangent(g6,g4) = 1.5708
    c: PointOnObject(g6,g-13)
    c: Coincident(g0,g-13)
    c: Coincident(g7,g0)
    c: Coincident(g7,g-14)
    c: Coincident(g8,g7)
    c: Coincident(g9,g8)
    c: Horizontal(g9)
    c: PointOnObject(g9,g6)
    c: Coincident(g10,g4)
    c: Coincident(g10,g9)
    c: DistanceY(g8,g8) = 3
    c: Parallel(g8,g-16)
    c: Tangent(g5,g-3)
FEATURE [Sketcher::SketchObject] Sketch089  label="lato sx pistola - disegno centrale"
  ArcFitTolerance = 1e-06
  AttachmentSupport = -> [XZ_Plane]
  ExternalGeometry = -> [Sketch086]
  FullyConstrained = true
  MakeInternals = false
  MapMode = 5
  Placement = pos=(0,0,0) rot=(1,0,0;1.5708rad)
  sketch-geometry (4):
    g0: LineSegment StartX=-130.215 StartY=39.2 StartZ=0 EndX=-119.215 EndY=39.2 EndZ=0
    g1: LineSegment StartX=-130.215 StartY=39.2 StartZ=0 EndX=-132.81 EndY=31.2111 EndZ=0
    g2: LineSegment StartX=-119.215 StartY=39.2 StartZ=0 EndX=-121.81 EndY=31.2111 EndZ=0
    g3: LineSegment StartX=-132.81 StartY=31.2111 StartZ=0 EndX=-121.81 EndY=31.2111 EndZ=0
  constraints (11):
    c: Horizontal(g3)
    c: Parallel(g2,g-4)
    c: Parallel(g1,g-4)
    c: Distance(g1) = 8.4
    c: DistanceX(g0,g0) = 11
    c: Tangent(g0,g-3)
    c: Coincident(g1,g0)
    c: Coincident(g2,g0)
    c: Coincident(g3,g1)
    c: Coincident(g3,g2)
    c: DistanceX(g0,g-4) = 8.4
FEATURE [Sketcher::SketchObject] Sketch090  label="lato sx pistola - disegno pre centrale"
  ArcFitTolerance = 1e-06
  AttachmentSupport = -> [XZ_Plane]
  ExternalGeometry = -> [Sketch074,Sketch086]
  FullyConstrained = true
  MakeInternals = false
  MapMode = 5
  Placement = pos=(0,0,0) rot=(1,0,0;1.5708rad)
  sketch-geometry (4):
    g0: LineSegment StartX=-106.615 StartY=36.8 StartZ=0 EndX=-89.6146 EndY=36.8 EndZ=0
    g1: LineSegment StartX=-110.254 StartY=26.8 StartZ=0 EndX=-89.6146 EndY=26.8 EndZ=0
    g2: LineSegment StartX=-106.615 StartY=36.8 StartZ=0 EndX=-110.254 EndY=26.8 EndZ=0
    g3: ArcOfCircle CenterX=-94.6146 CenterY=31.8 CenterZ=0 NormalX=0 NormalY=0 NormalZ=1 AngleXU=0 Radius=7.07107 StartAngle=5.49779 EndAngle=7.06858
  constraints (13):
    c: Horizontal(g0)
    c: Horizontal(g1)
    c: Parallel(g-3,g2)
    c: Coincident(g0,g2)
    c: DistanceY(g2,g2) = 10
    c: Coincident(g1,g2)
    c: DistanceX(g0,g0) = 17
    c: DistanceX(g0,g1) = 0
    c: Coincident(g3,g1)
    c: DistanceX(g-5,g0) = 4.2
    c: DistanceY(g0,g-5) = 2.4
    c: Coincident(g3,g0)
    c: DistanceX(g3,g0) = 5
FEATURE [PartDesign::Body] Body  label="Struttura pistola"
  AllowCompound = false
  Group = -> [Sketch,Sketch002,Sketch004,DatumPlane,Sketch005,DatumPlane001,CopyCut,Sketch008,Sketch009,Sketch010,Sketch011,Sketch012,Sketch013,Sketch014,Sketch015,Sketch016,Sketch017,Sketch018,Sketch019,Sketch020,Sketch022,Sketch023,Sketch024,Sketch025,Sketch026,Sketch027,Sketch029,Sketch030,Sketch031,Sketch032,Sketch033,Sketch034,Sketch035,Sketch036,Sketch037,Sketch038,Sketch039,Sketch040,Sketch041,Sketch042,+28 more]
  Origin = -> Origin
FEATURE [PartDesign::SubShapeBinder] Binder
  BindCopyOnChange = 0
  BindMode = 0
  ClaimChildren = false
  Context = -> Body006 [Binder.]
  Fuse = false
  MakeFace = true
  OffsetFill = false
  OffsetIntersection = false
  OffsetJoinType = 0
  OffsetOpenResult = false
  PartialLoad = false
  Refine = true
  Relative = true
  Support = -> [Body[Sketch074.]]
  _Version = 2
FEATURE [PartDesign::SubShapeBinder] Binder001
  BindCopyOnChange = 0
  BindMode = 0
  ClaimChildren = false
  Context = -> Body007 [Binder001.]
  Fuse = false
  MakeFace = true
  OffsetFill = false
  OffsetIntersection = false
  OffsetJoinType = 0
  OffsetOpenResult = false
  PartialLoad = false
  Refine = true
  Relative = true
  Support = -> [Body[Sketch075.]]
  _Version = 2
FEATURE [PartDesign::Pad] Pad004
  Direction = (0,1,0)
  Length = 2
  Length2 = 10
  Profile = -> Binder
  Refine = true
  Suppressed = false
  Type = 0
FEATURE [Sketcher::SketchObject] Sketch091  label="Sketch091 - forma anteriore"
  ArcFitTolerance = 1e-06
  AttachmentSupport = -> [Pad004]
  ExternalGeometry = -> [Binder]
  FullyConstrained = true
  MakeInternals = false
  MapMode = 5
  Placement = pos=(0,2,0) rot=(0,0.707107,0.707107;3.14159rad)
  sketch-geometry (12):
    g0: Circle CenterX=5.6 CenterY=34.8 CenterZ=0 NormalX=0 NormalY=0 NormalZ=1 AngleXU=0 Radius=1.8
    g1: Circle CenterX=5.6 CenterY=7.6 CenterZ=0 NormalX=0 NormalY=0 NormalZ=1 AngleXU=0 Radius=1.8
    g2: Circle CenterX=78.51 CenterY=34.8 CenterZ=0 NormalX=0 NormalY=0 NormalZ=1 AngleXU=0 Radius=1.8
    g3: Circle CenterX=78.51 CenterY=7.6 CenterZ=0 NormalX=0 NormalY=0 NormalZ=1 AngleXU=0 Radius=1.8
    g4: LineSegment StartX=0 StartY=39.2 StartZ=0 EndX=0 EndY=3.2 EndZ=0
    g5: LineSegment StartX=0 StartY=3.2 StartZ=0 EndX=82.8 EndY=3.2 EndZ=0
    g6: LineSegment StartX=82.8 StartY=3.2 StartZ=0 EndX=82.8 EndY=39.2 EndZ=0
    g7: LineSegment StartX=82.8 StartY=39.2 StartZ=0 EndX=0 EndY=39.2 EndZ=0
    g8: ArcOfCircle CenterX=19 CenterY=21.2 CenterZ=0 NormalX=0 NormalY=0 NormalZ=1 AngleXU=0 Radius=10 StartAngle=1.5708 EndAngle=4.71239
    g9: ArcOfCircle CenterX=65 CenterY=21.2 CenterZ=0 NormalX=0 NormalY=0 NormalZ=1 AngleXU=0 Radius=10 StartAngle=4.71239 EndAngle=7.85398
    g10: LineSegment StartX=19 StartY=31.2 StartZ=0 EndX=65 EndY=31.2 EndZ=0
    g11: LineSegment StartX=19 StartY=11.2 StartZ=0 EndX=65 EndY=11.2 EndZ=0
  constraints (25):
    c: Equal(g2,g-7)
    c: Equal(g3,g-8)
    c: Equal(g1,g-13)
    c: Equal(g0,g-12)
    c: Coincident(g0,g-12)
    c: Coincident(g1,g-13)
    c: Coincident(g3,g-8)
    c: Coincident(g2,g-7)
    c: Coincident(g4,g-4)
    c: Coincident(g4,g-5)
    c: Coincident(g5,g4)
    c: Coincident(g5,g-6)
    c: Coincident(g6,g5)
    c: PointOnObject(g6,g-3)
    c: Vertical(g6)
    c: Coincident(g7,g6)
    c: Coincident(g7,g4)
    c: Tangent(g8,g10) = 1.5708
    c: Tangent(g8,g11) = -1.5708
    c: Tangent(g9,g10) = 1.5708
    c: Tangent(g9,g11) = -1.5708
    c: Equal(g8,g9)
    c: Radius(g8) = 10
    c: Coincident(g8,g-11)
    c: Coincident(g9,g-9)
FEATURE [PartDesign::Pad] Pad005
  BaseFeature = -> Pad004
  Direction = (0,1,-2e-16)
  Length = 1.6
  Length2 = 10
  Profile = -> Sketch091
  ReferenceAxis = -> Sketch091 [N_Axis]
  Refine = true
  Suppressed = false
  Type = 0
FEATURE [Sketcher::SketchObject] Sketch092  label="Sketch092 - scavi per viti anteriori"
  ArcFitTolerance = 1e-06
  AttachmentSupport = -> [Pad005]
  ExternalGeometry = -> [Binder]
  FullyConstrained = true
  MakeInternals = false
  MapMode = 5
  Placement = pos=(0,3.6,0) rot=(0,0.707107,0.707107;3.14159rad)
  sketch-geometry (20):
    g0: ArcOfCircle CenterX=5.6 CenterY=7.6 CenterZ=0 NormalX=0 NormalY=0 NormalZ=1 AngleXU=0 Radius=3.5 StartAngle=0 EndAngle=1.5708
    g1: ArcOfCircle CenterX=5.6 CenterY=34.8 CenterZ=0 NormalX=0 NormalY=0 NormalZ=1 AngleXU=0 Radius=3.5 StartAngle=4.71239 EndAngle=6.28319
    g2: ArcOfCircle CenterX=78.51 CenterY=34.8 CenterZ=0 NormalX=0 NormalY=0 NormalZ=1 AngleXU=0 Radius=3.5 StartAngle=3.14159 EndAngle=4.71239
    g3: ArcOfCircle CenterX=78.51 CenterY=7.6 CenterZ=0 NormalX=0 NormalY=0 NormalZ=1 AngleXU=0 Radius=3.5 StartAngle=1.5708 EndAngle=3.14159
    g4: LineSegment StartX=0 StartY=3.2 StartZ=0 EndX=0 EndY=11.1 EndZ=0
    g5: LineSegment StartX=0 StartY=11.1 StartZ=0 EndX=5.6 EndY=11.1 EndZ=0
    g6: LineSegment StartX=0 StartY=3.2 StartZ=0 EndX=9.1 EndY=3.2 EndZ=0
    g7: LineSegment StartX=9.1 StartY=3.2 StartZ=0 EndX=9.1 EndY=7.6 EndZ=0
    g8: LineSegment StartX=0 StartY=39.2 StartZ=0 EndX=0 EndY=31.3 EndZ=0
    g9: LineSegment StartX=0 StartY=31.3 StartZ=0 EndX=5.6 EndY=31.3 EndZ=0
    g10: LineSegment StartX=0 StartY=39.2 StartZ=0 EndX=9.1 EndY=39.2 EndZ=0
    g11: LineSegment StartX=9.1 StartY=39.2 StartZ=0 EndX=9.1 EndY=34.8 EndZ=0
    g12: LineSegment StartX=82.8 StartY=39.2 StartZ=0 EndX=75.01 EndY=39.2 EndZ=0
    g13: LineSegment StartX=82.8 StartY=39.2 StartZ=0 EndX=82.8 EndY=31.3 EndZ=0
    g14: LineSegment StartX=82.8 StartY=31.3 StartZ=0 EndX=78.51 EndY=31.3 EndZ=0
    g15: LineSegment StartX=82.8 StartY=3.2 StartZ=0 EndX=75.01 EndY=3.2 EndZ=0
    g16: LineSegment StartX=75.01 StartY=3.2 StartZ=0 EndX=75.01 EndY=7.6 EndZ=0
    g17: LineSegment StartX=82.8 StartY=3.2 StartZ=0 EndX=82.8 EndY=11.1 EndZ=0
    g18: LineSegment StartX=82.8 StartY=11.1 StartZ=0 EndX=78.51 EndY=11.1 EndZ=0
    g19: LineSegment StartX=75.01 StartY=39.2 StartZ=0 EndX=75.01 EndY=34.8 EndZ=0
  constraints (48):
    c: Radius(g0) = 3.5
    c: Coincident(g0,g-10)
    c: Radius(g1) = 3.5
    c: Coincident(g1,g-9)
    c: Radius(g2) = 3.5
    c: Coincident(g2,g-8)
    c: Radius(g3) = 3.5
    c: Coincident(g3,g-7)
    c: Coincident(g4,g-5)
    c: PointOnObject(g4,g-4)
    c: Coincident(g5,g4)
    c: Horizontal(g5)
    c: Coincident(g6,g4)
    c: PointOnObject(g6,g-5)
    c: Coincident(g7,g6)
    c: Vertical(g7)
    c: Coincident(g8,g-4)
    c: PointOnObject(g8,g-4)
    c: Coincident(g9,g8)
    c: Horizontal(g9)
    c: Coincident(g10,g8)
    c: PointOnObject(g10,g-3)
    c: Coincident(g11,g10)
    c: Vertical(g11)
    c: PointOnObject(g12,g-3)
    c: PointOnObject(g12,g-3)
    c: Coincident(g13,g12)
    c: Vertical(g13)
    c: Coincident(g14,g13)
    c: Horizontal(g14)
    c: Coincident(g15,g-6)
    c: PointOnObject(g15,g-5)
    c: Coincident(g16,g15)
    c: Vertical(g16)
    c: Coincident(g17,g15)
    c: Coincident(g18,g17)
    c: Horizontal(g18)
    c: Tangent(g3,g18) = -1.5708
    c: Tangent(g16,g3) = 1.5708
    c: Coincident(g19,g12)
    c: Vertical(g19)
    c: Tangent(g2,g19) = -1.5708
    c: Tangent(g2,g14) = 1.5708
    c: Tangent(g0,g7) = -1.5708
    c: Tangent(g0,g5) = 1.5708
    c: Tangent(g9,g1) = -1.5708
    c: Tangent(g1,g11) = 1.5708
    c: Tangent(g17,g13)
FEATURE [PartDesign::Pocket] Pocket001
  BaseFeature = -> Pad005
  Direction = (0,-1,2e-16)
  Length = 1.6
  Length2 = 5
  Profile = -> Sketch092
  ReferenceAxis = -> Sketch092 [N_Axis]
  Refine = true
  Suppressed = false
  Type = 0
FEATURE [Sketcher::SketchObject] Sketch093  label="Sketch093 - scavi interni pulsanti"
  ArcFitTolerance = 1e-06
  AttachmentSupport = -> [Pad004]
  ExternalGeometry = -> [Binder]
  FullyConstrained = true
  MakeInternals = false
  MapMode = 5
  Placement = pos=(0,9e-16,0) rot=(1,0,0;1.5708rad)
  sketch-geometry (3):
    g0: Circle CenterX=-65 CenterY=21.2 CenterZ=0 NormalX=0 NormalY=0 NormalZ=1 AngleXU=0 Radius=7.3
    g1: Circle CenterX=-42 CenterY=21.2 CenterZ=0 NormalX=0 NormalY=0 NormalZ=1 AngleXU=0 Radius=7.3
    g2: Circle CenterX=-19 CenterY=21.2 CenterZ=0 NormalX=0 NormalY=0 NormalZ=1 AngleXU=0 Radius=7.3
  constraints (6):
    c: Coincident(g0,g-3)
    c: Coincident(g1,g-4)
    c: Coincident(g2,g-5)
    c: Diameter(g0) = 14.6
    c: Diameter(g1) = 14.6
    c: Diameter(g2) = 14.6
FEATURE [PartDesign::Pocket] Pocket002
  BaseFeature = -> Pocket001
  Direction = (0,1,-2e-16)
  Length = 1.2
  Length2 = 5
  Profile = -> Sketch093
  ReferenceAxis = -> Sketch093 [N_Axis]
  Refine = true
  Suppressed = false
  Type = 0
FEATURE [Sketcher::SketchObject] Sketch094  label="Sketch094 - forma centrale"
  ArcFitTolerance = 1e-06
  AttachmentSupport = -> [Pad004]
  ExternalGeometry = -> [Binder]
  FullyConstrained = true
  MakeInternals = false
  MapMode = 5
  Placement = pos=(0,2,0) rot=(0,0.707107,0.707107;3.14159rad)
  sketch-geometry (4):
    g0: LineSegment StartX=137.815 StartY=39.2 StartZ=0 EndX=142.655 EndY=24.303 EndZ=0
    g1: LineSegment StartX=110.815 StartY=24.303 StartZ=0 EndX=142.655 EndY=24.303 EndZ=0
    g2: LineSegment StartX=137.815 StartY=39.2 StartZ=0 EndX=110.815 EndY=39.2 EndZ=0
    g3: ArcOfCircle CenterX=92.2534 CenterY=31.7515 CenterZ=0 NormalX=0 NormalY=0 NormalZ=1 AngleXU=0 Radius=20 StartAngle=5.90156 EndAngle=6.66481
  constraints (12):
    c: PointOnObject(g0,g-3)
    c: Tangent(g0,g-5)
    c: Horizontal(g1)
    c: Coincident(g1,g0)
    c: Coincident(g2,g0)
    c: PointOnObject(g2,g-3)
    c: DistanceX(g2,g2) = 27
    c: Vertical(g1,g2)
    c: Coincident(g3,g2)
    c: Radius(g3) = 20
    c: Coincident(g3,g1)
    c: DistanceY(g-6,g0) = 4
FEATURE [PartDesign::Pad] Pad006
  BaseFeature = -> Pocket002
  Direction = (0,1,-2e-16)
  Length = 0.8
  Length2 = 10
  Profile = -> Sketch094
  ReferenceAxis = -> Sketch094 [N_Axis]
  Refine = true
  Suppressed = false
  Type = 0
FEATURE [Sketcher::SketchObject] Sketch095  label="Sketch095 - forma posteriore"
  ArcFitTolerance = 1e-06
  AttachmentSupport = -> [Pad004]
  ExternalGeometry = -> [Binder]
  FullyConstrained = true
  MakeInternals = false
  MapMode = 5
  Placement = pos=(0,2,0) rot=(0,0.707107,0.707107;3.14159rad)
  sketch-geometry (15):
    g0: LineSegment StartX=137.815 StartY=39.2 StartZ=0 EndX=143.955 EndY=20.303 EndZ=0
    g1: LineSegment StartX=143.955 StartY=20.303 StartZ=0 EndX=190.141 EndY=20.303 EndZ=0
    g2: ArcOfCircle CenterX=184.08 CenterY=34.8 CenterZ=0 NormalX=0 NormalY=0 NormalZ=1 AngleXU=0 Radius=3.5 StartAngle=3.49066 EndAngle=4.71239
    g3: LineSegment StartX=180.791 StartY=33.6029 StartZ=0 EndX=178.754 EndY=39.2 EndZ=0
    g4: LineSegment StartX=184.08 StartY=31.3 StartZ=0 EndX=186.139 EndY=31.3 EndZ=0
    g5: LineSegment StartX=190.141 StartY=20.303 StartZ=0 EndX=186.139 EndY=31.3 EndZ=0
    g6: LineSegment StartX=137.815 StartY=39.2 StartZ=0 EndX=156.815 EndY=39.2 EndZ=0
    g7: LineSegment StartX=178.754 StartY=39.2 StartZ=0 EndX=168.815 EndY=39.2 EndZ=0
    g8: LineSegment StartX=156.815 StartY=31.2 StartZ=0 EndX=168.815 EndY=31.2 EndZ=0
    g9: ArcOfCircle CenterX=176.411 CenterY=35.2 CenterZ=0 NormalX=0 NormalY=0 NormalZ=1 AngleXU=0 Radius=20 StartAngle=2.94023 EndAngle=3.34295
    g10: ArcOfCircle CenterX=188.411 CenterY=35.2 CenterZ=0 NormalX=0 NormalY=0 NormalZ=1 AngleXU=0 Radius=20 StartAngle=2.94023 EndAngle=3.34295
    g11: LineSegment StartX=157.815 StartY=39.2 StartZ=0 EndX=167.815 EndY=39.2 EndZ=0
    g12: LineSegment StartX=157.436 StartY=36.2 StartZ=0 EndX=167.436 EndY=36.2 EndZ=0
    g13: ArcOfCircle CenterX=177.411 CenterY=35.2 CenterZ=0 NormalX=0 NormalY=0 NormalZ=1 AngleXU=0 Radius=20 StartAngle=2.94023 EndAngle=3.09157
    g14: ArcOfCircle CenterX=187.411 CenterY=35.2 CenterZ=0 NormalX=0 NormalY=0 NormalZ=1 AngleXU=0 Radius=20 StartAngle=2.94023 EndAngle=3.09157
  constraints (46):
    c: PointOnObject(g0,g-3)
    c: Tangent(g0,g-6)
    c: Coincident(g1,g0)
    c: Horizontal(g1)
    c: Radius(g2) = 3.5
    c: Coincident(g2,g-5)
    c: PointOnObject(g3,g-3)
    c: Parallel(g3,g-4)
    c: Tangent(g3,g2) = 1.5708
    c: Horizontal(g4)
    c: Tangent(g4,g2) = -1.5708
    c: Coincident(g5,g1)
    c: Parallel(g5,g-4)
    c: Coincident(g5,g4)
    c: DistanceX(g4,g-8) = 3.8
    c: Coincident(g6,g0)
    c: PointOnObject(g6,g-3)
    c: Coincident(g7,g3)
    c: PointOnObject(g7,g-3)
    c: Horizontal(g8)
    c: DistanceX(g6,g7) = 12
    c: Vertical(g8,g6)
    c: Vertical(g7,g8)
    c: DistanceY(g8,g6) = 8
    c: Coincident(g9,g8)
    c: Coincident(g9,g6)
    c: Coincident(g10,g7)
    c: Coincident(g10,g8)
    c: Radius(g9) = 20
    c: Radius(g10) = 20
    c: PointOnObject(g11,g-3)
    c: PointOnObject(g11,g-3)
    c: DistanceX(g11,g11) = 10
    c: DistanceX(g6,g11) = 1
    c: Horizontal(g12)
    c: Equal(g12,g11)
    c: DistanceY(g12,g11) = 3
    c: Coincident(g13,g11)
    c: Coincident(g13,g12)
    c: Radius(g13) = 20
    c: Coincident(g14,g11)
    c: Coincident(g14,g12)
    c: Radius(g14) = 20
    c: DistanceX(g0,g6) = 19
    c: Horizontal(g9,g13)
    c: Horizontal(g0,g-4)
FEATURE [PartDesign::Pad] Pad007
  BaseFeature = -> Pad006
  Direction = (0,1,-2e-16)
  Length = 2
  Length2 = 10
  Profile = -> Sketch095
  ReferenceAxis = -> Sketch095 [N_Axis]
  Refine = true
  Suppressed = false
  Type = 0
FEATURE [Sketcher::SketchObject] Sketch096  label="Sketch096 - forma impugnatura"
  ArcFitTolerance = 1e-06
  AttachmentSupport = -> [Pad004]
  ExternalGeometry = -> [Binder]
  FullyConstrained = true
  MakeInternals = false
  MapMode = 5
  Placement = pos=(0,2,0) rot=(0,0.707107,0.707107;3.14159rad)
  sketch-geometry (8):
    g0: LineSegment StartX=176.685 StartY=-80.4316 StartZ=0 EndX=143.955 EndY=20.303 EndZ=0
    g1: LineSegment StartX=176.685 StartY=-80.4316 StartZ=0 EndX=215.932 EndY=-80.4316 EndZ=0
    g2: Circle CenterX=179.305 CenterY=-76.8316 CenterZ=0 NormalX=0 NormalY=0 NormalZ=1 AngleXU=0 Radius=3
    g3: Circle CenterX=213.443 CenterY=-76.8316 CenterZ=0 NormalX=0 NormalY=0 NormalZ=1 AngleXU=0 Radius=3
    g4: LineSegment StartX=143.955 StartY=20.303 StartZ=0 EndX=202.765 EndY=20.303 EndZ=0
    g5: LineSegment StartX=215.42 StartY=-53.0314 StartZ=0 EndX=192.176 EndY=-3.18451 EndZ=0
    g6: ArcOfCircle CenterX=184.801 CenterY=-67.3089 CenterZ=0 NormalX=0 NormalY=0 NormalZ=1 AngleXU=0 Radius=33.7833 StartAngle=5.88425 EndAngle=6.71952
    g7: ArcOfCircle CenterX=207.583 CenterY=4 CenterZ=0 NormalX=0 NormalY=0 NormalZ=1 AngleXU=0 Radius=17 StartAngle=1.85815 EndAngle=3.57792
  constraints (19):
    c: Coincident(g0,g-4)
    c: PointOnObject(g0,g-3)
    c: Horizontal(g0,g-7)
    c: Coincident(g1,g0)
    c: Coincident(g1,g-5)
    c: Diameter(g2) = 6
    c: Diameter(g3) = 6
    c: Coincident(g2,g-9)
    c: Coincident(g3,g-10)
    c: Coincident(g4,g0)
    c: Coincident(g5,g-6)
    c: Coincident(g6,g1)
    c: Coincident(g6,g5)
    c: Equal(g-5,g6)
    c: Coincident(g5,g-7)
    c: Coincident(g4,g-7)
    c: Tangent(g7,g-7)
    c: Coincident(g7,g4)
    c: Coincident(g7,g5)
FEATURE [PartDesign::Pad] Pad008  label="Pad008 - forma impugnatura"
  BaseFeature = -> Pad007
  Direction = (0,1,-2e-16)
  Length = 1.6
  Length2 = 10
  Profile = -> Sketch096
  ReferenceAxis = -> Sketch096 [N_Axis]
  Refine = true
  Suppressed = false
  Type = 0
FEATURE [Sketcher::SketchObject] Sketch097
  ArcFitTolerance = 1e-06
  AttachmentSupport = -> [Pad004]
  ExternalGeometry = -> [Binder]
  FullyConstrained = true
  MakeInternals = false
  MapMode = 5
  Placement = pos=(0,2,0) rot=(0,0.707107,0.707107;3.14159rad)
  sketch-geometry (4):
    g0: LineSegment StartX=90 StartY=36.8 StartZ=0 EndX=108 EndY=36.8 EndZ=0
    g1: LineSegment StartX=108 StartY=36.8 StartZ=0 EndX=108 EndY=26.8 EndZ=0
    g2: LineSegment StartX=108 StartY=26.8 StartZ=0 EndX=90 EndY=26.8 EndZ=0
    g3: ArcOfCircle CenterX=94 CenterY=31.8 CenterZ=0 NormalX=0 NormalY=0 NormalZ=1 AngleXU=0 Radius=6.40312 StartAngle=2.24554 EndAngle=4.03765
  constraints (13):
    c: Horizontal(g0)
    c: Coincident(g1,g0)
    c: Vertical(g1)
    c: DistanceX(g0,g0) = 18
    c: DistanceY(g1,g1) = 10
    c: Coincident(g2,g1)
    c: Horizontal(g2)
    c: Equal(g2,g0)
    c: DistanceY(g0,g-3) = 2.4
    c: Coincident(g3,g0)
    c: Coincident(g3,g2)
    c: DistanceX(g2,g3) = 4
    c: DistanceX(g-3,g0) = 90
FEATURE [PartDesign::Pad] Pad009
  BaseFeature = -> Pad008
  Direction = (0,1,-2e-16)
  Length = 1.6
  Length2 = 10
  Profile = -> Sketch097
  ReferenceAxis = -> Sketch097 [N_Axis]
  Refine = true
  Suppressed = false
  Type = 0
FEATURE [Sketcher::SketchObject] Sketch098
  ArcFitTolerance = 1e-06
  AttachmentSupport = -> [Pad006]
  ExternalGeometry = -> [Binder]
  FullyConstrained = true
  MakeInternals = false
  MapMode = 5
  Placement = pos=(0,2.8,-7e-16) rot=(0,0.707107,0.707107;3.14159rad)
  sketch-geometry (4):
    g0: LineSegment StartX=118 StartY=39.2 StartZ=0 EndX=129 EndY=39.2 EndZ=0
    g1: LineSegment StartX=120.599 StartY=31.2 StartZ=0 EndX=131.599 EndY=31.2 EndZ=0
    g2: LineSegment StartX=129 StartY=39.2 StartZ=0 EndX=131.599 EndY=31.2 EndZ=0
    g3: LineSegment StartX=118 StartY=39.2 StartZ=0 EndX=120.599 EndY=31.2 EndZ=0
  constraints (12):
    c: PointOnObject(g0,g-3)
    c: PointOnObject(g0,g-3)
    c: DistanceX(g0,g0) = 11
    c: Horizontal(g1)
    c: Equal(g1,g0)
    c: Coincident(g2,g0)
    c: Coincident(g3,g0)
    c: Parallel(g-4,g2)
    c: Coincident(g1,g2)
    c: Coincident(g1,g3)
    c: DistanceY(g1,g0) = 8
    c: DistanceX(g-3,g0) = 118
FEATURE [PartDesign::Pad] Pad010
  BaseFeature = -> Pad009
  Direction = (0,1,-2e-16)
  Length = 1.2
  Length2 = 10
  Profile = -> Sketch098
  ReferenceAxis = -> Sketch098 [N_Axis]
  Refine = true
  Suppressed = false
  Type = 0
FEATURE [Sketcher::SketchObject] Sketch099
  ArcFitTolerance = 1e-06
  AttachmentSupport = -> [Pad008]
  ExternalGeometry = -> [Binder]
  FullyConstrained = true
  MakeInternals = false
  MapMode = 5
  Placement = pos=(0,3.6,0) rot=(0,0.707107,0.707107;3.14159rad)
  sketch-geometry (13):
    g0: LineSegment StartX=192.176 StartY=-3.18451 StartZ=0 EndX=196.804 EndY=-13.1108 EndZ=0
    g1: LineSegment [constr] StartX=202.765 StartY=20.303 StartZ=0 EndX=181.223 EndY=20.303 EndZ=0
    g2: LineSegment [constr] StartX=181.223 StartY=20.303 StartZ=0 EndX=181.223 EndY=-3.18451 EndZ=0
    g3: ArcOfCircle CenterX=181.223 CenterY=-20.3764 CenterZ=0 NormalX=0 NormalY=0 NormalZ=1 AngleXU=0 Radius=17.1918 StartAngle=0.436332 EndAngle=1.57079
    g4: ArcOfEllipse CenterX=181.223 CenterY=8.55923 CenterZ=0 NormalX=0 NormalY=0 NormalZ=1 MajorRadius=23.4779 MinorRadius=11.7437 AngleXU=0 StartAngle=1.5708 EndAngle=4.71239
    g5: LineSegment [constr] StartX=204.701 StartY=8.55923 StartZ=0 EndX=157.745 EndY=8.55923 EndZ=0
    g6: LineSegment [constr] StartX=181.223 StartY=20.303 StartZ=0 EndX=181.223 EndY=-3.18451 EndZ=0
    g7: GeomPoint [constr] X=201.553 Y=8.55923 Z=0
    g8: GeomPoint [constr] X=160.894 Y=8.55923 Z=0
    g9: GeomPoint [constr] X=181.223 Y=-3.18451 Z=0
    g10: LineSegment StartX=181.223 StartY=20.303 StartZ=0 EndX=202.765 EndY=20.303 EndZ=0
    g11: ArcOfCircle CenterX=207.583 CenterY=4 CenterZ=0 NormalX=0 NormalY=0 NormalZ=1 AngleXU=0 Radius=17 StartAngle=1.85815 EndAngle=3.57792
    g12: LineSegment [constr] StartX=172.411 StartY=39.2 StartZ=0 EndX=192.176 EndY=-3.18451 EndZ=0
  constraints (27):
    c: Coincident(g1,g-7)
    c: Horizontal(g1)
    c: Coincident(g2,g1)
    c: Vertical(g2)
    c: Horizontal(g2,g0)
    c: Coincident(g3,g0)
    c: Coincident(g3,g2)
    c: InternalAlignment(g5-g8 -> g4) x4
    c: Horizontal(g5)
    c: PointOnObject(g4,g2)
    c: Coincident(g4,g1)
    c: DistanceX(g-3,g5) = 10.1
    c: Coincident(g4,g2)
    c: Tangent(g3,g-5)
    c: PointOnObject(g9,g4)
    c: PointOnObject(g9,g3)
    c: Tangent(g4,g3,g9) = 1.5708
    c: Coincident(g10,g1)
    c: Coincident(g10,g1)
    c: Equal(g11,g-4)
    c: Coincident(g11,g1)
    c: Coincident(g11,g0)
    c: PointOnObject(g12,g-6)
    c: PointOnObject(g1,g12)
    c: Tangent(g12,g-5) = -1.5708
    c: Tangent(g0,g-5) = -1.5708
    c: Horizontal(g9,g12)
FEATURE [Sketcher::SketchObject] Sketch106  label="Sketch106 - smusso impuniatura interno"
  ArcFitTolerance = 1e-06
  AttachmentSupport = -> [Pad008]
  ExternalGeometry = -> [Pad008]
  FullyConstrained = true
  MakeInternals = false
  MapMode = 5
  Placement = pos=(0,0,-80.4316) rot=(1,0,0;3.14159rad)
  sketch-geometry (9):
    g0: LineSegment StartX=-176.685 StartY=-3.6 StartZ=0 EndX=-176.685 EndY=1.168e-12 EndZ=0
    g1: LineSegment [constr] StartX=-176.685 StartY=1.79e-14 StartZ=0 EndX=-176.685 EndY=1.1682e-12 EndZ=0
    g2: LineSegment [constr] StartX=-186.685 StartY=-3.6 StartZ=0 EndX=-186.685 EndY=1.168e-12 EndZ=0
    g3: ArcOfEllipse CenterX=-186.685 CenterY=1.1682e-12 CenterZ=0 NormalX=0 NormalY=0 NormalZ=1 MajorRadius=10 MinorRadius=3.6 AngleXU=-3.14159 StartAngle=1.5708 EndAngle=3.14159
    g4: LineSegment [constr] StartX=-196.685 StartY=1.79e-14 StartZ=0 EndX=-176.685 EndY=1.79e-14 EndZ=0
    g5: LineSegment [constr] StartX=-186.685 StartY=-3.6 StartZ=0 EndX=-186.685 EndY=3.6 EndZ=0
    g6: GeomPoint [constr] X=-196.015 Y=1.6e-14 Z=0
    g7: GeomPoint [constr] X=-177.356 Y=1.85e-14 Z=0
    g8: LineSegment StartX=-176.685 StartY=-3.6 StartZ=0 EndX=-186.685 EndY=-3.6 EndZ=0
  constraints (15):
    c: PointOnObject(g2,g-3)
    c: Coincident(g1,g-5)
    c: DistanceY(g1,g1) = 0
    c: Coincident(g0,g1)
    c: DistanceX(g2,g-5) = 10
    c: Vertical(g2)
    c: Horizontal(g2,g0)
    c: InternalAlignment(g4-g7 -> g3) x4
    c: Coincident(g3,g2)
    c: Horizontal(g4)
    c: Coincident(g3,g0)
    c: Tangent(g0,g-5) = 1.5708
    c: Coincident(g3,g2)
    c: Coincident(g8,g0)
    c: Coincident(g8,g2)
FEATURE [Sketcher::SketchObject] Sketch107  label="Sketch107 - smusso impugnatura esterno"
  ArcFitTolerance = 1e-06
  AttachmentSupport = -> [Pad008]
  ExternalGeometry = -> [Pad008]
  FullyConstrained = true
  MakeInternals = false
  MapMode = 5
  Placement = pos=(0,0,-80.4316) rot=(1,0,0;3.14159rad)
  sketch-geometry (9):
    g0: LineSegment [constr] StartX=-215.932 StartY=1.79e-14 StartZ=0 EndX=-215.932 EndY=1.94e-14 EndZ=0
    g1: LineSegment StartX=-215.932 StartY=-3.6 StartZ=0 EndX=-215.932 EndY=1.95e-14 EndZ=0
    g2: LineSegment StartX=-215.932 StartY=-3.6 StartZ=0 EndX=-205.932 EndY=-3.6 EndZ=0
    g3: LineSegment [constr] StartX=-205.932 StartY=-3.6 StartZ=0 EndX=-205.932 EndY=1.95e-14 EndZ=0
    g4: ArcOfEllipse CenterX=-205.932 CenterY=1.94e-14 CenterZ=0 NormalX=0 NormalY=0 NormalZ=1 MajorRadius=10 MinorRadius=3.6 AngleXU=3.14159 StartAngle=1e-16 EndAngle=1.5708
    g5: LineSegment [constr] StartX=-215.932 StartY=1.79e-14 StartZ=0 EndX=-195.932 EndY=1.79e-14 EndZ=0
    g6: LineSegment [constr] StartX=-205.932 StartY=-3.6 StartZ=0 EndX=-205.932 EndY=3.6 EndZ=0
    g7: GeomPoint [constr] X=-215.262 Y=1.97e-14 Z=0
    g8: GeomPoint [constr] X=-196.602 Y=1.78e-14 Z=0
  constraints (16):
    c: Coincident(g0,g-6)
    c: PointOnObject(g0,g-6)
    c: DistanceY(g0,g0) = 0
    c: Coincident(g1,g-6)
    c: Coincident(g1,g0)
    c: Tangent(g2,g-3)
    c: DistanceX(g2,g2) = 10
    c: Coincident(g3,g2)
    c: Vertical(g3)
    c: Horizontal(g3,g0)
    c: InternalAlignment(g5-g8 -> g4) x4
    c: Coincident(g4,g3)
    c: Horizontal(g5)
    c: Coincident(g4,g0)
    c: Coincident(g4,g2)
    c: PointOnObject(g2,g1)
FEATURE [PartDesign::SubtractivePipe] SubtractivePipe
  AuxilleryCurvelinear = true
  AuxillerySpineTangent = false
  BaseFeature = -> Pad010
  Binormal = (0,0,0)
  Mode = 0
  Profile = -> Sketch106
  Refine = true
  Spine = -> Pad008 [Edge208]
  SpineTangent = false
  Suppressed = false
  Transformation = 0
  Transition = 0
FEATURE [PartDesign::SubtractivePipe] SubtractivePipe001
  AuxilleryCurvelinear = true
  AuxillerySpineTangent = false
  BaseFeature = -> SubtractivePipe
  Binormal = (0,0,0)
  Mode = 0
  Profile = -> Sketch107
  Refine = true
  Spine = -> Pad008 [Edge206,Edge209,Edge197]
  SpineTangent = false
  Suppressed = false
  Transformation = 0
  Transition = 0
FEATURE [Sketcher::SketchObject] Sketch108
  ArcFitTolerance = 1e-06
  AttachmentOffset = pos=(0,0,-1.6) rot=(0,0,1;0rad)
  AttachmentSupport = -> [Pad008]
  ExternalGeometry = -> [Binder]
  FullyConstrained = true
  MakeInternals = false
  MapMode = 5
  Placement = pos=(0,2,4e-16) rot=(0,0.707107,0.707107;3.14159rad)
  sketch-geometry (14):
    g0: LineSegment StartX=192.176 StartY=-3.18451 StartZ=0 EndX=193.827 EndY=-6.72678 EndZ=0
    g1: LineSegment [constr] StartX=202.765 StartY=20.303 StartZ=0 EndX=181.223 EndY=20.303 EndZ=0
    g2: LineSegment [constr] StartX=181.223 StartY=20.303 StartZ=0 EndX=181.223 EndY=1.30297 EndZ=0
    g3: ArcOfCircle CenterX=181.223 CenterY=-12.6042 CenterZ=0 NormalX=0 NormalY=0 NormalZ=1 AngleXU=0 Radius=13.9072 StartAngle=0.436332 EndAngle=1.5708
    g4: ArcOfEllipse CenterX=181.223 CenterY=10.803 CenterZ=0 NormalX=0 NormalY=0 NormalZ=1 MajorRadius=14.4779 MinorRadius=9.5 AngleXU=0 StartAngle=1.5708 EndAngle=4.71239
    g5: LineSegment [constr] StartX=195.701 StartY=10.803 StartZ=0 EndX=166.745 EndY=10.803 EndZ=0
    g6: LineSegment [constr] StartX=181.223 StartY=20.303 StartZ=0 EndX=181.223 EndY=1.30297 EndZ=0
    g7: GeomPoint [constr] X=192.148 Y=10.803 Z=0
    g8: GeomPoint [constr] X=170.298 Y=10.803 Z=0
    g9: LineSegment StartX=181.223 StartY=20.303 StartZ=0 EndX=202.765 EndY=20.303 EndZ=0
    g10: ArcOfCircle CenterX=207.583 CenterY=4 CenterZ=0 NormalX=0 NormalY=0 NormalZ=1 AngleXU=0 Radius=17 StartAngle=1.85815 EndAngle=3.57792
    g11: LineSegment [constr] StartX=172.411 StartY=39.2 StartZ=0 EndX=192.176 EndY=-3.18451 EndZ=0
    g12: GeomPoint [constr] X=181.223 Y=1.30297 Z=0
    g13: GeomPoint [constr] X=181.223 Y=1.30297 Z=0
  constraints (28):
    c: Coincident(g1,g-7)
    c: Horizontal(g1)
    c: Coincident(g2,g1)
    c: Vertical(g2)
    c: Coincident(g3,g2)
    c: InternalAlignment(g5-g8 -> g4) x4
    c: Horizontal(g5)
    c: PointOnObject(g4,g2)
    c: Coincident(g4,g1)
    c: DistanceX(g-3,g5) = 19.1
    c: Coincident(g4,g2)
    c: Coincident(g9,g1)
    c: Coincident(g9,g1)
    c: Coincident(g10,g1)
    c: Coincident(g10,g0)
    c: PointOnObject(g11,g-6)
    c: PointOnObject(g1,g11)
    c: DistanceY(g2,g1) = 19
    c: Coincident(g10,g-4)
    c: PointOnObject(g12,g4)
    c: PointOnObject(g12,g3)
    c: Tangent(g11,g-5) = -1.5708
    c: Tangent(g0,g-5) = -1.5708
    c: Tangent(g3,g0) = 1.5708
    c: PointOnObject(g13,g4)
    c: PointOnObject(g13,g3)
    c: Tangent(g4,g3,g13) = 1.5708
    c: Horizontal(g11,g0)
FEATURE [Part::Part2DObjectPython] Clone2D  label="Sketch108 (2D)"  # Draft 2D object (typed FeaturePython)
  Fuse = false
  Objects = -> [Sketch108]
  Placement = pos=(0,2,4e-16) rot=(0,0.707107,0.707107;3.14159rad)
  Scale = (1,1,1)
FEATURE [Sketcher::SketchObject] Sketch109
  ArcFitTolerance = 1e-06
  AttachmentOffset = pos=(0,0,-3.6) rot=(0,0,1;0rad)
  AttachmentSupport = -> [Pad008]
  ExternalGeometry = -> [Binder]
  FullyConstrained = true
  MakeInternals = false
  MapMode = 5
  Placement = pos=(0,-5.8e-15,8e-16) rot=(0,0.707107,0.707107;3.14159rad)
  sketch-geometry (1):
    g0: GeomPoint X=197.47 Y=8.55923 Z=0
  constraints (1):
    c: Symmetric(g-7,g-5,g0)
FEATURE [PartDesign::SubtractiveLoft] SubtractiveLoft
  BaseFeature = -> SubtractivePipe001
  Closed = false
  Profile = -> Sketch099
  Refine = true
  Ruled = false
  Sections = -> [Sketch108]
  Suppressed = false
FEATURE [PartDesign::SubtractiveLoft] SubtractiveLoft001
  BaseFeature = -> SubtractiveLoft
  Closed = false
  Profile = -> Clone2D
  Refine = true
  Ruled = false
  Sections = -> [Sketch109]
  Suppressed = false
FEATURE [PartDesign::Chamfer] Chamfer001
  Angle = 45
  Base = -> SubtractiveLoft001 [Edge122,Edge121,Edge118,Edge116,Edge114,Edge113,Edge170,Edge80,Edge76]
  BaseFeature = -> SubtractiveLoft001
  ChamferType = 0
  FlipDirection = false
  Refine = true
  Size = 1.9
  Size2 = 1
  SupportTransform = false
  Suppressed = false
  UseAllEdges = false
FEATURE [PartDesign::Chamfer] Chamfer002
  Angle = 45
  Base = -> Chamfer001 [Edge95,Edge34]
  BaseFeature = -> Chamfer001
  ChamferType = 0
  FlipDirection = false
  Refine = true
  Size = 3.5
  Size2 = 1
  SupportTransform = false
  Suppressed = false
  UseAllEdges = false
FEATURE [PartDesign::Chamfer] Chamfer003
  Angle = 45
  Base = -> Chamfer002 [Edge85]
  BaseFeature = -> Chamfer002
  ChamferType = 0
  FlipDirection = false
  Refine = true
  Size = 1.5
  Size2 = 1
  SupportTransform = false
  Suppressed = false
  UseAllEdges = false
FEATURE [PartDesign::Chamfer] Chamfer004
  Angle = 45
  Base = -> Chamfer003 [Edge18,Edge19,Edge17,Edge20]
  BaseFeature = -> Chamfer003
  ChamferType = 0
  FlipDirection = false
  Refine = true
  Size = 1.5
  Size2 = 1
  SupportTransform = false
  Suppressed = false
  UseAllEdges = false
FEATURE [PartDesign::Chamfer] Chamfer005
  Angle = 45
  Base = -> Chamfer004 [Edge227,Edge224]
  BaseFeature = -> Chamfer004
  ChamferType = 1
  FlipDirection = false
  Refine = true
  Size = 1.5
  Size2 = 2.8
  SupportTransform = false
  Suppressed = false
  UseAllEdges = false
FEATURE [PartDesign::Chamfer] Chamfer006
  Angle = 45
  Base = -> Chamfer005 [Edge223]
  BaseFeature = -> Chamfer005
  ChamferType = 1
  FlipDirection = false
  Refine = true
  Size = 6
  Size2 = 1
  SupportTransform = false
  Suppressed = false
  UseAllEdges = false
FEATURE [PartDesign::Fillet] Fillet002
  Base = -> Chamfer006 [Edge150]
  BaseFeature = -> Chamfer006
  Radius = 1.9
  Refine = true
  SupportTransform = false
  Suppressed = false
  UseAllEdges = false
FEATURE [PartDesign::Fillet] Fillet003
  Base = -> Fillet002 [Edge6]
  BaseFeature = -> Fillet002
  Radius = 1.1
  Refine = true
  SupportTransform = false
  Suppressed = false
  UseAllEdges = false
FEATURE [PartDesign::Fillet] Fillet004
  Base = -> Fillet003 [Edge45]
  BaseFeature = -> Fillet003
  Radius = 1.9
  Refine = true
  SupportTransform = false
  Suppressed = false
  UseAllEdges = false
FEATURE [PartDesign::Fillet] Fillet005
  Base = -> Fillet004 [Edge1]
  BaseFeature = -> Fillet004
  Radius = 1
  Refine = true
  SupportTransform = false
  Suppressed = false
  UseAllEdges = false
FEATURE [PartDesign::Chamfer] Chamfer007
  Angle = 45
  Base = -> Fillet005 [Edge29]
  BaseFeature = -> Fillet005
  ChamferType = 0
  FlipDirection = false
  Refine = true
  Size = 1.9
  Size2 = 1
  SupportTransform = false
  Suppressed = false
  UseAllEdges = false
FEATURE [PartDesign::Fillet] Fillet006
  Base = -> Chamfer007 [Edge339,Edge338]
  BaseFeature = -> Chamfer007
  Radius = 5
  Refine = true
  SupportTransform = false
  Suppressed = false
  UseAllEdges = false
FEATURE [Sketcher::SketchObject] Sketch110
  ArcFitTolerance = 1e-06
  AttachmentSupport = -> [Pad010]
  ExternalGeometry = -> [Sketch098]
  FullyConstrained = true
  MakeInternals = false
  MapMode = 5
  Placement = pos=(0,4,-9e-16) rot=(0,0.707107,0.707107;3.14159rad)
  sketch-geometry (8):
    g0: LineSegment StartX=119.69 StartY=34 StartZ=0 EndX=130.69 EndY=34 EndZ=0
    g1: LineSegment StartX=119.95 StartY=33.2 StartZ=0 EndX=130.95 EndY=33.2 EndZ=0
    g2: LineSegment StartX=119.137 StartY=35.7 StartZ=0 EndX=130.137 EndY=35.7 EndZ=0
    g3: LineSegment StartX=118.877 StartY=36.5 StartZ=0 EndX=129.877 EndY=36.5 EndZ=0
    g4: LineSegment StartX=118.877 StartY=36.5 StartZ=0 EndX=119.137 EndY=35.7 EndZ=0
    g5: LineSegment StartX=129.877 StartY=36.5 StartZ=0 EndX=130.137 EndY=35.7 EndZ=0
    g6: LineSegment StartX=119.69 StartY=34 StartZ=0 EndX=119.95 EndY=33.2 EndZ=0
    g7: LineSegment StartX=130.69 StartY=34 StartZ=0 EndX=130.95 EndY=33.2 EndZ=0
  constraints (24):
    c: Horizontal(g0)
    c: Horizontal(g1)
    c: Horizontal(g2)
    c: Horizontal(g3)
    c: Equal(g1,g-5)
    c: Equal(g0,g-5)
    c: Equal(g2,g-5)
    c: Equal(g3,g-5)
    c: PointOnObject(g0,g-3)
    c: PointOnObject(g1,g-3)
    c: PointOnObject(g2,g-3)
    c: PointOnObject(g3,g-3)
    c: Coincident(g4,g3)
    c: Coincident(g4,g2)
    c: Coincident(g5,g3)
    c: Coincident(g5,g2)
    c: Coincident(g6,g0)
    c: Coincident(g6,g1)
    c: Coincident(g7,g0)
    c: Coincident(g7,g1)
    c: DistanceY(g1,g0) = 0.8
    c: DistanceY(g2,g3) = 0.8
    c: DistanceY(g-5,g1) = 2
    c: DistanceY(g-5,g2) = 4.5
FEATURE [PartDesign::Pocket] Pocket003
  BaseFeature = -> Fillet006
  Direction = (0,-1,2e-16)
  Length = 1
  Length2 = 5
  Profile = -> Sketch110
  ReferenceAxis = -> Sketch110 [N_Axis]
  Refine = true
  Suppressed = false
  Type = 0
FEATURE [Sketcher::SketchObject] Sketch111
  ArcFitTolerance = 1e-06
  AttachmentSupport = -> [Pad009]
  ExternalGeometry = -> [Pad009]
  FullyConstrained = true
  MakeInternals = false
  MapMode = 5
  Placement = pos=(0,3.6,-8e-16) rot=(0,0.707107,0.707107;3.14159rad)
  sketch-geometry (21):
    g0: LineSegment [constr] StartX=97 StartY=36.8 StartZ=0 EndX=97 EndY=26.8 EndZ=0
    g1: LineSegment StartX=97 StartY=28.6 StartZ=0 EndX=97 EndY=27.8 EndZ=0
    g2: LineSegment StartX=97 StartY=27.8 StartZ=0 EndX=108 EndY=27.8 EndZ=0
    g3: LineSegment StartX=108 StartY=27.8 StartZ=0 EndX=108 EndY=28.6 EndZ=0
    g4: LineSegment StartX=108 StartY=28.6 StartZ=0 EndX=97 EndY=28.6 EndZ=0
    g5: LineSegment StartX=97 StartY=35.8 StartZ=0 EndX=97 EndY=35 EndZ=0
    g6: LineSegment StartX=97 StartY=35 StartZ=0 EndX=108 EndY=35 EndZ=0
    g7: LineSegment StartX=108 StartY=35 StartZ=0 EndX=108 EndY=35.8 EndZ=0
    g8: LineSegment StartX=108 StartY=35.8 StartZ=0 EndX=97 EndY=35.8 EndZ=0
    g9: LineSegment StartX=97 StartY=30.4 StartZ=0 EndX=97 EndY=29.6 EndZ=0
    g10: LineSegment StartX=97 StartY=29.6 StartZ=0 EndX=108 EndY=29.6 EndZ=0
    g11: LineSegment StartX=108 StartY=29.6 StartZ=0 EndX=108 EndY=30.4 EndZ=0
    g12: LineSegment StartX=108 StartY=30.4 StartZ=0 EndX=97 EndY=30.4 EndZ=0
    g13: LineSegment StartX=97 StartY=34 StartZ=0 EndX=97 EndY=33.2 EndZ=0
    g14: LineSegment StartX=97 StartY=33.2 StartZ=0 EndX=108 EndY=33.2 EndZ=0
    g15: LineSegment StartX=108 StartY=33.2 StartZ=0 EndX=108 EndY=34 EndZ=0
    g16: LineSegment StartX=108 StartY=34 StartZ=0 EndX=97 EndY=34 EndZ=0
    g17: LineSegment StartX=97 StartY=32.2 StartZ=0 EndX=97 EndY=31.4 EndZ=0
    g18: LineSegment StartX=97 StartY=31.4 StartZ=0 EndX=108 EndY=31.4 EndZ=0
    g19: LineSegment StartX=108 StartY=31.4 StartZ=0 EndX=108 EndY=32.2 EndZ=0
    g20: LineSegment StartX=108 StartY=32.2 StartZ=0 EndX=97 EndY=32.2 EndZ=0
  constraints (54):
    c: Vertical(g0)
    c: PointOnObject(g0,g-3)
    c: PointOnObject(g0,g-4)
    c: DistanceX(g0,g-5) = 11
    c: Coincident(g1,g2)
    c: Coincident(g2,g3)
    c: Coincident(g3,g4)
    c: Coincident(g4,g1)
    c: Horizontal(g2)
    c: Horizontal(g4)
    c: Tangent(g1,g0)
    c: Tangent(g3,g-5)
    c: DistanceY(g2,g3) = 0.8
    c: Coincident(g5,g6)
    c: Coincident(g6,g7)
    c: Coincident(g7,g8)
    c: Coincident(g8,g5)
    c: Horizontal(g6)
    c: Horizontal(g8)
    c: DistanceY(g6,g7) = 0.8
    c: Coincident(g9,g10)
    c: Coincident(g10,g11)
    c: Coincident(g11,g12)
    c: Coincident(g12,g9)
    c: Horizontal(g10)
    c: Horizontal(g12)
    c: DistanceY(g10,g11) = 0.8
    c: Tangent(g5,g0)
    c: Tangent(g7,g-5)
    c: Tangent(g9,g0)
    c: Tangent(g11,g-5)
    c: Coincident(g13,g14)
    c: Coincident(g14,g15)
    c: Coincident(g15,g16)
    c: Coincident(g16,g13)
    c: Horizontal(g14)
    c: Horizontal(g16)
    c: DistanceY(g14,g15) = 0.8
    c: Tangent(g13,g0)
    c: Tangent(g15,g-5)
    c: Coincident(g17,g18)
    c: Coincident(g18,g19)
    c: Coincident(g19,g20)
    c: Coincident(g20,g17)
    c: Horizontal(g18)
    c: Horizontal(g20)
    c: DistanceY(g18,g19) = 0.8
    c: Tangent(g17,g0)
    c: Tangent(g19,g-5)
    c: DistanceY(g1,g9) = 1
    c: DistanceY(g9,g17) = 1
    c: DistanceY(g17,g13) = 1
    c: DistanceY(g13,g5) = 1
    c: DistanceY(g0,g1) = 1
FEATURE [PartDesign::Pocket] Pocket004
  BaseFeature = -> Pocket003
  Direction = (0,-1,2e-16)
  Length = 1
  Length2 = 5
  Profile = -> Sketch111
  ReferenceAxis = -> Sketch111 [N_Axis]
  Refine = true
  Suppressed = false
  Type = 0
FEATURE [Sketcher::SketchObject] Sketch112
  ArcFitTolerance = 1e-06
  AttachmentSupport = -> [Pad008]
  ExternalGeometry = -> [Binder]
  FullyConstrained = true
  MakeInternals = false
  MapMode = 5
  Placement = pos=(0,3.6,0) rot=(0,0.707107,0.707107;3.14159rad)
  sketch-geometry (4):
    g0: LineSegment [constr] StartX=167.782 StartY=-53.0314 StartZ=0 EndX=215.42 EndY=-53.0314 EndZ=0
    g1: GeomPoint [constr] X=191.282 Y=-53.0314 Z=0
    g2: Circle CenterX=191.282 CenterY=-53.0314 CenterZ=0 NormalX=0 NormalY=0 NormalZ=1 AngleXU=0 Radius=11.5
    g3: Circle CenterX=191.282 CenterY=-53.0314 CenterZ=0 NormalX=0 NormalY=0 NormalZ=1 AngleXU=0 Radius=10.7
  constraints (9):
    c: Horizontal(g0)
    c: PointOnObject(g0,g-3)
    c: Diameter(g2) = 23
    c: Coincident(g2,g1)
    c: Diameter(g3) = 21.4
    c: Coincident(g3,g1)
    c: DistanceX(g0,g1) = 23.5
    c: PointOnObject(g1,g0)
    c: Coincident(g0,g-4)
FEATURE [PartDesign::Pocket] Pocket005
  BaseFeature = -> Pocket004
  Direction = (0,-1,2e-16)
  Length = 0.8
  Length2 = 5
  Profile = -> Sketch112
  ReferenceAxis = -> Sketch112 [N_Axis]
  Refine = true
  Suppressed = false
  Type = 0
FEATURE [Part::Mirroring] Part__Mirroring  label="Pocket005 (Mirror #1)"
  Base = (0,0,0)
  Normal = (0,0,1)
  Source = -> Pocket005
FEATURE [Sketcher::SketchObject] Sketch113
  ArcFitTolerance = 1e-06
  AttachmentSupport = -> [Pocket005]
  FullyConstrained = true
  MakeInternals = false
  MapMode = 5
  Placement = pos=(0,3.6,0) rot=(0,0.707107,0.707107;3.14159rad)
FEATURE [PartDesign::Body] Body006  label="lato SX"
  AllowCompound = false
  Group = -> [Binder,Pad004,Sketch091,Pad005,Sketch092,Pocket001,Sketch093,Pocket002,Sketch094,Pad006,Sketch095,Pad007,Sketch096,Pad008,Sketch097,Pad009,Sketch098,Pad010,SubtractivePipe,SubtractivePipe001,Sketch099,Sketch106,Sketch107,Sketch108,Clone2D,Sketch109,SubtractiveLoft,SubtractiveLoft001,Chamfer001,Chamfer002,Chamfer003,Chamfer004,Chamfer005,Chamfer006,Fillet002,Fillet003,Fillet004,Fillet005,+9 more]
  Origin = -> Origin006
  Tip = -> Pocket005
FEATURE [Mesh::Feature] logo_per_PCB_definitivo_positivo
  Placement = pos=(-191,17,-66) rot=(0,1,1;0rad)
FEATURE [Sketcher::SketchObject] Sketch114  label="Sketch114 - base lato DX"
  ArcFitTolerance = 1e-06
  AttachmentSupport = -> [Binder001]
  ExternalGeometry = -> [Binder001]
  FullyConstrained = true
  MakeInternals = false
  MapMode = 5
  Placement = pos=(0,1e-15,0) rot=(0,0.707107,0.707107;3.14159rad)
  sketch-geometry (30):
    g0: Circle CenterX=5.6 CenterY=34.8 CenterZ=0 NormalX=0 NormalY=0 NormalZ=1 AngleXU=0 Radius=1.8
    g1: Circle CenterX=5.6 CenterY=7.6 CenterZ=0 NormalX=0 NormalY=0 NormalZ=1 AngleXU=0 Radius=1.8
    g2: Circle CenterX=24.2 CenterY=26.7 CenterZ=0 NormalX=0 NormalY=0 NormalZ=1 AngleXU=0 Radius=3
    g3: Circle CenterX=24.2 CenterY=15.7 CenterZ=0 NormalX=0 NormalY=0 NormalZ=1 AngleXU=0 Radius=3
    g4: Circle CenterX=36.2 CenterY=21.2 CenterZ=0 NormalX=0 NormalY=0 NormalZ=1 AngleXU=0 Radius=2.8
    g5: Circle CenterX=78.51 CenterY=34.8 CenterZ=0 NormalX=0 NormalY=0 NormalZ=1 AngleXU=0 Radius=1.8
    g6: Circle CenterX=78.51 CenterY=7.6 CenterZ=0 NormalX=0 NormalY=0 NormalZ=1 AngleXU=0 Radius=1.8
    g7: Circle CenterX=184.08 CenterY=34.8 CenterZ=0 NormalX=0 NormalY=0 NormalZ=1 AngleXU=0 Radius=1.8
    g8: Circle CenterX=213.443 CenterY=-76.8316 CenterZ=0 NormalX=0 NormalY=0 NormalZ=1 AngleXU=0 Radius=1.8
    g9: Circle CenterX=179.305 CenterY=-76.8316 CenterZ=0 NormalX=0 NormalY=0 NormalZ=1 AngleXU=0 Radius=1.8
    g10: ArcOfCircle [constr] CenterX=132.428 CenterY=4 CenterZ=0 NormalX=0 NormalY=0 NormalZ=1 AngleXU=0 Radius=16 StartAngle=0.314159 EndAngle=1.5708
    g11: ArcOfCircle CenterX=107.6 CenterY=4 CenterZ=0 NormalX=0 NormalY=0 NormalZ=1 AngleXU=0 Radius=16 StartAngle=1.5708 EndAngle=3.00366
    g12: ArcOfCircle CenterX=207.583 CenterY=4 CenterZ=0 NormalX=0 NormalY=0 NormalZ=1 AngleXU=0 Radius=17 StartAngle=1.85815 EndAngle=3.57792
    g13: ArcOfCircle CenterX=184.801 CenterY=-67.3089 CenterZ=0 NormalX=0 NormalY=0 NormalZ=1 AngleXU=0 Radius=33.7833 StartAngle=5.88425 EndAngle=6.71952
    g14: LineSegment StartX=0 StartY=39.2 StartZ=0 EndX=0 EndY=3.2 EndZ=0
    g15: LineSegment StartX=0 StartY=3.2 StartZ=0 EndX=82.8 EndY=3.2 EndZ=0
    g16: LineSegment StartX=82.8 StartY=3.2 StartZ=0 EndX=82.8 EndY=6.2 EndZ=0
    g17: LineSegment StartX=82.8 StartY=6.2 StartZ=0 EndX=91.752 EndY=6.2 EndZ=0
    g18: LineSegment StartX=107.6 StartY=20 StartZ=0 EndX=132.428 EndY=20 EndZ=0
    g19: LineSegment StartX=147.645 StartY=8.94427 StartZ=0 EndX=176.685 EndY=-80.4316 EndZ=0
    g20: LineSegment StartX=176.685 StartY=-80.4316 StartZ=0 EndX=215.932 EndY=-80.4316 EndZ=0
    g21: LineSegment StartX=215.42 StartY=-53.0314 StartZ=0 EndX=192.176 EndY=-3.18451 EndZ=0
    g22: LineSegment StartX=202.765 StartY=20.303 StartZ=0 EndX=195.887 EndY=39.2 EndZ=0
    g23: LineSegment StartX=195.887 StartY=39.2 StartZ=0 EndX=0 EndY=39.2 EndZ=0
    g24: LineSegment StartX=196.467 StartY=26.4942 StartZ=0 EndX=194.073 EndY=33.0721 EndZ=0
    g25: LineSegment StartX=194.073 StartY=33.0721 StartZ=0 EndX=189.939 EndY=31.5672 EndZ=0
    g26: LineSegment StartX=189.939 StartY=31.5672 StartZ=0 EndX=192.333 EndY=24.9893 EndZ=0
    g27: LineSegment StartX=192.333 StartY=24.9893 StartZ=0 EndX=196.467 EndY=26.4942 EndZ=0
    g28: LineSegment StartX=132.428 StartY=20 StartZ=0 EndX=144.053 EndY=20 EndZ=0
    g29: LineSegment StartX=144.053 StartY=20 StartZ=0 EndX=147.645 EndY=8.94427 EndZ=0
  constraints (65):
    c: Equal(g0,g-25)
    c: Equal(g2,g-29)
    c: Equal(g3,g-30)
    c: Equal(g4,g-28)
    c: Equal(g1,g-26)
    c: Coincident(g0,g-25)
    c: Coincident(g1,g-26)
    c: Coincident(g2,g-29)
    c: Coincident(g3,g-30)
    c: Coincident(g4,g-28)
    c: Equal(g5,g-23)
    c: Equal(g6,g-24)
    c: Coincident(g5,g-23)
    c: Coincident(g6,g-24)
    c: Equal(g7,g-20)
    c: Coincident(g7,g-20)
    c: Equal(g9,g-22)
    c: Coincident(g9,g-22)
    c: Equal(g8,g-21)
    c: Coincident(g8,g-21)
    c: Equal(g13,g-12)
    c: Equal(g12,g-14)
    c: Equal(g10,g-9)
    c: Equal(g11,g-7)
    c: Coincident(g14,g-27)
    c: Coincident(g14,g-27)
    c: Coincident(g15,g14)
    c: Coincident(g15,g-5)
    c: Coincident(g16,g15)
    c: Coincident(g16,g-6)
    c: Coincident(g17,g16)
    c: Coincident(g17,g-7)
    c: Coincident(g11,g17)
    c: Coincident(g11,g-8)
    c: Coincident(g18,g11)
    c: Coincident(g18,g-9)
    c: Coincident(g10,g18)
    c: Coincident(g10,g-10)
    c: Coincident(g19,g10)
    c: Coincident(g19,g-11)
    c: Coincident(g20,g19)
    c: Coincident(g20,g-12)
    c: Coincident(g13,g20)
    c: Coincident(g13,g-13)
    c: Coincident(g21,g13)
    c: Coincident(g21,g-14)
    c: Coincident(g12,g21)
    c: Coincident(g12,g-15)
    c: Coincident(g22,g12)
    c: Coincident(g22,g-15)
    c: Coincident(g23,g22)
    c: Coincident(g23,g14)
    c: Coincident(g24,g-18)
    c: Coincident(g24,g-16)
    c: Coincident(g25,g24)
    c: Coincident(g25,g-19)
    c: Coincident(g26,g25)
    c: Coincident(g26,g-19)
    c: Coincident(g27,g26)
    c: Coincident(g27,g24)
    c: Coincident(g29,g10)
    c: Coincident(g28,g10)
    c: Coincident(g29,g28)
    c: Parallel(g28,g18)
    c: Parallel(g29,g19)
FEATURE [PartDesign::Pad] Pad011
  Direction = (0,1,-2e-16)
  Length = 2
  Length2 = 10
  Profile = -> Sketch114
  ReferenceAxis = -> Sketch114 [N_Axis]
  Refine = true
  Reversed = true
  Suppressed = false
  Type = 0
FEATURE [Sketcher::SketchObject] Sketch115
  ArcFitTolerance = 1e-06
  AttachmentSupport = -> [Pad011]
  ExternalGeometry = -> [Binder001]
  FullyConstrained = true
  MakeInternals = false
  MapMode = 5
  Placement = pos=(0,1.7e-15,0) rot=(0,0.707107,0.707107;3.14159rad)
  sketch-geometry (4):
    g0: ArcOfCircle CenterX=24.2 CenterY=26.7 CenterZ=0 NormalX=0 NormalY=0 NormalZ=1 AngleXU=0 Radius=3 StartAngle=4.48384e-08 EndAngle=3.14159
    g1: ArcOfCircle CenterX=24.2 CenterY=15.7 CenterZ=0 NormalX=0 NormalY=0 NormalZ=1 AngleXU=0 Radius=3 StartAngle=3.14159 EndAngle=6.28318
    g2: LineSegment StartX=21.2 StartY=26.7 StartZ=0 EndX=21.2 EndY=15.7 EndZ=0
    g3: LineSegment StartX=27.2 StartY=26.7 StartZ=0 EndX=27.2 EndY=15.7 EndZ=0
  constraints (12):
    c: Equal(g1,g-4)
    c: Equal(g0,g-3)
    c: Coincident(g0,g-3)
    c: Coincident(g1,g-4)
    c: Vertical(g2)
    c: Vertical(g3)
    c: Tangent(g3,g-3)
    c: Tangent(g2,g-3)
    c: Coincident(g0,g2)
    c: Coincident(g0,g3)
    c: Coincident(g1,g2)
    c: Coincident(g3,g1)
FEATURE [Sketcher::SketchObject] Sketch117
  ArcFitTolerance = 1e-06
  AttachmentSupport = -> [Pad011]
  ExternalGeometry = -> [Binder001]
  FullyConstrained = true
  MakeInternals = false
  MapMode = 5
  Placement = pos=(0,1.7e-15,0) rot=(0,0.707107,0.707107;3.14159rad)
  sketch-geometry (4):
    g0: Circle CenterX=43.2 CenterY=30.3 CenterZ=0 NormalX=0 NormalY=0 NormalZ=1 AngleXU=0 Radius=2.25
    g1: Circle CenterX=43.2 CenterY=12.1 CenterZ=0 NormalX=0 NormalY=0 NormalZ=1 AngleXU=0 Radius=2.25
    g2: Circle CenterX=18.6 CenterY=30.3 CenterZ=0 NormalX=0 NormalY=0 NormalZ=1 AngleXU=0 Radius=2.25
    g3: Circle CenterX=18.6 CenterY=12.1 CenterZ=0 NormalX=0 NormalY=0 NormalZ=1 AngleXU=0 Radius=2.25
  constraints (8):
    c: Diameter(g0) = 4.5
    c: Diameter(g1) = 4.5
    c: Diameter(g2) = 4.5
    c: Diameter(g3) = 4.5
    c: Coincident(g2,g-3)
    c: Coincident(g3,g-6)
    c: Coincident(g0,g-4)
    c: Coincident(g1,g-5)
FEATURE [Sketcher::SketchObject] Sketch118
  ArcFitTolerance = 1e-06
  AttachmentSupport = -> [Pad011]
  ExternalGeometry = -> [Binder001]
  FullyConstrained = true
  MakeInternals = false
  MapMode = 5
  Placement = pos=(0,-2,0) rot=(1,0,0;1.5708rad)
  sketch-geometry (12):
    g0: Circle CenterX=-78.51 CenterY=34.8 CenterZ=0 NormalX=0 NormalY=0 NormalZ=1 AngleXU=0 Radius=1.8
    g1: Circle CenterX=-78.51 CenterY=7.6 CenterZ=0 NormalX=0 NormalY=0 NormalZ=1 AngleXU=0 Radius=1.8
    g2: Circle CenterX=-5.6 CenterY=34.8 CenterZ=0 NormalX=0 NormalY=0 NormalZ=1 AngleXU=0 Radius=1.8
    g3: Circle CenterX=-5.6 CenterY=7.6 CenterZ=0 NormalX=0 NormalY=0 NormalZ=1 AngleXU=0 Radius=1.8
    g4: LineSegment StartX=0 StartY=39.2 StartZ=0 EndX=0 EndY=3.2 EndZ=0
    g5: LineSegment StartX=0 StartY=3.2 StartZ=0 EndX=-82.8 EndY=3.2 EndZ=0
    g6: LineSegment StartX=-82.8 StartY=3.2 StartZ=0 EndX=-82.8 EndY=39.2 EndZ=0
    g7: LineSegment StartX=-82.8 StartY=39.2 StartZ=0 EndX=0 EndY=39.2 EndZ=0
    g8: ArcOfCircle CenterX=-65 CenterY=21.2 CenterZ=0 NormalX=0 NormalY=0 NormalZ=1 AngleXU=0 Radius=10 StartAngle=1.5708 EndAngle=4.71239
    g9: ArcOfCircle CenterX=-19 CenterY=21.2 CenterZ=0 NormalX=0 NormalY=0 NormalZ=1 AngleXU=0 Radius=10 StartAngle=4.71239 EndAngle=7.85398
    g10: LineSegment StartX=-65 StartY=31.2 StartZ=0 EndX=-19 EndY=31.2 EndZ=0
    g11: LineSegment StartX=-65 StartY=11.2 StartZ=0 EndX=-19 EndY=11.2 EndZ=0
  constraints (25):
    c: Equal(g2,g-5)
    c: Equal(g3,g-7)
    c: Equal(g1,g-6)
    c: Equal(g0,g-4)
    c: Coincident(g0,g-4)
    c: Coincident(g1,g-6)
    c: Coincident(g3,g-7)
    c: Coincident(g2,g-5)
    c: Coincident(g4,g-8)
    c: Coincident(g4,g-9)
    c: Coincident(g5,g4)
    c: Coincident(g5,g-10)
    c: Coincident(g6,g5)
    c: PointOnObject(g6,g-3)
    c: Vertical(g6)
    c: Coincident(g7,g6)
    c: Coincident(g7,g4)
    c: Tangent(g8,g10) = 1.5708
    c: Tangent(g8,g11) = -1.5708
    c: Tangent(g9,g10) = 1.5708
    c: Tangent(g9,g11) = -1.5708
    c: Equal(g8,g9)
    c: Radius(g8) = 10
    c: Coincident(g8,g-11)
    c: Coincident(g9,g-12)
FEATURE [Sketcher::SketchObject] Sketch120
  ArcFitTolerance = 1e-06
  AttachmentSupport = -> [Pad011]
  ExternalGeometry = -> [Binder001]
  FullyConstrained = true
  MakeInternals = false
  MapMode = 5
  Placement = pos=(0,-2,0) rot=(1,0,0;1.5708rad)
  sketch-geometry (4):
    g0: LineSegment StartX=-137.815 StartY=39.2 StartZ=0 EndX=-142.655 EndY=24.303 EndZ=0
    g1: LineSegment StartX=-137.815 StartY=39.2 StartZ=0 EndX=-110.815 EndY=39.2 EndZ=0
    g2: LineSegment StartX=-142.655 StartY=24.303 StartZ=0 EndX=-110.815 EndY=24.303 EndZ=0
    g3: ArcOfCircle CenterX=-92.2534 CenterY=31.7515 CenterZ=0 NormalX=0 NormalY=0 NormalZ=1 AngleXU=0 Radius=20 StartAngle=2.75997 EndAngle=3.52321
  constraints (12):
    c: PointOnObject(g0,g-3)
    c: Coincident(g1,g0)
    c: PointOnObject(g1,g-3)
    c: Coincident(g2,g0)
    c: Horizontal(g2)
    c: Tangent(g0,g-4)
    c: Vertical(g2,g1)
    c: DistanceX(g1,g1) = 27
    c: DistanceY(g-6,g0) = 4
    c: Radius(g3) = 20
    c: Coincident(g3,g1)
    c: Coincident(g3,g2)
FEATURE [Sketcher::SketchObject] Sketch121
  ArcFitTolerance = 1e-06
  AttachmentSupport = -> [Pad011]
  ExternalGeometry = -> [Binder001]
  FullyConstrained = true
  MakeInternals = false
  MapMode = 5
  Placement = pos=(0,-2,0) rot=(1,0,0;1.5708rad)
  sketch-geometry (15):
    g0: LineSegment StartX=-137.815 StartY=39.2 StartZ=0 EndX=-143.955 EndY=20.303 EndZ=0
    g1: LineSegment StartX=-143.955 StartY=20.303 StartZ=0 EndX=-190.141 EndY=20.303 EndZ=0
    g2: LineSegment StartX=-190.141 StartY=20.303 StartZ=0 EndX=-186.139 EndY=31.3 EndZ=0
    g3: LineSegment StartX=-178.754 StartY=39.2 StartZ=0 EndX=-180.791 EndY=33.6029 EndZ=0
    g4: ArcOfCircle CenterX=-184.08 CenterY=34.8 CenterZ=0 NormalX=0 NormalY=0 NormalZ=1 AngleXU=0 Radius=3.5 StartAngle=4.71239 EndAngle=5.93412
    g5: LineSegment StartX=-184.08 StartY=31.3 StartZ=0 EndX=-186.139 EndY=31.3 EndZ=0
    g6: LineSegment StartX=-137.815 StartY=39.2 StartZ=0 EndX=-156.815 EndY=39.2 EndZ=0
    g7: LineSegment StartX=-168.815 StartY=39.2 StartZ=0 EndX=-178.754 EndY=39.2 EndZ=0
    g8: LineSegment StartX=-157.815 StartY=39.2 StartZ=0 EndX=-167.815 EndY=39.2 EndZ=0
    g9: LineSegment StartX=-168.815 StartY=31.2 StartZ=0 EndX=-156.815 EndY=31.2 EndZ=0
    g10: LineSegment StartX=-167.436 StartY=36.2 StartZ=0 EndX=-157.436 EndY=36.2 EndZ=0
    g11: ArcOfCircle CenterX=-176.411 CenterY=35.2 CenterZ=0 NormalX=0 NormalY=0 NormalZ=1 AngleXU=0 Radius=20 StartAngle=6.08183 EndAngle=6.48454
    g12: ArcOfCircle CenterX=-188.411 CenterY=35.2 CenterZ=0 NormalX=0 NormalY=0 NormalZ=1 AngleXU=0 Radius=20 StartAngle=6.08183 EndAngle=6.48454
    g13: ArcOfCircle CenterX=-177.411 CenterY=35.2 CenterZ=0 NormalX=0 NormalY=0 NormalZ=1 AngleXU=0 Radius=20 StartAngle=0.0500209 EndAngle=0.201358
    g14: ArcOfCircle CenterX=-187.411 CenterY=35.2 CenterZ=0 NormalX=0 NormalY=0 NormalZ=1 AngleXU=0 Radius=20 StartAngle=0.0500209 EndAngle=0.201358
  constraints (46):
    c: PointOnObject(g0,g-3)
    c: Tangent(g0,g-5)
    c: Coincident(g1,g0)
    c: Horizontal(g1)
    c: Coincident(g2,g1)
    c: PointOnObject(g3,g-3)
    c: Parallel(g3,g-6)
    c: Parallel(g2,g-6)
    c: Radius(g4) = 3.5
    c: Coincident(g4,g-7)
    c: Tangent(g3,g4) = 1.5708
    c: Horizontal(g5)
    c: Tangent(g5,g4) = 1.5708
    c: DistanceX(g-8,g5) = 3.8
    c: Coincident(g2,g5)
    c: Coincident(g6,g0)
    c: PointOnObject(g6,g-3)
    c: DistanceX(g6,g6) = 19
    c: PointOnObject(g7,g-3)
    c: DistanceX(g7,g6) = 12
    c: Coincident(g7,g3)
    c: PointOnObject(g8,g-3)
    c: PointOnObject(g8,g-3)
    c: DistanceX(g8,g8) = 10
    c: DistanceX(g8,g6) = 1
    c: Horizontal(g9)
    c: Vertical(g7,g9)
    c: Vertical(g6,g9)
    c: DistanceY(g9,g7) = 8
    c: Horizontal(g10)
    c: Equal(g8,g10)
    c: DistanceY(g10,g8) = 3
    c: Radius(g11) = 20
    c: Coincident(g11,g6)
    c: Coincident(g11,g9)
    c: Radius(g12) = 20
    c: Coincident(g12,g7)
    c: Coincident(g12,g9)
    c: Equal(g13,g11)
    c: Coincident(g13,g8)
    c: Coincident(g13,g10)
    c: Horizontal(g13,g11)
    c: Equal(g14,g12)
    c: Coincident(g14,g8)
    c: Coincident(g14,g10)
    c: Horizontal(g1,g-6)
FEATURE [Sketcher::SketchObject] Sketch122
  ArcFitTolerance = 1e-06
  AttachmentSupport = -> [Pad011]
  ExternalGeometry = -> [Binder001]
  FullyConstrained = true
  MakeInternals = false
  MapMode = 5
  Placement = pos=(0,-2,0) rot=(1,0,0;1.5708rad)
  sketch-geometry (8):
    g0: LineSegment StartX=-202.765 StartY=20.303 StartZ=0 EndX=-143.955 EndY=20.303 EndZ=0
    g1: ArcOfCircle CenterX=-184.801 CenterY=-67.3089 CenterZ=0 NormalX=0 NormalY=0 NormalZ=1 AngleXU=0 Radius=33.7833 StartAngle=2.70526 EndAngle=3.54053
    g2: LineSegment StartX=-176.685 StartY=-80.4316 StartZ=0 EndX=-215.932 EndY=-80.4316 EndZ=0
    g3: LineSegment StartX=-215.42 StartY=-53.0315 StartZ=0 EndX=-192.176 EndY=-3.18454 EndZ=0
    g4: ArcOfCircle CenterX=-207.583 CenterY=4 CenterZ=0 NormalX=0 NormalY=0 NormalZ=1 AngleXU=0 Radius=17 StartAngle=5.84685 EndAngle=7.56663
    g5: Circle CenterX=-213.443 CenterY=-76.8316 CenterZ=0 NormalX=0 NormalY=0 NormalZ=1 AngleXU=0 Radius=3
    g6: Circle CenterX=-179.305 CenterY=-76.8316 CenterZ=0 NormalX=0 NormalY=0 NormalZ=1 AngleXU=0 Radius=3
    g7: LineSegment StartX=-143.955 StartY=20.303 StartZ=0 EndX=-176.685 EndY=-80.4316 EndZ=0
  constraints (18):
    c: Coincident(g0,g-6)
    c: Coincident(g1,g-7)
    c: Coincident(g1,g-8)
    c: Coincident(g2,g1)
    c: Tangent(g3,g-5)
    c: Coincident(g4,g-6)
    c: Coincident(g4,g0)
    c: Coincident(g3,g4)
    c: Coincident(g1,g3)
    c: Diameter(g5) = 6
    c: Diameter(g6) = 6
    c: Coincident(g5,g-9)
    c: Coincident(g6,g-10)
    c: Horizontal(g0)
    c: Horizontal(g2)
    c: Coincident(g7,g0)
    c: Coincident(g7,g2)
    c: Tangent(g7,g-4)
FEATURE [Sketcher::SketchObject] Sketch123
  ArcFitTolerance = 1e-06
  AttachmentSupport = -> [Pad011]
  ExternalGeometry = -> [Binder001]
  FullyConstrained = true
  MakeInternals = false
  MapMode = 5
  Placement = pos=(0,-2,0) rot=(1,0,0;1.5708rad)
  sketch-geometry (4):
    g0: LineSegment StartX=-108 StartY=36.8 StartZ=0 EndX=-90 EndY=36.8 EndZ=0
    g1: LineSegment StartX=-108 StartY=36.8 StartZ=0 EndX=-108 EndY=26.8 EndZ=0
    g2: LineSegment StartX=-108 StartY=26.8 StartZ=0 EndX=-90 EndY=26.8 EndZ=0
    g3: ArcOfCircle CenterX=-94 CenterY=31.8 CenterZ=0 NormalX=0 NormalY=0 NormalZ=1 AngleXU=0 Radius=6.40312 StartAngle=5.38713 EndAngle=7.17924
  constraints (13):
    c: Horizontal(g0)
    c: Coincident(g1,g0)
    c: Vertical(g1)
    c: Coincident(g2,g1)
    c: Horizontal(g2)
    c: DistanceX(g0,g0) = 18
    c: DistanceY(g1,g1) = 10
    c: Equal(g0,g2)
    c: DistanceX(g0,g-3) = 90
    c: DistanceY(g0,g-3) = 2.4
    c: Coincident(g3,g0)
    c: Coincident(g3,g2)
    c: DistanceX(g3,g0) = 4
FEATURE [PartDesign::Chamfer] Chamfer014
  Angle = 45
  Base = -> Pad011 [Edge80,Edge4,Edge7]
  BaseFeature = -> Pad011
  ChamferType = 0
  FlipDirection = false
  Refine = true
  Size = 1.9
  Size2 = 1
  SupportTransform = false
  Suppressed = false
  UseAllEdges = false
FEATURE [PartDesign::Pocket] Pocket006
  BaseFeature = -> Chamfer014
  Direction = (0,-1,2e-16)
  Length = 1.2
  Length2 = 5
  Profile = -> Sketch115
  ReferenceAxis = -> Sketch115 [N_Axis]
  Refine = true
  Suppressed = false
  Type = 0
FEATURE [Sketcher::SketchObject] Sketch116
  ArcFitTolerance = 1e-06
  AttachmentSupport = -> [Pocket006]
  ExternalGeometry = -> [Binder001]
  FullyConstrained = true
  MakeInternals = false
  MapMode = 5
  Placement = pos=(0,1.7e-15,0) rot=(0,0.707107,0.707107;3.14159rad)
  sketch-geometry (4):
    g0: Circle CenterX=43.2 CenterY=30.3 CenterZ=0 NormalX=0 NormalY=0 NormalZ=1 AngleXU=0 Radius=3.4
    g1: Circle CenterX=43.2 CenterY=12.1 CenterZ=0 NormalX=0 NormalY=0 NormalZ=1 AngleXU=0 Radius=3.4
    g2: Circle CenterX=18.6 CenterY=30.3 CenterZ=0 NormalX=0 NormalY=0 NormalZ=1 AngleXU=0 Radius=3.4
    g3: Circle CenterX=18.6 CenterY=12.1 CenterZ=0 NormalX=0 NormalY=0 NormalZ=1 AngleXU=0 Radius=3.4
  constraints (8):
    c: Diameter(g0) = 6.8
    c: Diameter(g1) = 6.8
    c: Diameter(g2) = 6.8
    c: Diameter(g3) = 6.8
    c: Coincident(g2,g-3)
    c: Coincident(g0,g-4)
    c: Coincident(g3,g-6)
    c: Coincident(g1,g-5)
FEATURE [PartDesign::Pad] Pad012
  BaseFeature = -> Pocket006
  Direction = (0,1,-2e-16)
  Length = 2.4
  Length2 = 10
  Profile = -> Sketch116
  ReferenceAxis = -> Sketch116 [N_Axis]
  Refine = true
  Suppressed = false
  Type = 0
FEATURE [PartDesign::Pocket] Pocket007
  BaseFeature = -> Pad012
  Direction = (0,-1,2e-16)
  Length = 0.6
  Length2 = 2.4
  Profile = -> Sketch117
  ReferenceAxis = -> Sketch117 [N_Axis]
  Refine = true
  Suppressed = false
  Type = 4
FEATURE [PartDesign::Pad] Pad013
  BaseFeature = -> Pocket007
  Direction = (0,-1,2e-16)
  Length = 1.6
  Length2 = 10
  Profile = -> Sketch118
  ReferenceAxis = -> Sketch118 [N_Axis]
  Refine = true
  Suppressed = false
  Type = 0
FEATURE [Sketcher::SketchObject] Sketch119
  ArcFitTolerance = 1e-06
  AttachmentSupport = -> [Pad013]
  ExternalGeometry = -> [Binder001]
  FullyConstrained = true
  MakeInternals = false
  MapMode = 5
  Placement = pos=(0,-3.6,0) rot=(1,0,0;1.5708rad)
  sketch-geometry (21):
    g0: LineSegment [constr] StartX=-82.8 StartY=3.2 StartZ=0 EndX=-82.8 EndY=39.2 EndZ=0
    g1: ArcOfCircle CenterX=-78.51 CenterY=34.8 CenterZ=0 NormalX=0 NormalY=0 NormalZ=1 AngleXU=0 Radius=3.5 StartAngle=4.71239 EndAngle=6.28319
    g2: ArcOfCircle CenterX=-78.51 CenterY=7.6 CenterZ=0 NormalX=0 NormalY=0 NormalZ=1 AngleXU=0 Radius=3.5 StartAngle=0 EndAngle=1.5708
    g3: ArcOfCircle CenterX=-5.6 CenterY=34.8 CenterZ=0 NormalX=0 NormalY=0 NormalZ=1 AngleXU=0 Radius=3.5 StartAngle=3.14159 EndAngle=4.71239
    g4: ArcOfCircle CenterX=-5.6 CenterY=7.6 CenterZ=0 NormalX=0 NormalY=0 NormalZ=1 AngleXU=0 Radius=3.5 StartAngle=1.5708 EndAngle=3.14159
    g5: LineSegment StartX=0 StartY=39.2 StartZ=0 EndX=0 EndY=31.3 EndZ=0
    g6: LineSegment StartX=0 StartY=39.2 StartZ=0 EndX=-9.1 EndY=39.2 EndZ=0
    g7: LineSegment StartX=0 StartY=3.2 StartZ=0 EndX=0 EndY=11.1 EndZ=0
    g8: LineSegment StartX=0 StartY=3.2 StartZ=0 EndX=-9.1 EndY=3.2 EndZ=0
    g9: LineSegment StartX=-82.8 StartY=3.2 StartZ=0 EndX=-75.01 EndY=3.2 EndZ=0
    g10: LineSegment StartX=-82.8 StartY=3.2 StartZ=0 EndX=-82.8 EndY=11.1 EndZ=0
    g11: LineSegment StartX=-82.8 StartY=39.2 StartZ=0 EndX=-82.8 EndY=31.3 EndZ=0
    g12: LineSegment StartX=-82.8 StartY=39.2 StartZ=0 EndX=-75.01 EndY=39.2 EndZ=0
    g13: LineSegment StartX=-82.8 StartY=31.3 StartZ=0 EndX=-78.51 EndY=31.3 EndZ=0
    g14: LineSegment StartX=-75.01 StartY=39.2 StartZ=0 EndX=-75.01 EndY=34.8 EndZ=0
    g15: LineSegment StartX=-82.8 StartY=11.1 StartZ=0 EndX=-78.51 EndY=11.1 EndZ=0
    g16: LineSegment StartX=-75.01 StartY=3.2 StartZ=0 EndX=-75.01 EndY=7.6 EndZ=0
    g17: LineSegment StartX=-9.1 StartY=39.2 StartZ=0 EndX=-9.1 EndY=34.8 EndZ=0
    g18: LineSegment StartX=0 StartY=31.3 StartZ=0 EndX=-5.6 EndY=31.3 EndZ=0
    g19: LineSegment StartX=0 StartY=11.1 StartZ=0 EndX=-5.6 EndY=11.1 EndZ=0
    g20: LineSegment StartX=-9.1 StartY=3.2 StartZ=0 EndX=-9.1 EndY=7.6 EndZ=0
  constraints (51):
    c: Coincident(g0,g-10)
    c: PointOnObject(g0,g-8)
    c: Vertical(g0)
    c: Coincident(g1,g-3)
    c: Coincident(g2,g-4)
    c: Coincident(g3,g-5)
    c: Coincident(g4,g-6)
    c: Radius(g4) = 3.5
    c: Radius(g3) = 3.5
    c: Radius(g1) = 3.5
    c: Radius(g2) = 3.5
    c: Coincident(g5,g-9)
    c: PointOnObject(g5,g-9)
    c: Coincident(g6,g5)
    c: PointOnObject(g6,g-8)
    c: Coincident(g7,g-9)
    c: PointOnObject(g7,g-9)
    c: Coincident(g8,g7)
    c: PointOnObject(g8,g-7)
    c: Coincident(g9,g0)
    c: PointOnObject(g9,g-7)
    c: Coincident(g10,g0)
    c: PointOnObject(g10,g0)
    c: Coincident(g11,g0)
    c: PointOnObject(g11,g0)
    c: Coincident(g12,g0)
    c: PointOnObject(g12,g-8)
    c: Coincident(g13,g11)
    c: Horizontal(g13)
    c: Coincident(g14,g12)
    c: Vertical(g14)
    c: Coincident(g15,g10)
    c: Horizontal(g15)
    c: Coincident(g16,g9)
    c: Vertical(g16)
    c: Coincident(g17,g6)
    c: Vertical(g17)
    c: Coincident(g18,g5)
    c: Horizontal(g18)
    c: Coincident(g19,g7)
    c: Horizontal(g19)
    c: Coincident(g20,g8)
    c: Vertical(g20)
    c: Tangent(g20,g4) = 1.5708
    c: Tangent(g4,g19) = -1.5708
    c: Tangent(g18,g3) = 1.5708
    c: Tangent(g3,g17) = -1.5708
    c: Tangent(g13,g1) = -1.5708
    c: Tangent(g1,g14) = 1.5708
    c: Tangent(g16,g2) = -1.5708
    c: Tangent(g2,g15) = 1.5708
FEATURE [PartDesign::Pocket] Pocket008
  BaseFeature = -> Pad013
  Direction = (0,1,-2e-16)
  Length = 1.6
  Length2 = 5
  Profile = -> Sketch119
  ReferenceAxis = -> Sketch119 [N_Axis]
  Refine = true
  Suppressed = false
  Type = 0
FEATURE [PartDesign::Pad] Pad017
  BaseFeature = -> Pocket008
  Direction = (0,-1,2e-16)
  Length = 1.6
  Length2 = 10
  Profile = -> Sketch123
  ReferenceAxis = -> Sketch123 [N_Axis]
  Refine = true
  Suppressed = false
  Type = 0
FEATURE [Sketcher::SketchObject] Sketch125
  ArcFitTolerance = 1e-06
  AttachmentSupport = -> [Pad017]
  ExternalGeometry = -> [Pad017]
  FullyConstrained = true
  MakeInternals = false
  MapMode = 5
  Placement = pos=(0,-3.6,8e-16) rot=(1,0,0;1.5708rad)
  sketch-geometry (20):
    g0: LineSegment StartX=-108 StartY=35.8 StartZ=0 EndX=-108 EndY=35 EndZ=0
    g1: LineSegment StartX=-108 StartY=35 StartZ=0 EndX=-97 EndY=35 EndZ=0
    g2: LineSegment StartX=-97 StartY=35 StartZ=0 EndX=-97 EndY=35.8 EndZ=0
    g3: LineSegment StartX=-97 StartY=35.8 StartZ=0 EndX=-108 EndY=35.8 EndZ=0
    g4: LineSegment StartX=-108 StartY=28.6 StartZ=0 EndX=-108 EndY=27.8 EndZ=0
    g5: LineSegment StartX=-108 StartY=27.8 StartZ=0 EndX=-97 EndY=27.8 EndZ=0
    g6: LineSegment StartX=-97 StartY=27.8 StartZ=0 EndX=-97 EndY=28.6 EndZ=0
    g7: LineSegment StartX=-97 StartY=28.6 StartZ=0 EndX=-108 EndY=28.6 EndZ=0
    g8: LineSegment StartX=-108 StartY=30.4 StartZ=0 EndX=-108 EndY=29.6 EndZ=0
    g9: LineSegment StartX=-108 StartY=29.6 StartZ=0 EndX=-97 EndY=29.6 EndZ=0
    g10: LineSegment StartX=-97 StartY=29.6 StartZ=0 EndX=-97 EndY=30.4 EndZ=0
    g11: LineSegment StartX=-97 StartY=30.4 StartZ=0 EndX=-108 EndY=30.4 EndZ=0
    g12: LineSegment StartX=-108 StartY=32.2 StartZ=0 EndX=-108 EndY=31.4 EndZ=0
    g13: LineSegment StartX=-108 StartY=31.4 StartZ=0 EndX=-97 EndY=31.4 EndZ=0
    g14: LineSegment StartX=-97 StartY=31.4 StartZ=0 EndX=-97 EndY=32.2 EndZ=0
    g15: LineSegment StartX=-97 StartY=32.2 StartZ=0 EndX=-108 EndY=32.2 EndZ=0
    g16: LineSegment StartX=-108 StartY=34 StartZ=0 EndX=-108 EndY=33.2 EndZ=0
    g17: LineSegment StartX=-108 StartY=33.2 StartZ=0 EndX=-97 EndY=33.2 EndZ=0
    g18: LineSegment StartX=-97 StartY=33.2 StartZ=0 EndX=-97 EndY=34 EndZ=0
    g19: LineSegment StartX=-97 StartY=34 StartZ=0 EndX=-108 EndY=34 EndZ=0
  constraints (55):
    c: Coincident(g1,g0)
    c: Horizontal(g1)
    c: Coincident(g2,g1)
    c: Vertical(g2)
    c: Coincident(g3,g2)
    c: Horizontal(g3)
    c: Coincident(g3,g0)
    c: DistanceX(g1,g1) = 11
    c: DistanceY(g2,g2) = 0.8
    c: Coincident(g5,g4)
    c: Horizontal(g5)
    c: Coincident(g6,g5)
    c: Vertical(g6)
    c: Coincident(g7,g6)
    c: Horizontal(g7)
    c: Coincident(g7,g4)
    c: Coincident(g9,g8)
    c: Horizontal(g9)
    c: Coincident(g10,g9)
    c: Vertical(g10)
    c: Coincident(g11,g10)
    c: Horizontal(g11)
    c: Coincident(g11,g8)
    c: Coincident(g13,g12)
    c: Horizontal(g13)
    c: Coincident(g14,g13)
    c: Vertical(g14)
    c: Coincident(g15,g14)
    c: Horizontal(g15)
    c: Coincident(g15,g12)
    c: Coincident(g17,g16)
    c: Horizontal(g17)
    c: Coincident(g18,g17)
    c: Vertical(g18)
    c: Coincident(g19,g18)
    c: Horizontal(g19)
    c: Coincident(g19,g16)
    c: Equal(g3,g19)
    c: Equal(g3,g15)
    c: Equal(g3,g11)
    c: Equal(g3,g7)
    c: Equal(g2,g18)
    c: Equal(g2,g14)
    c: Equal(g2,g10)
    c: Equal(g2,g6)
    c: DistanceY(g-4,g4) = 1
    c: DistanceY(g4,g8) = 1
    c: DistanceY(g8,g12) = 1
    c: DistanceY(g12,g16) = 1
    c: DistanceY(g16,g0) = 1
    c: Tangent(g0,g-5)
    c: Tangent(g16,g-5)
    c: Tangent(g12,g-5)
    c: Tangent(g8,g-5)
    c: Tangent(g4,g-5)
FEATURE [PartDesign::Chamfer] Chamfer009
  Angle = 45
  Base = -> Pad017 [Edge151,Edge154]
  BaseFeature = -> Pad017
  ChamferType = 1
  FlipDirection = false
  Refine = true
  Size = 1.5
  Size2 = 2.8
  SupportTransform = false
  Suppressed = false
  UseAllEdges = false
FEATURE [PartDesign::Pocket] Pocket009
  BaseFeature = -> Chamfer009
  Direction = (0,1,-2e-16)
  Length = 1
  Length2 = 5
  Profile = -> Sketch125
  ReferenceAxis = -> Sketch125 [N_Axis]
  Refine = true
  Suppressed = false
  Type = 0
FEATURE [PartDesign::Pad] Pad014
  BaseFeature = -> Pocket009
  Direction = (0,-1,2e-16)
  Length = 0.8
  Length2 = 10
  Profile = -> Sketch120
  ReferenceAxis = -> Sketch120 [N_Axis]
  Refine = true
  Suppressed = false
  Type = 0
FEATURE [Sketcher::SketchObject] Sketch124
  ArcFitTolerance = 1e-06
  AttachmentSupport = -> [Pad014]
  ExternalGeometry = -> [Binder001]
  FullyConstrained = true
  MakeInternals = false
  MapMode = 5
  Placement = pos=(0,-2.8,6e-16) rot=(1,0,0;1.5708rad)
  sketch-geometry (4):
    g0: LineSegment StartX=-129 StartY=39.2 StartZ=0 EndX=-131.599 EndY=31.2 EndZ=0
    g1: LineSegment StartX=-118 StartY=39.2 StartZ=0 EndX=-120.599 EndY=31.2 EndZ=0
    g2: LineSegment StartX=-129 StartY=39.2 StartZ=0 EndX=-118 EndY=39.2 EndZ=0
    g3: LineSegment StartX=-120.599 StartY=31.2 StartZ=0 EndX=-131.599 EndY=31.2 EndZ=0
  constraints (12):
    c: PointOnObject(g0,g-3)
    c: PointOnObject(g1,g-3)
    c: Parallel(g-4,g0)
    c: Parallel(g-4,g1)
    c: Coincident(g2,g0)
    c: Coincident(g2,g1)
    c: DistanceX(g2,g2) = 11
    c: DistanceY(g1,g1) = 8
    c: Coincident(g3,g1)
    c: Horizontal(g3)
    c: Coincident(g3,g0)
    c: DistanceX(g1,g-3) = 118
FEATURE [PartDesign::Pad] Pad018
  BaseFeature = -> Pad014
  Direction = (0,-1,2e-16)
  Length = 1.2
  Length2 = 10
  Profile = -> Sketch124
  ReferenceAxis = -> Sketch124 [N_Axis]
  Refine = true
  Suppressed = false
  Type = 0
FEATURE [Sketcher::SketchObject] Sketch126
  ArcFitTolerance = 1e-06
  AttachmentSupport = -> [Pad018]
  ExternalGeometry = -> [Pad018]
  FullyConstrained = true
  MakeInternals = false
  MapMode = 5
  Placement = pos=(0,-4,0) rot=(1,0,0;1.5708rad)
  sketch-geometry (8):
    g0: LineSegment StartX=-129.877 StartY=36.5 StartZ=0 EndX=-130.137 EndY=35.7 EndZ=0
    g1: LineSegment StartX=-130.69 StartY=34 StartZ=0 EndX=-130.95 EndY=33.2 EndZ=0
    g2: LineSegment StartX=-129.877 StartY=36.5 StartZ=0 EndX=-118.877 EndY=36.5 EndZ=0
    g3: LineSegment StartX=-130.137 StartY=35.7 StartZ=0 EndX=-119.137 EndY=35.7 EndZ=0
    g4: LineSegment StartX=-130.69 StartY=34 StartZ=0 EndX=-119.69 EndY=34 EndZ=0
    g5: LineSegment StartX=-130.95 StartY=33.2 StartZ=0 EndX=-119.95 EndY=33.2 EndZ=0
    g6: LineSegment StartX=-118.877 StartY=36.5 StartZ=0 EndX=-119.137 EndY=35.7 EndZ=0
    g7: LineSegment StartX=-119.69 StartY=34 StartZ=0 EndX=-119.95 EndY=33.2 EndZ=0
  constraints (20):
    c: Coincident(g2,g0)
    c: Horizontal(g2)
    c: Coincident(g3,g0)
    c: Horizontal(g3)
    c: Coincident(g4,g1)
    c: Horizontal(g4)
    c: Coincident(g5,g1)
    c: Horizontal(g5)
    c: Coincident(g6,g2)
    c: Coincident(g6,g3)
    c: Coincident(g7,g4)
    c: Coincident(g7,g5)
    c: Tangent(g0,g-4)
    c: Tangent(g6,g-5)
    c: Tangent(g1,g-4)
    c: Tangent(g7,g-5)
    c: DistanceY(g3,g2) = 0.8
    c: DistanceY(g5,g4) = 0.8
    c: DistanceY(g-6,g1) = 2
    c: DistanceY(g-6,g0) = 4.5
FEATURE [PartDesign::Chamfer] Chamfer008
  Angle = 45
  Base = -> Pad018 [Edge257]
  BaseFeature = -> Pad018
  ChamferType = 1
  FlipDirection = false
  Refine = true
  Size = 1
  Size2 = 6
  SupportTransform = false
  Suppressed = false
  UseAllEdges = false
FEATURE [PartDesign::Pocket] Pocket010
  BaseFeature = -> Chamfer008
  Direction = (0,1,-2e-16)
  Length = 1
  Length2 = 5
  Profile = -> Sketch126
  ReferenceAxis = -> Sketch126 [N_Axis]
  Refine = true
  Suppressed = false
  Type = 0
FEATURE [PartDesign::Pad] Pad015
  BaseFeature = -> Pocket010
  Direction = (0,-1,2e-16)
  Length = 2
  Length2 = 10
  Profile = -> Sketch121
  ReferenceAxis = -> Sketch121 [N_Axis]
  Refine = true
  Suppressed = false
  Type = 0
FEATURE [PartDesign::Pad] Pad016
  BaseFeature = -> Pad015
  Direction = (0,-1,2e-16)
  Length = 1.6
  Length2 = 10
  Profile = -> Sketch122
  ReferenceAxis = -> Sketch122 [N_Axis]
  Refine = true
  Suppressed = false
  Type = 0
FEATURE [Sketcher::SketchObject] Sketch127
  ArcFitTolerance = 1e-06
  AttachmentSupport = -> [Pad016]
  ExternalGeometry = -> [Pad016]
  FullyConstrained = true
  MakeInternals = false
  MapMode = 5
  Placement = pos=(0,0,-80.4316) rot=(1,0,0;3.14159rad)
  sketch-geometry (8):
    g0: LineSegment StartX=-176.685 StartY=3.6 StartZ=0 EndX=-186.685 EndY=3.6 EndZ=0
    g1: LineSegment [constr] StartX=-186.685 StartY=3.6 StartZ=0 EndX=-186.685 EndY=-9e-16 EndZ=0
    g2: LineSegment StartX=-176.685 StartY=3.6 StartZ=0 EndX=-176.685 EndY=0 EndZ=0
    g3: ArcOfEllipse CenterX=-186.685 CenterY=-9e-16 CenterZ=0 NormalX=0 NormalY=0 NormalZ=1 MajorRadius=10 MinorRadius=3.6 AngleXU=1e-16 StartAngle=0 EndAngle=1.5708
    g4: LineSegment [constr] StartX=-176.685 StartY=-2e-15 StartZ=0 EndX=-196.685 EndY=-2e-15 EndZ=0
    g5: LineSegment [constr] StartX=-186.685 StartY=3.6 StartZ=0 EndX=-186.685 EndY=-3.6 EndZ=0
    g6: GeomPoint [constr] X=-177.356 Y=0 Z=0
    g7: GeomPoint [constr] X=-196.015 Y=-1.9e-15 Z=0
  constraints (13):
    c: Coincident(g0,g-4)
    c: PointOnObject(g0,g-4)
    c: DistanceX(g0,g0) = 10
    c: Coincident(g1,g0)
    c: PointOnObject(g1,g-5)
    c: Vertical(g1)
    c: Coincident(g2,g0)
    c: Coincident(g2,g-5)
    c: InternalAlignment(g4-g7 -> g3) x4
    c: Coincident(g3,g1)
    c: Coincident(g3,g0)
    c: Coincident(g3,g2)
    c: Horizontal(g4)
FEATURE [Sketcher::SketchObject] Sketch128
  ArcFitTolerance = 1e-06
  AttachmentSupport = -> [Pad016]
  ExternalGeometry = -> [Pad016]
  FullyConstrained = true
  MakeInternals = false
  MapMode = 5
  Placement = pos=(0,0,-80.4316) rot=(1,0,0;3.14159rad)
  sketch-geometry (8):
    g0: LineSegment StartX=-215.932 StartY=3.6 StartZ=0 EndX=-215.932 EndY=-1.3e-15 EndZ=0
    g1: LineSegment StartX=-215.932 StartY=3.6 StartZ=0 EndX=-205.932 EndY=3.6 EndZ=0
    g2: LineSegment [constr] StartX=-205.932 StartY=3.6 StartZ=0 EndX=-205.932 EndY=-9e-16 EndZ=0
    g3: ArcOfEllipse CenterX=-205.932 CenterY=-9e-16 CenterZ=0 NormalX=0 NormalY=0 NormalZ=1 MajorRadius=10 MinorRadius=3.6 AngleXU=-3.14159 StartAngle=4.71239 EndAngle=6.28319
    g4: LineSegment [constr] StartX=-215.932 StartY=-1e-15 StartZ=0 EndX=-195.932 EndY=-1e-15 EndZ=0
    g5: LineSegment [constr] StartX=-205.932 StartY=-3.6 StartZ=0 EndX=-205.932 EndY=3.6 EndZ=0
    g6: GeomPoint [constr] X=-215.262 Y=-2e-15 Z=0
    g7: GeomPoint [constr] X=-196.602 Y=-1e-15 Z=0
  constraints (13):
    c: Coincident(g0,g-4)
    c: Coincident(g0,g-5)
    c: Coincident(g1,g0)
    c: PointOnObject(g1,g-3)
    c: DistanceX(g1,g1) = 10
    c: Coincident(g2,g1)
    c: Vertical(g2)
    c: PointOnObject(g2,g-5)
    c: InternalAlignment(g4-g7 -> g3) x4
    c: Coincident(g3,g2)
    c: Coincident(g3,g1)
    c: Coincident(g3,g0)
    c: Horizontal(g4)
FEATURE [PartDesign::SubtractivePipe] SubtractivePipe002
  AuxilleryCurvelinear = true
  AuxillerySpineTangent = false
  BaseFeature = -> Pad016
  Binormal = (0,0,0)
  Mode = 0
  Profile = -> Sketch127
  Refine = true
  Spine = -> Pad016 [Edge254]
  SpineTangent = false
  Suppressed = false
  Transformation = 0
  Transition = 0
FEATURE [PartDesign::SubtractivePipe] SubtractivePipe003
  AuxilleryCurvelinear = true
  AuxillerySpineTangent = false
  BaseFeature = -> SubtractivePipe002
  Binormal = (0,0,0)
  Mode = 0
  Profile = -> Sketch128
  Refine = true
  Spine = -> Pad016 [Edge256,Edge251,Edge252]
  SpineTangent = false
  Suppressed = false
  Transformation = 0
  Transition = 0
FEATURE [Sketcher::SketchObject] Sketch129
  ArcFitTolerance = 1e-06
  AttachmentSupport = -> [Pad016]
  ExternalGeometry = -> [Binder001]
  FullyConstrained = true
  MakeInternals = false
  MapMode = 5
  Placement = pos=(0,-3.6,0) rot=(1,0,0;1.5708rad)
  sketch-geometry (12):
    g0: LineSegment [constr] StartX=-192.176 StartY=-3.18451 StartZ=0 EndX=-181.223 EndY=20.303 EndZ=0
    g1: LineSegment [constr] StartX=-202.765 StartY=20.303 StartZ=0 EndX=-181.223 EndY=20.303 EndZ=0
    g2: LineSegment StartX=-202.765 StartY=20.303 StartZ=0 EndX=-181.223 EndY=20.303 EndZ=0
    g3: LineSegment StartX=-192.176 StartY=-3.18451 StartZ=0 EndX=-196.804 EndY=-13.1107 EndZ=0
    g4: ArcOfCircle CenterX=-207.583 CenterY=4 CenterZ=0 NormalX=0 NormalY=0 NormalZ=1 AngleXU=0 Radius=17 StartAngle=5.84685 EndAngle=7.56663
    g5: ArcOfEllipse CenterX=-181.223 CenterY=8.55923 CenterZ=0 NormalX=0 NormalY=0 NormalZ=1 MajorRadius=23.4779 MinorRadius=11.7437 AngleXU=2e-16 StartAngle=4.71239 EndAngle=7.85398
    g6: LineSegment [constr] StartX=-157.745 StartY=8.55923 StartZ=0 EndX=-204.701 EndY=8.55923 EndZ=0
    g7: LineSegment [constr] StartX=-181.223 StartY=20.303 StartZ=0 EndX=-181.223 EndY=-3.18451 EndZ=0
    g8: GeomPoint [constr] X=-160.894 Y=8.55923 Z=0
    g9: GeomPoint [constr] X=-201.553 Y=8.55923 Z=0
    g10: ArcOfCircle CenterX=-181.223 CenterY=-20.3763 CenterZ=0 NormalX=0 NormalY=0 NormalZ=1 AngleXU=0 Radius=17.1918 StartAngle=1.57079 EndAngle=2.70526
    g11: GeomPoint [constr] X=-181.223 Y=-3.18451 Z=0
  constraints (23):
    c: Coincident(g0,g-5)
    c: Coincident(g1,g-6)
    c: Horizontal(g1)
    c: Coincident(g1,g0)
    c: Parallel(g0,g-4)
    c: Coincident(g2,g1)
    c: Coincident(g2,g0)
    c: Coincident(g3,g0)
    c: Equal(g4,g-5)
    c: Coincident(g4,g1)
    c: Coincident(g4,g0)
    c: InternalAlignment(g6-g9 -> g5) x4
    c: Vertical(g5,g0)
    c: Horizontal(g6)
    c: Coincident(g5,g0)
    c: DistanceX(g6,g-3) = 10.1
    c: Tangent(g10,g3) = -1.5708
    c: PointOnObject(g11,g10)
    c: Tangent(g5,g10,g11) = 1.5708
    c: Coincident(g10,g5)
    c: Coincident(g11,g7)
    c: Parallel(g3,g-4)
    c: Horizontal(g5,g0)
FEATURE [Sketcher::SketchObject] Sketch130
  ArcFitTolerance = 1e-06
  AttachmentOffset = pos=(0,0,-1.6) rot=(0,0,1;0rad)
  AttachmentSupport = -> [Pad016]
  ExternalGeometry = -> [Binder001]
  FullyConstrained = true
  MakeInternals = false
  MapMode = 5
  Placement = pos=(0,-2,-4e-16) rot=(1,0,0;1.5708rad)
  sketch-geometry (12):
    g0: LineSegment [constr] StartX=-192.176 StartY=-3.18451 StartZ=0 EndX=-181.223 EndY=20.303 EndZ=0
    g1: LineSegment [constr] StartX=-202.765 StartY=20.303 StartZ=0 EndX=-181.223 EndY=20.303 EndZ=0
    g2: LineSegment StartX=-202.765 StartY=20.303 StartZ=0 EndX=-181.223 EndY=20.303 EndZ=0
    g3: LineSegment StartX=-192.176 StartY=-3.18451 StartZ=0 EndX=-193.827 EndY=-6.72678 EndZ=0
    g4: ArcOfCircle CenterX=-207.583 CenterY=4 CenterZ=0 NormalX=0 NormalY=0 NormalZ=1 AngleXU=0 Radius=17 StartAngle=5.84685 EndAngle=7.56663
    g5: ArcOfEllipse CenterX=-181.223 CenterY=10.803 CenterZ=0 NormalX=0 NormalY=0 NormalZ=1 MajorRadius=14.4779 MinorRadius=9.5 AngleXU=0 StartAngle=4.71239 EndAngle=7.85398
    g6: LineSegment [constr] StartX=-166.745 StartY=10.803 StartZ=0 EndX=-195.701 EndY=10.803 EndZ=0
    g7: LineSegment [constr] StartX=-181.223 StartY=20.303 StartZ=0 EndX=-181.223 EndY=1.30297 EndZ=0
    g8: GeomPoint [constr] X=-170.298 Y=10.803 Z=0
    g9: GeomPoint [constr] X=-192.148 Y=10.803 Z=0
    g10: ArcOfCircle CenterX=-181.223 CenterY=-12.6042 CenterZ=0 NormalX=0 NormalY=0 NormalZ=1 AngleXU=0 Radius=13.9072 StartAngle=1.5708 EndAngle=2.70526
    g11: GeomPoint [constr] X=-181.223 Y=1.30297 Z=0
  constraints (23):
    c: Coincident(g0,g-5)
    c: Coincident(g1,g-6)
    c: Horizontal(g1)
    c: Coincident(g1,g0)
    c: Parallel(g0,g-4)
    c: Coincident(g2,g1)
    c: Coincident(g2,g0)
    c: Coincident(g3,g0)
    c: Equal(g4,g-5)
    c: Coincident(g4,g1)
    c: Coincident(g4,g0)
    c: InternalAlignment(g6-g9 -> g5) x4
    c: Vertical(g5,g0)
    c: Horizontal(g6)
    c: Coincident(g5,g0)
    c: DistanceX(g6,g-3) = 19.1
    c: Tangent(g10,g3) = -1.5708
    c: PointOnObject(g11,g10)
    c: Tangent(g5,g10,g11) = 1.5708
    c: Coincident(g10,g5)
    c: Coincident(g11,g7)
    c: Parallel(g3,g-4)
    c: DistanceY(g5,g0) = 19
FEATURE [Part::Part2DObjectPython] Clone2D001  label="Sketch130 (2D)"  # Draft 2D object (typed FeaturePython)
  Fuse = false
  Objects = -> [Sketch130]
  Placement = pos=(0,-2,-4e-16) rot=(1,0,0;1.5708rad)
  Scale = (1,1,1)
FEATURE [Sketcher::SketchObject] Sketch131
  ArcFitTolerance = 1e-06
  AttachmentOffset = pos=(0,0,-3.5) rot=(0,0,1;0rad)
  AttachmentSupport = -> [Pad016]
  ExternalGeometry = -> [Binder001]
  FullyConstrained = true
  MakeInternals = false
  MapMode = 5
  Placement = pos=(0,-0.1,-8e-16) rot=(1,0,0;1.5708rad)
  sketch-geometry (1):
    g0: GeomPoint X=-197.47 Y=8.55923 Z=0
  constraints (1):
    c: Symmetric(g-6,g-4,g0)
FEATURE [PartDesign::SubtractiveLoft] SubtractiveLoft002
  BaseFeature = -> SubtractivePipe003
  Closed = false
  Profile = -> Sketch129
  Refine = true
  Ruled = false
  Sections = -> [Sketch130]
  Suppressed = false
FEATURE [PartDesign::SubtractiveLoft] SubtractiveLoft003
  BaseFeature = -> SubtractiveLoft002
  Closed = false
  Profile = -> Clone2D001
  Refine = true
  Ruled = false
  Sections = -> [Sketch131]
  Suppressed = false
FEATURE [PartDesign::Chamfer] Chamfer010
  Angle = 45
  Base = -> SubtractiveLoft003 [Edge200,Edge201,Edge203,Edge202,Edge194]
  BaseFeature = -> SubtractiveLoft003
  ChamferType = 0
  FlipDirection = false
  Refine = true
  Size = 1.5
  Size2 = 1
  SupportTransform = false
  Suppressed = false
  UseAllEdges = false
FEATURE [PartDesign::Chamfer] Chamfer011
  Angle = 45
  Base = -> Chamfer010 [Edge15]
  BaseFeature = -> Chamfer010
  ChamferType = 0
  FlipDirection = false
  Refine = true
  Size = 3.5
  Size2 = 1
  SupportTransform = false
  Suppressed = false
  UseAllEdges = false
FEATURE [PartDesign::Chamfer] Chamfer012
  Angle = 45
  Base = -> Chamfer011 [Edge10]
  BaseFeature = -> Chamfer011
  ChamferType = 0
  FlipDirection = false
  Refine = true
  Size = 3.5
  Size2 = 1
  SupportTransform = false
  Suppressed = false
  UseAllEdges = false
FEATURE [PartDesign::Chamfer] Chamfer013
  Angle = 45
  Base = -> Chamfer012 [Edge146,Edge93]
  BaseFeature = -> Chamfer012
  ChamferType = 0
  FlipDirection = false
  Refine = true
  Size = 1.9
  Size2 = 1
  SupportTransform = false
  Suppressed = false
  UseAllEdges = false
FEATURE [Sketcher::SketchObject] Sketch132
  ArcFitTolerance = 1e-06
  AttachmentSupport = -> [Pad016]
  ExternalGeometry = -> [Binder001]
  FullyConstrained = true
  MakeInternals = false
  MapMode = 5
  Placement = pos=(0,-3.6,0) rot=(1,0,0;1.5708rad)
  sketch-geometry (3):
    g0: LineSegment [constr] StartX=-215.42 StartY=-53.0314 StartZ=0 EndX=-167.782 EndY=-53.0314 EndZ=0
    g1: Circle CenterX=-191.282 CenterY=-53.0314 CenterZ=0 NormalX=0 NormalY=0 NormalZ=1 AngleXU=0 Radius=11.5
    g2: Circle CenterX=-191.282 CenterY=-53.0314 CenterZ=0 NormalX=0 NormalY=0 NormalZ=1 AngleXU=0 Radius=10.7
  constraints (8):
    c: Coincident(g0,g-3)
    c: PointOnObject(g0,g-4)
    c: Horizontal(g0)
    c: Diameter(g1) = 23
    c: PointOnObject(g1,g0)
    c: DistanceX(g1,g0) = 23.5
    c: Diameter(g2) = 21.4
    c: Coincident(g2,g1)
FEATURE [PartDesign::Fillet] Fillet007
  Base = -> Chamfer013 [Edge84]
  BaseFeature = -> Chamfer013
  Radius = 1.1
  Refine = true
  SupportTransform = false
  Suppressed = false
  UseAllEdges = false
FEATURE [PartDesign::Fillet] Fillet008
  Base = -> Fillet007 [Edge77]
  BaseFeature = -> Fillet007
  Radius = 1.9
  Refine = true
  SupportTransform = false
  Suppressed = false
  UseAllEdges = false
FEATURE [PartDesign::Pocket] Pocket011
  BaseFeature = -> Fillet008
  Direction = (0,1,-2e-16)
  Length = 0.8
  Length2 = 5
  Profile = -> Sketch132
  ReferenceAxis = -> Sketch132 [N_Axis]
  Refine = true
  Suppressed = false
  Type = 0
FEATURE [Sketcher::SketchObject] Sketch134
  ArcFitTolerance = 1e-06
  AttachmentSupport = -> [Pocket011]
  FullyConstrained = true
  MakeInternals = false
  MapMode = 5
  Placement = pos=(0,-3.6,0) rot=(1,0,0;1.5708rad)
FEATURE [Part::Part2DObjectPython] ShapeString  # Draft 2D object (typed FeaturePython)
  FontFile = <path>
  Fuse = false
  Justification = 6
  JustificationReference = 0
  KeepLeftMargin = false
  MakeFace = true
  ObliqueAngle = 0
  Placement = pos=(-199,-3.6,-57.5) rot=(1,0,0;1.5708rad)
  ScaleToSize = true
  Size = 10
  String = AS
  Tracking = 0
FEATURE [PartDesign::Pocket] Pocket012
  BaseFeature = -> Pocket011
  Direction = (0,1,0)
  Length = 1
  Length2 = 5
  Profile = -> ShapeString
  ReferenceAxis = -> ShapeString [N_Axis]
  Refine = true
  Suppressed = false
  Type = 0
FEATURE [PartDesign::Body] Body007  label="lato DX"
  AllowCompound = false
  Group = -> [Binder001,Sketch114,Pad011,Chamfer014,Sketch115,Pocket006,Sketch116,Pad012,Sketch117,Pocket007,Sketch118,Pad013,Sketch119,Pocket008,Pad017,Chamfer009,Pocket009,Sketch123,Sketch120,Pad014,Pad018,Chamfer008,Pocket010,Sketch121,Pad015,Sketch122,Pad016,Sketch124,Sketch125,Sketch126,Sketch127,Sketch128,SubtractivePipe002,SubtractivePipe003,Sketch129,Sketch130,Clone2D001,Sketch131,SubtractiveLoft002,+11 more]
  Origin = -> Origin007
  Tip = -> Pocket012
note: 1 file-system path scrubbed to <path> (originals preserved in the JSON sidecar)
